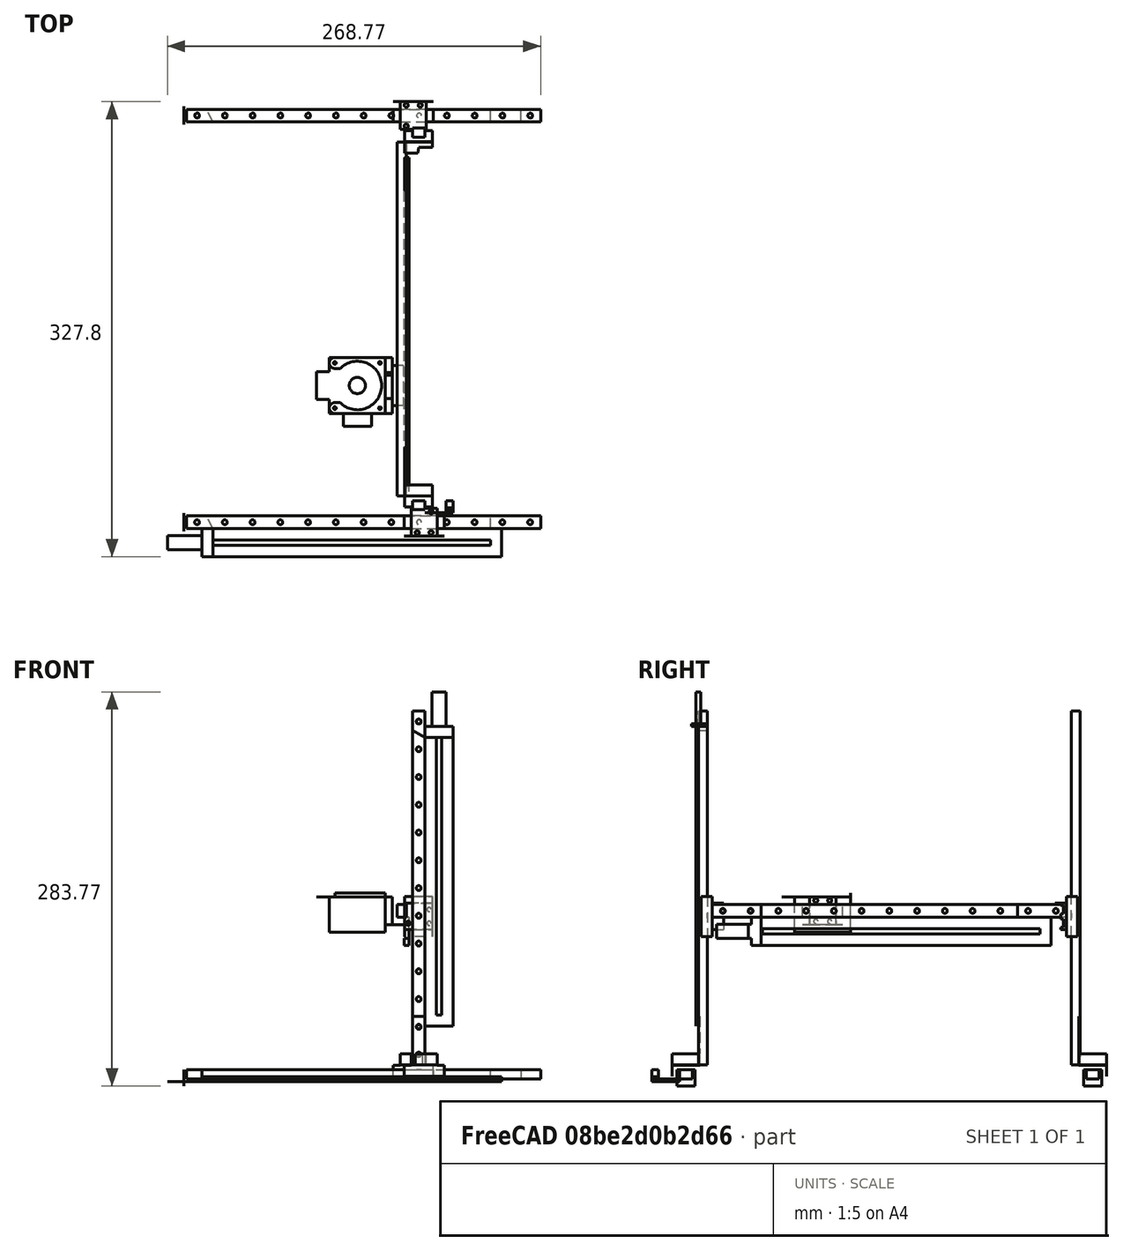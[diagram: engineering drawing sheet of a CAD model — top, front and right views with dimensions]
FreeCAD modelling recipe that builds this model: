
FCSTD DOCUMENT  (FreeCAD 0.21R33668 +26 (Git))
Label: v8
License: All rights reserved
LicenseURL: http://en.wikipedia.org/wiki/All_rights_reserved
objects: App::FeaturePython×217, Part::FeaturePython×128, App::Link×24
note: 127 computed .brp shape members not serialized (recipe doc carries the construction recipe); baked Part::Feature solids carry a one-line shape summary decoded from their .brp
EXTERNAL_REF file=parts/BaseMagnetoPot.FCStd obj=Body
EXTERNAL_REF file=parts/MG/mgn9c_13.FCStd obj=Body
EXTERNAL_REF file=parts/MG/mgn9c_slide.FCStd obj=Body001
EXTERNAL_REF file=parts/MagnetoPot/MagnetoPot.FCStd obj=Body
EXTERNAL_REF file=parts/NormalConnectorMagnet.FCStd obj=Body
EXTERNAL_REF file=parts/BaseMagnetoPot.FCStd obj=Body001
EXTERNAL_REF file=parts/NormalConnectorMagnet.FCStd obj=Body001
EXTERNAL_REF file=parts/Joystick_Holder.FCStd obj=Body
EXTERNAL_REF file=parts/R202.FCStd obj=Revolution

FEATURE [App::Link] Link  label="BaseMagentoPot"
  LinkedObject = -> <external parts/BaseMagnetoPot.FCStd>#Body
  _LinkOwner = 4
FEATURE [App::Link] Link001  label="Rail"
  LinkPlacement = pos=(-5.43338e-11,-6.2883e-12,2.71e-13) rot=(0,0,1;0rad)
  LinkedObject = -> <external parts/MG/mgn9c_13.FCStd>#Body
  Placement = pos=(-5.43338e-11,-6.2883e-12,2.71e-13) rot=(0,0,1;0rad)
  _LinkOwner = 4
FEATURE [App::Link] Link003  label="Slide"
  LinkPlacement = pos=(156.692,-5.5,2) rot=(0,0,1;0rad)
  LinkedObject = -> <external parts/MG/mgn9c_slide.FCStd>#Body001
  Placement = pos=(156.692,-5.5,2) rot=(0,0,1;0rad)
  _LinkOwner = 4
FEATURE [App::Link] Link004  label="MP1_L_0200_103_5_ST"
  LinkPlacement = pos=(11.12,-20.3,-2) rot=(0,0,1;0rad)
  LinkedObject = -> <external parts/MagnetoPot/MagnetoPot.FCStd>#Body
  Placement = pos=(11.12,-20.3,-2) rot=(0,0,1;0rad)
  _LinkOwner = 4
FEATURE [App::Link] Link005  label="NormalConnectorMagnet"
  LinkPlacement = pos=(156.692,-5.5,2) rot=(0,0,1;0rad)
  LinkedObject = -> <external parts/NormalConnectorMagnet.FCStd>#Body
  Placement = pos=(156.692,-5.5,2) rot=(0,0,1;0rad)
  _LinkOwner = 4
FEATURE [App::Link] Link006  label="Rail001"
  LinkPlacement = pos=(162.692,13.5,10) rot=(0.57735,0.57735,0.57735;4.18879rad)
  LinkedObject = -> <external parts/MG/mgn9c_13.FCStd>#Body
  Placement = pos=(162.692,13.5,10) rot=(0.57735,0.57735,0.57735;4.18879rad)
  _LinkOwner = 4
FEATURE [App::Link] Link007  label="BaseMagentoPot001"
  LinkPlacement = pos=(171.692,13.5,265) rot=(-0.57735,0.57735,0.57735;2.0944rad)
  LinkedObject = -> <external parts/BaseMagnetoPot.FCStd>#Body
  Placement = pos=(171.692,13.5,265) rot=(-0.57735,0.57735,0.57735;2.0944rad)
  _LinkOwner = 4
FEATURE [App::Link] Link008  label="MP1_L_0200_103_5_ST001"
  LinkPlacement = pos=(191.992,11.5,253.88) rot=(0.57735,-0.57735,-0.57735;4.18879rad)
  LinkedObject = -> <external parts/MagnetoPot/MagnetoPot.FCStd>#Body
  Placement = pos=(191.992,11.5,253.88) rot=(0.57735,-0.57735,-0.57735;4.18879rad)
  _LinkOwner = 4
FEATURE [App::Link] Link009  label="Slide001"
  LinkPlacement = pos=(157.192,15.5,102.634) rot=(0.57735,0.57735,0.57735;4.18879rad)
  LinkedObject = -> <external parts/MG/mgn9c_slide.FCStd>#Body001
  Placement = pos=(157.192,15.5,102.634) rot=(0.57735,0.57735,0.57735;4.18879rad)
  _LinkOwner = 4
FEATURE [App::Link] Link010  label="NormalConnectorMagnet001"
  LinkPlacement = pos=(177.192,15.5,131.534) rot=(0.57735,-0.57735,-0.57735;4.18879rad)
  LinkedObject = -> <external parts/NormalConnectorMagnet.FCStd>#Body
  Placement = pos=(177.192,15.5,131.534) rot=(0.57735,-0.57735,-0.57735;4.18879rad)
  _LinkOwner = 4
FEATURE [App::Link] Link011  label="MP1_L_0200_103_5_ST002"
  LinkPlacement = pos=(160.192,51.52,116.534) rot=(-0.57735,-0.57735,0.57735;2.0944rad)
  LinkedObject = -> <external parts/MagnetoPot/MagnetoPot.FCStd>#Body
  Placement = pos=(160.192,51.52,116.534) rot=(-0.57735,-0.57735,0.57735;2.0944rad)
  _LinkOwner = 4
FEATURE [App::Link] Link012  label="Rail002"
  LinkPlacement = pos=(158.192,23.5,125.534) rot=(0.57735,0.57735,-0.57735;4.18879rad)
  LinkedObject = -> <external parts/MG/mgn9c_13.FCStd>#Body
  Placement = pos=(158.192,23.5,125.534) rot=(0.57735,0.57735,-0.57735;4.18879rad)
  _LinkOwner = 4
FEATURE [App::Link] Link013  label="BaseMagnetoPot_Opposite"
  LinkPlacement = pos=(255,2.3947e-10,3.77443e-11) rot=(0,0,1;0rad)
  LinkedObject = -> <external parts/BaseMagnetoPot.FCStd>#Body001
  Placement = pos=(255,2.3947e-10,3.77443e-11) rot=(0,0,1;0rad)
  _LinkOwner = 4
FEATURE [App::Link] Link015  label="Slide002"
  LinkPlacement = pos=(177.192,286.5,102.634) rot=(-0.57735,0.57735,-0.57735;4.18879rad)
  LinkedObject = -> <external parts/MG/mgn9c_slide.FCStd>#Body001
  Placement = pos=(177.192,286.5,102.634) rot=(-0.57735,0.57735,-0.57735;4.18879rad)
  _LinkOwner = 4
FEATURE [App::Link] Link016  label="Rail003"
  LinkPlacement = pos=(171.692,288.5,10) rot=(0.57735,-0.57735,0.57735;2.0944rad)
  LinkedObject = -> <external parts/MG/mgn9c_13.FCStd>#Body
  Placement = pos=(171.692,288.5,10) rot=(0.57735,-0.57735,0.57735;2.0944rad)
  _LinkOwner = 4
FEATURE [App::Link] Link017  label="NormalConnectorMagnet002"
  LinkPlacement = pos=(177.692,307.5,2) rot=(0,0,1;3.14159rad)
  LinkedObject = -> <external parts/NormalConnectorMagnet.FCStd>#Body
  Placement = pos=(177.692,307.5,2) rot=(0,0,1;3.14159rad)
  _LinkOwner = 4
FEATURE [App::Link] Link018  label="Slide003"
  LinkPlacement = pos=(148.792,287.5,2) rot=(0,0,1;0rad)
  LinkedObject = -> <external parts/MG/mgn9c_slide.FCStd>#Body001
  Placement = pos=(148.792,287.5,2) rot=(0,0,1;0rad)
  _LinkOwner = 4
FEATURE [App::Link] Link019  label="Rail004"
  LinkPlacement = pos=(-5.5211e-10,293,-1.90036e-09) rot=(0,0,1;0rad)
  LinkedObject = -> <external parts/MG/mgn9c_13.FCStd>#Body
  Placement = pos=(-5.5211e-10,293,-1.90036e-09) rot=(0,0,1;0rad)
  _LinkOwner = 4
FEATURE [App::Link] Link020  label="BaseMagnetoPot_Opposite001"
  LinkPlacement = pos=(255,293,-2.0831e-09) rot=(0,0,1;0rad)
  LinkedObject = -> <external parts/BaseMagnetoPot.FCStd>#Body001
  Placement = pos=(255,293,-2.0831e-09) rot=(0,0,1;0rad)
  _LinkOwner = 4
FEATURE [App::Link] Link021  label="BaseMagentoPot002"
  LinkPlacement = pos=(-5.57052e-10,293,-1.68813e-09) rot=(0,0,1;0rad)
  LinkedObject = -> <external parts/BaseMagnetoPot.FCStd>#Body
  Placement = pos=(-5.57052e-10,293,-1.68813e-09) rot=(0,0,1;0rad)
  _LinkOwner = 4
FEATURE [App::Link] Link022  label="NormalConnector"
  LinkPlacement = pos=(177.192,270.5,131.534) rot=(-0.57735,0.57735,0.57735;2.0944rad)
  LinkedObject = -> <external parts/NormalConnectorMagnet.FCStd>#Body001
  Placement = pos=(177.192,270.5,131.534) rot=(-0.57735,0.57735,0.57735;2.0944rad)
  _LinkOwner = 4
FEATURE [App::Link] Link023  label="Slide004"
  LinkPlacement = pos=(156.192,117.438,111.034) rot=(-0.57735,0.57735,0.57735;4.18879rad)
  LinkedObject = -> <external parts/MG/mgn9c_slide.FCStd>#Body001
  Placement = pos=(156.192,117.438,111.034) rot=(-0.57735,0.57735,0.57735;4.18879rad)
  _LinkOwner = 4
FEATURE [App::Link] Link024  label="JoystickHolder"
  LinkPlacement = pos=(139.492,86.4879,131.034) rot=(0,0,1;0rad)
  LinkedObject = -> <external parts/Joystick_Holder.FCStd>#Body
  Placement = pos=(139.492,86.4879,131.034) rot=(0,0,1;0rad)
  _LinkOwner = 4
FEATURE [App::Link] Link025  label="Revolution"
  LinkPlacement = pos=(122.992,102.988,105.534) rot=(0,0,1;0rad)
  LinkedObject = -> <external parts/R202.FCStd>#Revolution
  Placement = pos=(122.992,102.988,105.534) rot=(0,0,1;0rad)
  _LinkOwner = 4
FEATURE [Part::FeaturePython] Parts  # WARN: FeaturePython — macro-defined, semantics opaque (R4)
  Group = -> [Link,Link001,Link003,Link004,Link005,Link006,Link007,Link008,Link009,Link010,Link011,Link012,Link013,Link015,Link016,Link017,Link018,Link019,Link020,Link021,Link022,Link023,Link024,Link025]
  GroupMode = 0
FEATURE [Part::FeaturePython] Assembly  # WARN: FeaturePython — macro-defined, semantics opaque (R4)
  AutoRelax = true
  BuildShape = 0
  Freeze = false
  Group = -> [Constraints,Elements,Parts]
  Verbose = false
  _SolverType = 1
  _Version = 1
FEATURE [App::FeaturePython] Constraints  # WARN: FeaturePython — macro-defined, semantics opaque (R4)
  Group = -> [Constraint,Constraint001,Constraint002,Constraint003,Constraint007,Constraint008,Constraint009,Constraint010,Constraint011,Constraint012,Constraint013,Constraint014,Constraint015,Constraint016,Constraint017,Constraint018,Constraint019,Constraint020,Constraint021,Constraint022,Constraint023,Constraint024,Constraint025,Constraint026,Constraint027,Constraint028,Constraint029,Constraint030,+44 more]
  _Version = 1
FEATURE [App::FeaturePython] Elements  # WARN: FeaturePython — macro-defined, semantics opaque (R4)
  Group = -> [_Element,_Element001,_Element002,_Element003,_Element004,_Element005,_Element008,_Element010,_Element011,_Element012,_Element013,_Element014,_Element015,_Element016,_Element017,_Element018,_Element019,_Element020,_Element021,_Element022,_Element023,_Element024,_Element025,_Element026,_Element027,_Element028,_Element029,_Element030,_Element031,_Element032,_Element033,_Element034,_Element035,+93 more]
FEATURE [App::FeaturePython] Constraint  label="Locked"  # WARN: FeaturePython — macro-defined, semantics opaque (R4)
  Disabled = false
  Group = -> [ElementLink]
  _ConstraintType = 0
  _Parent = -> Constraints
FEATURE [App::FeaturePython] ElementLink  label="_Element"  # link proxy (typed FeaturePython)
  LinkTransform = true
  LinkedObject = -> _Element
  _Parent = -> Constraint
FEATURE [Part::FeaturePython] _Element  # link proxy (typed FeaturePython)
  Detach = false
  LinkTransform = true
  LinkedObject = -> Link [Pad001.Face2]
  _Parent = -> Elements
FEATURE [App::FeaturePython] Constraint001  label="PlaneAlignment"  # WARN: FeaturePython — macro-defined, semantics opaque (R4)
  Angle = 0
  AnglePitch = 0
  AngleRoll = 0
  Cascade = false
  Disabled = false
  Group = -> [ElementLink001,ElementLink002]
  LockAngle = false
  _ConstraintType = 37
  _Parent = -> Constraints
FEATURE [App::FeaturePython] ElementLink001  label="_Element001"  # link proxy (typed FeaturePython)
  LinkTransform = true
  LinkedObject = -> _Element001
  _Parent = -> Constraint001
FEATURE [Part::FeaturePython] _Element001  # link proxy (typed FeaturePython)
  Detach = false
  LinkTransform = true
  LinkedObject = -> Link001 [LinearPattern.Face2]
  _Parent = -> Elements
FEATURE [App::FeaturePython] ElementLink002  label="_Element002"  # link proxy (typed FeaturePython)
  LinkTransform = true
  LinkedObject = -> _Element002
  _Parent = -> Constraint001
FEATURE [Part::FeaturePython] _Element002  # link proxy (typed FeaturePython)
  Detach = false
  LinkTransform = true
  LinkedObject = -> Link [Pad001.Face7]
  _Parent = -> Elements
FEATURE [App::FeaturePython] Constraint002  label="PlaneAlignment001"  # WARN: FeaturePython — macro-defined, semantics opaque (R4)
  Angle = 0
  AnglePitch = 0
  AngleRoll = 0
  Cascade = false
  Disabled = false
  Group = -> [ElementLink003,ElementLink004]
  LockAngle = false
  _ConstraintType = 37
  _Parent = -> Constraints
FEATURE [App::FeaturePython] ElementLink003  label="_Element"  # link proxy (typed FeaturePython)
  LinkTransform = true
  LinkedObject = -> _Element
  _Parent = -> Constraint002
FEATURE [App::FeaturePython] ElementLink004  label="_Element003"  # link proxy (typed FeaturePython)
  LinkTransform = true
  LinkedObject = -> _Element003
  _Parent = -> Constraint002
FEATURE [Part::FeaturePython] _Element003  # link proxy (typed FeaturePython)
  Detach = false
  LinkTransform = true
  LinkedObject = -> Link001 [LinearPattern.Face4]
  _Parent = -> Elements
FEATURE [App::FeaturePython] Constraint003  label="PlaneAlignment002"  # WARN: FeaturePython — macro-defined, semantics opaque (R4)
  Angle = 0
  AnglePitch = 0
  AngleRoll = 0
  Cascade = false
  Disabled = false
  Group = -> [ElementLink005,ElementLink006]
  LockAngle = false
  _ConstraintType = 37
  _Parent = -> Constraints
FEATURE [App::FeaturePython] ElementLink005  label="_Element004"  # link proxy (typed FeaturePython)
  LinkTransform = true
  LinkedObject = -> _Element004
  _Parent = -> Constraint003
FEATURE [Part::FeaturePython] _Element004  # link proxy (typed FeaturePython)
  Detach = false
  LinkTransform = true
  LinkedObject = -> Link001 [LinearPattern.Face1]
  _Parent = -> Elements
FEATURE [App::FeaturePython] ElementLink006  label="_Element005"  # link proxy (typed FeaturePython)
  LinkTransform = true
  LinkedObject = -> _Element005
  _Parent = -> Constraint003
FEATURE [Part::FeaturePython] _Element005  # link proxy (typed FeaturePython)
  Detach = false
  LinkTransform = true
  LinkedObject = -> Link [Pad001.Face8]
  _Parent = -> Elements
FEATURE [Part::FeaturePython] _Element008  # link proxy (typed FeaturePython)
  Detach = false
  LinkTransform = true
  LinkedObject = -> Link [Pad001.Face10]
  _Parent = -> Elements
FEATURE [App::FeaturePython] Constraint007  label="PlaneAlignment006"  # WARN: FeaturePython — macro-defined, semantics opaque (R4)
  Angle = 0
  AnglePitch = 0
  AngleRoll = 0
  Cascade = false
  Disabled = false
  Group = -> [ElementLink013,ElementLink014]
  LockAngle = false
  _ConstraintType = 37
  _Parent = -> Constraints
FEATURE [App::FeaturePython] ElementLink013  label="_Element010"  # link proxy (typed FeaturePython)
  LinkTransform = true
  LinkedObject = -> _Element010
  _Parent = -> Constraint007
FEATURE [Part::FeaturePython] _Element010  # link proxy (typed FeaturePython)
  Detach = false
  LinkTransform = true
  LinkedObject = -> Link003 [Pocket003.Face12]
  _Parent = -> Elements
FEATURE [App::FeaturePython] ElementLink014  label="_Element011"  # link proxy (typed FeaturePython)
  LinkTransform = true
  LinkedObject = -> _Element011
  _Parent = -> Constraint007
FEATURE [Part::FeaturePython] _Element011  # link proxy (typed FeaturePython)
  Detach = false
  LinkTransform = true
  LinkedObject = -> Link001 [LinearPattern.Face6]
  _Parent = -> Elements
FEATURE [App::FeaturePython] Constraint008  label="PlaneAlignment007"  # WARN: FeaturePython — macro-defined, semantics opaque (R4)
  Angle = 0
  AnglePitch = 0
  AngleRoll = 0
  Cascade = false
  Disabled = false
  Group = -> [ElementLink015,ElementLink016]
  LockAngle = false
  _ConstraintType = 37
  _Parent = -> Constraints
FEATURE [App::FeaturePython] ElementLink015  label="_Element012"  # link proxy (typed FeaturePython)
  LinkTransform = true
  LinkedObject = -> _Element012
  _Parent = -> Constraint008
FEATURE [Part::FeaturePython] _Element012  # link proxy (typed FeaturePython)
  Detach = false
  LinkTransform = true
  LinkedObject = -> Link003 [Pocket003.Face11]
  _Parent = -> Elements
FEATURE [App::FeaturePython] ElementLink016  label="_Element013"  # link proxy (typed FeaturePython)
  LinkTransform = true
  LinkedObject = -> _Element013
  _Parent = -> Constraint008
FEATURE [Part::FeaturePython] _Element013  # link proxy (typed FeaturePython)
  Detach = false
  LinkTransform = true
  LinkedObject = -> Link001 [LinearPattern.Face5]
  _Parent = -> Elements
FEATURE [App::FeaturePython] Constraint009  label="PlaneAlignment008"  # WARN: FeaturePython — macro-defined, semantics opaque (R4)
  Angle = 0
  AnglePitch = 0
  AngleRoll = 0
  Cascade = false
  Disabled = false
  Group = -> [ElementLink017,ElementLink018]
  LockAngle = false
  _ConstraintType = 37
  _Parent = -> Constraints
FEATURE [App::FeaturePython] ElementLink017  label="_Element014"  # link proxy (typed FeaturePython)
  LinkTransform = true
  LinkedObject = -> _Element014
  _Parent = -> Constraint009
FEATURE [Part::FeaturePython] _Element014  # link proxy (typed FeaturePython)
  Detach = false
  LinkTransform = true
  LinkedObject = -> Link004 [Pad.Face4]
  _Parent = -> Elements
FEATURE [App::FeaturePython] ElementLink018  label="_Element015"  # link proxy (typed FeaturePython)
  LinkTransform = true
  LinkedObject = -> _Element015
  _Parent = -> Constraint009
FEATURE [Part::FeaturePython] _Element015  # link proxy (typed FeaturePython)
  Detach = false
  LinkTransform = true
  LinkedObject = -> Link [Pocket.Face15]
  _Parent = -> Elements
FEATURE [App::FeaturePython] Constraint010  label="PlaneAlignment009"  # WARN: FeaturePython — macro-defined, semantics opaque (R4)
  Angle = 0
  AnglePitch = 0
  AngleRoll = 0
  Cascade = false
  Disabled = false
  Group = -> [ElementLink019,ElementLink020]
  LockAngle = false
  _ConstraintType = 37
  _Parent = -> Constraints
FEATURE [App::FeaturePython] ElementLink019  label="_Element016"  # link proxy (typed FeaturePython)
  LinkTransform = true
  LinkedObject = -> _Element016
  _Parent = -> Constraint010
FEATURE [Part::FeaturePython] _Element016  # link proxy (typed FeaturePython)
  Detach = false
  LinkTransform = true
  LinkedObject = -> Link004 [Pad.Face1]
  _Parent = -> Elements
FEATURE [App::FeaturePython] ElementLink020  label="_Element017"  # link proxy (typed FeaturePython)
  LinkTransform = true
  LinkedObject = -> _Element017
  _Parent = -> Constraint010
FEATURE [Part::FeaturePython] _Element017  # link proxy (typed FeaturePython)
  Detach = false
  LinkTransform = true
  LinkedObject = -> Link [Pocket.Face4]
  _Parent = -> Elements
FEATURE [App::FeaturePython] Constraint011  label="PlaneAlignment010"  # WARN: FeaturePython — macro-defined, semantics opaque (R4)
  Angle = 0
  AnglePitch = 0
  AngleRoll = 0
  Cascade = false
  Disabled = false
  Group = -> [ElementLink021,ElementLink022]
  LockAngle = false
  _ConstraintType = 37
  _Parent = -> Constraints
FEATURE [App::FeaturePython] ElementLink021  label="_Element018"  # link proxy (typed FeaturePython)
  LinkTransform = true
  LinkedObject = -> _Element018
  _Parent = -> Constraint011
FEATURE [Part::FeaturePython] _Element018  # link proxy (typed FeaturePython)
  Detach = false
  LinkTransform = true
  LinkedObject = -> Link [Pocket.Face8]
  _Parent = -> Elements
FEATURE [App::FeaturePython] ElementLink022  label="_Element019"  # link proxy (typed FeaturePython)
  LinkTransform = true
  LinkedObject = -> _Element019
  _Parent = -> Constraint011
FEATURE [Part::FeaturePython] _Element019  # link proxy (typed FeaturePython)
  Detach = false
  LinkTransform = true
  LinkedObject = -> Link004 [Pad.Face13]
  _Parent = -> Elements
FEATURE [App::FeaturePython] Constraint012  label="PlaneAlignment011"  # WARN: FeaturePython — macro-defined, semantics opaque (R4)
  Angle = 0
  AnglePitch = 0
  AngleRoll = 0
  Cascade = false
  Disabled = false
  Group = -> [ElementLink023,ElementLink024]
  LockAngle = false
  _ConstraintType = 37
  _Parent = -> Constraints
FEATURE [App::FeaturePython] ElementLink023  label="_Element020"  # link proxy (typed FeaturePython)
  LinkTransform = true
  LinkedObject = -> _Element020
  _Parent = -> Constraint012
FEATURE [Part::FeaturePython] _Element020  # link proxy (typed FeaturePython)
  Detach = false
  LinkTransform = true
  LinkedObject = -> Link005 [Pocket003.Face2]
  _Parent = -> Elements
FEATURE [App::FeaturePython] ElementLink024  label="_Element021"  # link proxy (typed FeaturePython)
  LinkTransform = true
  LinkedObject = -> _Element021
  _Parent = -> Constraint012
FEATURE [Part::FeaturePython] _Element021  # link proxy (typed FeaturePython)
  Detach = false
  LinkTransform = true
  LinkedObject = -> Link003 [Pocket003.Face6]
  _Parent = -> Elements
FEATURE [App::FeaturePython] Constraint013  label="PlaneAlignment012"  # WARN: FeaturePython — macro-defined, semantics opaque (R4)
  Angle = 0
  AnglePitch = 0
  AngleRoll = 0
  Cascade = false
  Disabled = false
  Group = -> [ElementLink025,ElementLink026]
  LockAngle = false
  _ConstraintType = 37
  _Parent = -> Constraints
FEATURE [App::FeaturePython] ElementLink025  label="_Element022"  # link proxy (typed FeaturePython)
  LinkTransform = true
  LinkedObject = -> _Element022
  _Parent = -> Constraint013
FEATURE [Part::FeaturePython] _Element022  # link proxy (typed FeaturePython)
  Detach = false
  LinkTransform = true
  LinkedObject = -> Link005 [Pocket003.Face10]
  _Parent = -> Elements
FEATURE [App::FeaturePython] ElementLink026  label="_Element023"  # link proxy (typed FeaturePython)
  LinkTransform = true
  LinkedObject = -> _Element023
  _Parent = -> Constraint013
FEATURE [Part::FeaturePython] _Element023  # link proxy (typed FeaturePython)
  Detach = false
  LinkTransform = true
  LinkedObject = -> Link003 [Pocket003.Face1]
  _Parent = -> Elements
FEATURE [App::FeaturePython] Constraint014  label="PlaneAlignment013"  # WARN: FeaturePython — macro-defined, semantics opaque (R4)
  Angle = 0
  AnglePitch = 0
  AngleRoll = 0
  Cascade = false
  Disabled = false
  Group = -> [ElementLink027,ElementLink028]
  LockAngle = false
  _ConstraintType = 37
  _Parent = -> Constraints
FEATURE [App::FeaturePython] ElementLink027  label="_Element024"  # link proxy (typed FeaturePython)
  LinkTransform = true
  LinkedObject = -> _Element024
  _Parent = -> Constraint014
FEATURE [Part::FeaturePython] _Element024  # link proxy (typed FeaturePython)
  Detach = false
  LinkTransform = true
  LinkedObject = -> Link005 [Pocket003.Face5]
  _Parent = -> Elements
FEATURE [App::FeaturePython] ElementLink028  label="_Element025"  # link proxy (typed FeaturePython)
  LinkTransform = true
  LinkedObject = -> _Element025
  _Parent = -> Constraint014
FEATURE [Part::FeaturePython] _Element025  # link proxy (typed FeaturePython)
  Detach = false
  LinkTransform = true
  LinkedObject = -> Link003 [Pocket003.Face7]
  _Parent = -> Elements
FEATURE [App::FeaturePython] Constraint015  label="PlaneAlignment014"  # WARN: FeaturePython — macro-defined, semantics opaque (R4)
  Angle = 0
  AnglePitch = 0
  AngleRoll = 0
  Cascade = false
  Disabled = false
  Group = -> [ElementLink029,ElementLink030]
  LockAngle = false
  _ConstraintType = 37
  _Parent = -> Constraints
FEATURE [App::FeaturePython] ElementLink029  label="_Element026"  # link proxy (typed FeaturePython)
  LinkTransform = true
  LinkedObject = -> _Element026
  _Parent = -> Constraint015
FEATURE [Part::FeaturePython] _Element026  # link proxy (typed FeaturePython)
  Detach = false
  LinkTransform = true
  LinkedObject = -> Link006 [LinearPattern.Face4]
  _Parent = -> Elements
FEATURE [App::FeaturePython] ElementLink030  label="_Element027"  # link proxy (typed FeaturePython)
  LinkTransform = true
  LinkedObject = -> _Element027
  _Parent = -> Constraint015
FEATURE [Part::FeaturePython] _Element027  # link proxy (typed FeaturePython)
  Detach = false
  LinkTransform = true
  LinkedObject = -> Link005 [Pocket003.Face6]
  _Parent = -> Elements
FEATURE [App::FeaturePython] Constraint016  label="PlaneAlignment015"  # WARN: FeaturePython — macro-defined, semantics opaque (R4)
  Angle = 0
  AnglePitch = 0
  AngleRoll = 0
  Cascade = false
  Disabled = false
  Group = -> [ElementLink031,ElementLink032]
  LockAngle = false
  _ConstraintType = 37
  _Parent = -> Constraints
FEATURE [App::FeaturePython] ElementLink031  label="_Element021"  # link proxy (typed FeaturePython)
  LinkTransform = true
  LinkedObject = -> _Element021
  _Parent = -> Constraint016
FEATURE [App::FeaturePython] ElementLink032  label="_Element028"  # link proxy (typed FeaturePython)
  LinkTransform = true
  LinkedObject = -> _Element028
  _Parent = -> Constraint016
FEATURE [Part::FeaturePython] _Element028  # link proxy (typed FeaturePython)
  Detach = false
  LinkTransform = true
  LinkedObject = -> Link006 [LinearPattern.Face2]
  _Parent = -> Elements
FEATURE [App::FeaturePython] Constraint017  label="PlaneAlignment016"  # WARN: FeaturePython — macro-defined, semantics opaque (R4)
  Angle = 0
  AnglePitch = 0
  AngleRoll = 0
  Cascade = false
  Disabled = false
  Group = -> [ElementLink033,ElementLink034]
  LockAngle = false
  _ConstraintType = 37
  _Parent = -> Constraints
FEATURE [App::FeaturePython] ElementLink033  label="_Element029"  # link proxy (typed FeaturePython)
  LinkTransform = true
  LinkedObject = -> _Element029
  _Parent = -> Constraint017
FEATURE [Part::FeaturePython] _Element029  # link proxy (typed FeaturePython)
  Detach = false
  LinkTransform = true
  LinkedObject = -> Link005 [Pocket003.Face3]
  _Parent = -> Elements
FEATURE [App::FeaturePython] ElementLink034  label="_Element030"  # link proxy (typed FeaturePython)
  LinkTransform = true
  LinkedObject = -> _Element030
  _Parent = -> Constraint017
FEATURE [Part::FeaturePython] _Element030  # link proxy (typed FeaturePython)
  Detach = false
  LinkTransform = true
  LinkedObject = -> Link006 [LinearPattern.Face1]
  _Parent = -> Elements
FEATURE [App::FeaturePython] Constraint018  label="PlaneAlignment017"  # WARN: FeaturePython — macro-defined, semantics opaque (R4)
  Angle = 0
  AnglePitch = 0
  AngleRoll = 0
  Cascade = false
  Disabled = false
  Group = -> [ElementLink035,ElementLink036]
  LockAngle = false
  _ConstraintType = 37
  _Parent = -> Constraints
FEATURE [App::FeaturePython] ElementLink035  label="_Element031"  # link proxy (typed FeaturePython)
  LinkTransform = true
  LinkedObject = -> _Element031
  _Parent = -> Constraint018
FEATURE [Part::FeaturePython] _Element031  # link proxy (typed FeaturePython)
  Detach = false
  LinkTransform = true
  LinkedObject = -> Link007 [Pocket.Face30]
  _Parent = -> Elements
FEATURE [App::FeaturePython] ElementLink036  label="_Element030"  # link proxy (typed FeaturePython)
  LinkTransform = true
  LinkedObject = -> _Element030
  _Parent = -> Constraint018
FEATURE [App::FeaturePython] Constraint019  label="PlaneAlignment018"  # WARN: FeaturePython — macro-defined, semantics opaque (R4)
  Angle = 0
  AnglePitch = 0
  AngleRoll = 0
  Cascade = false
  Disabled = false
  Group = -> [ElementLink037,ElementLink038]
  LockAngle = false
  _ConstraintType = 37
  _Parent = -> Constraints
FEATURE [App::FeaturePython] ElementLink037  label="_Element032"  # link proxy (typed FeaturePython)
  LinkTransform = true
  LinkedObject = -> _Element032
  _Parent = -> Constraint019
FEATURE [Part::FeaturePython] _Element032  # link proxy (typed FeaturePython)
  Detach = false
  LinkTransform = true
  LinkedObject = -> Link006 [LinearPattern.Face3]
  _Parent = -> Elements
FEATURE [App::FeaturePython] ElementLink038  label="_Element033"  # link proxy (typed FeaturePython)
  LinkTransform = true
  LinkedObject = -> _Element033
  _Parent = -> Constraint019
FEATURE [Part::FeaturePython] _Element033  # link proxy (typed FeaturePython)
  Detach = false
  LinkTransform = true
  LinkedObject = -> Link007 [Pocket.Face31]
  _Parent = -> Elements
FEATURE [App::FeaturePython] Constraint020  label="PlaneAlignment019"  # WARN: FeaturePython — macro-defined, semantics opaque (R4)
  Angle = 0
  AnglePitch = 0
  AngleRoll = 0
  Cascade = false
  Disabled = false
  Group = -> [ElementLink039,ElementLink040]
  LockAngle = false
  _ConstraintType = 37
  _Parent = -> Constraints
FEATURE [App::FeaturePython] ElementLink039  label="_Element034"  # link proxy (typed FeaturePython)
  LinkTransform = true
  LinkedObject = -> _Element034
  _Parent = -> Constraint020
FEATURE [Part::FeaturePython] _Element034  # link proxy (typed FeaturePython)
  Detach = false
  LinkTransform = true
  LinkedObject = -> Link007 [Pocket.Face24]
  _Parent = -> Elements
FEATURE [App::FeaturePython] ElementLink040  label="_Element026"  # link proxy (typed FeaturePython)
  LinkTransform = true
  LinkedObject = -> _Element026
  _Parent = -> Constraint020
FEATURE [App::FeaturePython] Constraint021  label="PlaneAlignment020"  # WARN: FeaturePython — macro-defined, semantics opaque (R4)
  Angle = 0
  AnglePitch = 0
  AngleRoll = 0
  Cascade = false
  Disabled = false
  Group = -> [ElementLink041,ElementLink042]
  LockAngle = false
  _ConstraintType = 37
  _Parent = -> Constraints
FEATURE [App::FeaturePython] ElementLink041  label="_Element035"  # link proxy (typed FeaturePython)
  LinkTransform = true
  LinkedObject = -> _Element035
  _Parent = -> Constraint021
FEATURE [Part::FeaturePython] _Element035  # link proxy (typed FeaturePython)
  Detach = false
  LinkTransform = true
  LinkedObject = -> Link008 [Pad.Face8]
  _Parent = -> Elements
FEATURE [App::FeaturePython] ElementLink042  label="_Element036"  # link proxy (typed FeaturePython)
  LinkTransform = true
  LinkedObject = -> _Element036
  _Parent = -> Constraint021
FEATURE [Part::FeaturePython] _Element036  # link proxy (typed FeaturePython)
  Detach = false
  LinkTransform = true
  LinkedObject = -> Link007 [Pocket.Face1]
  _Parent = -> Elements
FEATURE [App::FeaturePython] Constraint022  label="PlaneAlignment021"  # WARN: FeaturePython — macro-defined, semantics opaque (R4)
  Angle = 0
  AnglePitch = 0
  AngleRoll = 0
  Cascade = false
  Disabled = false
  Group = -> [ElementLink043,ElementLink044]
  LockAngle = false
  _ConstraintType = 37
  _Parent = -> Constraints
FEATURE [App::FeaturePython] ElementLink043  label="_Element037"  # link proxy (typed FeaturePython)
  LinkTransform = true
  LinkedObject = -> _Element037
  _Parent = -> Constraint022
FEATURE [Part::FeaturePython] _Element037  # link proxy (typed FeaturePython)
  Detach = false
  LinkTransform = true
  LinkedObject = -> Link008 [Pad.Face1]
  _Parent = -> Elements
FEATURE [App::FeaturePython] ElementLink044  label="_Element038"  # link proxy (typed FeaturePython)
  LinkTransform = true
  LinkedObject = -> _Element038
  _Parent = -> Constraint022
FEATURE [Part::FeaturePython] _Element038  # link proxy (typed FeaturePython)
  Detach = false
  LinkTransform = true
  LinkedObject = -> Link007 [Pocket.Face4]
  _Parent = -> Elements
FEATURE [App::FeaturePython] Constraint023  label="PlaneAlignment022"  # WARN: FeaturePython — macro-defined, semantics opaque (R4)
  Angle = 0
  AnglePitch = 0
  AngleRoll = 0
  Cascade = false
  Disabled = false
  Group = -> [ElementLink045,ElementLink046]
  LockAngle = false
  _ConstraintType = 37
  _Parent = -> Constraints
FEATURE [App::FeaturePython] ElementLink045  label="_Element039"  # link proxy (typed FeaturePython)
  LinkTransform = true
  LinkedObject = -> _Element039
  _Parent = -> Constraint023
FEATURE [Part::FeaturePython] _Element039  # link proxy (typed FeaturePython)
  Detach = false
  LinkTransform = true
  LinkedObject = -> Link008 [Pad.Face13]
  _Parent = -> Elements
FEATURE [App::FeaturePython] ElementLink046  label="_Element040"  # link proxy (typed FeaturePython)
  LinkTransform = true
  LinkedObject = -> _Element040
  _Parent = -> Constraint023
FEATURE [Part::FeaturePython] _Element040  # link proxy (typed FeaturePython)
  Detach = false
  LinkTransform = true
  LinkedObject = -> Link007 [Pocket.Face8]
  _Parent = -> Elements
FEATURE [App::FeaturePython] Constraint024  label="PlaneAlignment023"  # WARN: FeaturePython — macro-defined, semantics opaque (R4)
  Angle = 0
  AnglePitch = 0
  AngleRoll = 0
  Cascade = false
  Disabled = false
  Group = -> [ElementLink047,ElementLink048]
  LockAngle = false
  _ConstraintType = 37
  _Parent = -> Constraints
FEATURE [App::FeaturePython] ElementLink047  label="_Element041"  # link proxy (typed FeaturePython)
  LinkTransform = true
  LinkedObject = -> _Element041
  _Parent = -> Constraint024
FEATURE [Part::FeaturePython] _Element041  # link proxy (typed FeaturePython)
  Detach = false
  LinkTransform = true
  LinkedObject = -> Link009 [Pocket003.Face11]
  _Parent = -> Elements
FEATURE [App::FeaturePython] ElementLink048  label="_Element042"  # link proxy (typed FeaturePython)
  LinkTransform = true
  LinkedObject = -> _Element042
  _Parent = -> Constraint024
FEATURE [Part::FeaturePython] _Element042  # link proxy (typed FeaturePython)
  Detach = false
  LinkTransform = true
  LinkedObject = -> Link006 [LinearPattern.Face5]
  _Parent = -> Elements
FEATURE [App::FeaturePython] Constraint025  label="PlaneAlignment024"  # WARN: FeaturePython — macro-defined, semantics opaque (R4)
  Angle = 0
  AnglePitch = 0
  AngleRoll = 0
  Cascade = false
  Disabled = false
  Group = -> [ElementLink049,ElementLink050]
  LockAngle = false
  _ConstraintType = 37
  _Parent = -> Constraints
FEATURE [App::FeaturePython] ElementLink049  label="_Element043"  # link proxy (typed FeaturePython)
  LinkTransform = true
  LinkedObject = -> _Element043
  _Parent = -> Constraint025
FEATURE [Part::FeaturePython] _Element043  # link proxy (typed FeaturePython)
  Detach = false
  LinkTransform = true
  LinkedObject = -> Link009 [Pocket003.Face12]
  _Parent = -> Elements
FEATURE [App::FeaturePython] ElementLink050  label="_Element044"  # link proxy (typed FeaturePython)
  LinkTransform = true
  LinkedObject = -> _Element044
  _Parent = -> Constraint025
FEATURE [Part::FeaturePython] _Element044  # link proxy (typed FeaturePython)
  Detach = false
  LinkTransform = true
  LinkedObject = -> Link006 [LinearPattern.Face6]
  _Parent = -> Elements
FEATURE [App::FeaturePython] Constraint026  label="PlaneAlignment025"  # WARN: FeaturePython — macro-defined, semantics opaque (R4)
  Angle = 0
  AnglePitch = 0
  AngleRoll = 0
  Cascade = false
  Disabled = false
  Group = -> [ElementLink051,ElementLink052]
  LockAngle = false
  _ConstraintType = 37
  _Parent = -> Constraints
FEATURE [App::FeaturePython] ElementLink051  label="_Element045"  # link proxy (typed FeaturePython)
  LinkTransform = true
  LinkedObject = -> _Element045
  _Parent = -> Constraint026
FEATURE [Part::FeaturePython] _Element045  # link proxy (typed FeaturePython)
  Detach = false
  LinkTransform = true
  LinkedObject = -> Link010 [Pocket003.Face2]
  _Parent = -> Elements
FEATURE [App::FeaturePython] ElementLink052  label="_Element046"  # link proxy (typed FeaturePython)
  LinkTransform = true
  LinkedObject = -> _Element046
  _Parent = -> Constraint026
FEATURE [Part::FeaturePython] _Element046  # link proxy (typed FeaturePython)
  Detach = false
  LinkTransform = true
  LinkedObject = -> Link009 [Pocket003.Face6]
  _Parent = -> Elements
FEATURE [App::FeaturePython] Constraint027  label="PlaneAlignment026"  # WARN: FeaturePython — macro-defined, semantics opaque (R4)
  Angle = 0
  AnglePitch = 0
  AngleRoll = 0
  Cascade = false
  Disabled = false
  Group = -> [ElementLink053,ElementLink054]
  LockAngle = false
  _ConstraintType = 37
  _Parent = -> Constraints
FEATURE [App::FeaturePython] ElementLink053  label="_Element047"  # link proxy (typed FeaturePython)
  LinkTransform = true
  LinkedObject = -> _Element047
  _Parent = -> Constraint027
FEATURE [Part::FeaturePython] _Element047  # link proxy (typed FeaturePython)
  Detach = false
  LinkTransform = true
  LinkedObject = -> Link010 [Pocket003.Face5]
  _Parent = -> Elements
FEATURE [App::FeaturePython] ElementLink054  label="_Element048"  # link proxy (typed FeaturePython)
  LinkTransform = true
  LinkedObject = -> _Element048
  _Parent = -> Constraint027
FEATURE [Part::FeaturePython] _Element048  # link proxy (typed FeaturePython)
  Detach = false
  LinkTransform = true
  LinkedObject = -> Link009 [Pocket003.Face5]
  _Parent = -> Elements
FEATURE [App::FeaturePython] Constraint028  label="PlaneAlignment027"  # WARN: FeaturePython — macro-defined, semantics opaque (R4)
  Angle = 0
  AnglePitch = 0
  AngleRoll = 0
  Cascade = false
  Disabled = false
  Group = -> [ElementLink055,ElementLink056]
  LockAngle = false
  _ConstraintType = 37
  _Parent = -> Constraints
FEATURE [App::FeaturePython] ElementLink055  label="_Element049"  # link proxy (typed FeaturePython)
  LinkTransform = true
  LinkedObject = -> _Element049
  _Parent = -> Constraint028
FEATURE [Part::FeaturePython] _Element049  # link proxy (typed FeaturePython)
  Detach = false
  LinkTransform = true
  LinkedObject = -> Link010 [Pocket003.Face8]
  _Parent = -> Elements
FEATURE [App::FeaturePython] ElementLink056  label="_Element050"  # link proxy (typed FeaturePython)
  LinkTransform = true
  LinkedObject = -> _Element050
  _Parent = -> Constraint028
FEATURE [Part::FeaturePython] _Element050  # link proxy (typed FeaturePython)
  Detach = false
  LinkTransform = true
  LinkedObject = -> Link009 [Pocket003.Face1]
  _Parent = -> Elements
FEATURE [App::FeaturePython] Constraint029  label="PlaneAlignment028"  # WARN: FeaturePython — macro-defined, semantics opaque (R4)
  Angle = 0
  AnglePitch = 0
  AngleRoll = 0
  Cascade = false
  Disabled = false
  Group = -> [ElementLink057,ElementLink058]
  LockAngle = false
  _ConstraintType = 37
  _Parent = -> Constraints
FEATURE [App::FeaturePython] ElementLink057  label="_Element051"  # link proxy (typed FeaturePython)
  LinkTransform = true
  LinkedObject = -> _Element051
  _Parent = -> Constraint029
FEATURE [Part::FeaturePython] _Element051  # link proxy (typed FeaturePython)
  Detach = false
  LinkTransform = true
  LinkedObject = -> Link011 [Pad.Face2]
  _Parent = -> Elements
FEATURE [App::FeaturePython] ElementLink058  label="_Element052"  # link proxy (typed FeaturePython)
  LinkTransform = true
  LinkedObject = -> _Element052
  _Parent = -> Constraint029
FEATURE [Part::FeaturePython] _Element052  # link proxy (typed FeaturePython)
  Detach = false
  LinkTransform = true
  LinkedObject = -> Link010 [Pocket004.Face23]
  _Parent = -> Elements
FEATURE [App::FeaturePython] Constraint030  label="PlaneAlignment029"  # WARN: FeaturePython — macro-defined, semantics opaque (R4)
  Angle = 0
  AnglePitch = 0
  AngleRoll = 0
  Cascade = false
  Disabled = false
  Group = -> [ElementLink059,ElementLink060]
  LockAngle = false
  _ConstraintType = 37
  _Parent = -> Constraints
FEATURE [App::FeaturePython] ElementLink059  label="_Element053"  # link proxy (typed FeaturePython)
  LinkTransform = true
  LinkedObject = -> _Element053
  _Parent = -> Constraint030
FEATURE [Part::FeaturePython] _Element053  # link proxy (typed FeaturePython)
  Detach = false
  LinkTransform = true
  LinkedObject = -> Link011 [Pad.Face5]
  _Parent = -> Elements
FEATURE [App::FeaturePython] ElementLink060  label="_Element054"  # link proxy (typed FeaturePython)
  LinkTransform = true
  LinkedObject = -> _Element054
  _Parent = -> Constraint030
FEATURE [Part::FeaturePython] _Element054  # link proxy (typed FeaturePython)
  Detach = false
  LinkTransform = true
  LinkedObject = -> Link010 [Pocket004.Face27]
  _Parent = -> Elements
FEATURE [App::FeaturePython] Constraint031  label="PlaneAlignment030"  # WARN: FeaturePython — macro-defined, semantics opaque (R4)
  Angle = 0
  AnglePitch = 0
  AngleRoll = 0
  Cascade = false
  Disabled = false
  Group = -> [ElementLink061,ElementLink062]
  LockAngle = false
  _ConstraintType = 37
  _Parent = -> Constraints
FEATURE [App::FeaturePython] ElementLink061  label="_Element055"  # link proxy (typed FeaturePython)
  LinkTransform = true
  LinkedObject = -> _Element055
  _Parent = -> Constraint031
FEATURE [Part::FeaturePython] _Element055  # link proxy (typed FeaturePython)
  Detach = false
  LinkTransform = true
  LinkedObject = -> Link011 [Pad.Face13]
  _Parent = -> Elements
FEATURE [App::FeaturePython] ElementLink062  label="_Element056"  # link proxy (typed FeaturePython)
  LinkTransform = true
  LinkedObject = -> _Element056
  _Parent = -> Constraint031
FEATURE [Part::FeaturePython] _Element056  # link proxy (typed FeaturePython)
  Detach = false
  LinkTransform = true
  LinkedObject = -> Link010 [Pocket004.Face30]
  _Parent = -> Elements
FEATURE [App::FeaturePython] Constraint032  label="PlaneAlignment031"  # WARN: FeaturePython — macro-defined, semantics opaque (R4)
  Angle = 0
  AnglePitch = 0
  AngleRoll = 0
  Cascade = false
  Disabled = false
  Group = -> [ElementLink063,ElementLink064]
  LockAngle = false
  _ConstraintType = 37
  _Parent = -> Constraints
FEATURE [App::FeaturePython] ElementLink063  label="_Element057"  # link proxy (typed FeaturePython)
  LinkTransform = true
  LinkedObject = -> _Element057
  _Parent = -> Constraint032
FEATURE [Part::FeaturePython] _Element057  # link proxy (typed FeaturePython)
  Detach = false
  LinkTransform = true
  LinkedObject = -> Link010 [Pocket004.Face3]
  _Parent = -> Elements
FEATURE [App::FeaturePython] ElementLink064  label="_Element058"  # link proxy (typed FeaturePython)
  LinkTransform = true
  LinkedObject = -> _Element058
  _Parent = -> Constraint032
FEATURE [Part::FeaturePython] _Element058  # link proxy (typed FeaturePython)
  Detach = false
  LinkTransform = true
  LinkedObject = -> Link012 [LinearPattern.Face1]
  _Parent = -> Elements
FEATURE [App::FeaturePython] Constraint033  label="PlaneAlignment032"  # WARN: FeaturePython — macro-defined, semantics opaque (R4)
  Angle = 0
  AnglePitch = 0
  AngleRoll = 0
  Cascade = false
  Disabled = false
  Group = -> [ElementLink065,ElementLink066]
  LockAngle = false
  _ConstraintType = 37
  _Parent = -> Constraints
FEATURE [App::FeaturePython] ElementLink065  label="_Element059"  # link proxy (typed FeaturePython)
  LinkTransform = true
  LinkedObject = -> _Element059
  _Parent = -> Constraint033
FEATURE [Part::FeaturePython] _Element059  # link proxy (typed FeaturePython)
  Detach = false
  LinkTransform = true
  LinkedObject = -> Link012 [LinearPattern.Face2]
  _Parent = -> Elements
FEATURE [App::FeaturePython] ElementLink066  label="_Element046"  # link proxy (typed FeaturePython)
  LinkTransform = true
  LinkedObject = -> _Element046
  _Parent = -> Constraint033
FEATURE [App::FeaturePython] Constraint034  label="PlaneAlignment033"  # WARN: FeaturePython — macro-defined, semantics opaque (R4)
  Angle = 0
  AnglePitch = 0
  AngleRoll = 0
  Cascade = false
  Disabled = false
  Group = -> [ElementLink067,ElementLink068]
  LockAngle = false
  _ConstraintType = 37
  _Parent = -> Constraints
FEATURE [App::FeaturePython] ElementLink067  label="_Element060"  # link proxy (typed FeaturePython)
  LinkTransform = true
  LinkedObject = -> _Element060
  _Parent = -> Constraint034
FEATURE [Part::FeaturePython] _Element060  # link proxy (typed FeaturePython)
  Detach = false
  LinkTransform = true
  LinkedObject = -> Link010 [Pocket004.Face6]
  _Parent = -> Elements
FEATURE [App::FeaturePython] ElementLink068  label="_Element061"  # link proxy (typed FeaturePython)
  LinkTransform = true
  LinkedObject = -> _Element061
  _Parent = -> Constraint034
FEATURE [Part::FeaturePython] _Element061  # link proxy (typed FeaturePython)
  Detach = false
  LinkTransform = true
  LinkedObject = -> Link012 [LinearPattern.Face4]
  _Parent = -> Elements
FEATURE [App::FeaturePython] Constraint035  label="PlaneAlignment034"  # WARN: FeaturePython — macro-defined, semantics opaque (R4)
  Angle = 0
  AnglePitch = 0
  AngleRoll = 0
  Cascade = false
  Disabled = false
  Group = -> [ElementLink069,ElementLink070]
  LockAngle = false
  _ConstraintType = 37
  _Parent = -> Constraints
FEATURE [App::FeaturePython] ElementLink069  label="_Element062"  # link proxy (typed FeaturePython)
  LinkTransform = true
  LinkedObject = -> _Element062
  _Parent = -> Constraint035
FEATURE [Part::FeaturePython] _Element062  # link proxy (typed FeaturePython)
  Detach = false
  LinkTransform = true
  LinkedObject = -> Link013 [Pocket002.Face12]
  _Parent = -> Elements
FEATURE [App::FeaturePython] ElementLink070  label="_Element011"  # link proxy (typed FeaturePython)
  LinkTransform = true
  LinkedObject = -> _Element011
  _Parent = -> Constraint035
FEATURE [App::FeaturePython] Constraint036  label="PlaneAlignment035"  # WARN: FeaturePython — macro-defined, semantics opaque (R4)
  Angle = 0
  AnglePitch = 0
  AngleRoll = 0
  Cascade = false
  Disabled = false
  Group = -> [ElementLink071,ElementLink072]
  LockAngle = false
  _ConstraintType = 37
  _Parent = -> Constraints
FEATURE [App::FeaturePython] ElementLink071  label="_Element063"  # link proxy (typed FeaturePython)
  LinkTransform = true
  LinkedObject = -> _Element063
  _Parent = -> Constraint036
FEATURE [Part::FeaturePython] _Element063  # link proxy (typed FeaturePython)
  Detach = false
  LinkTransform = true
  LinkedObject = -> Link013 [Pocket002.Face4]
  _Parent = -> Elements
FEATURE [App::FeaturePython] ElementLink072  label="_Element003"  # link proxy (typed FeaturePython)
  LinkTransform = true
  LinkedObject = -> _Element003
  _Parent = -> Constraint036
FEATURE [App::FeaturePython] Constraint037  label="PlaneAlignment036"  # WARN: FeaturePython — macro-defined, semantics opaque (R4)
  Angle = 0
  AnglePitch = 0
  AngleRoll = 0
  Cascade = false
  Disabled = false
  Group = -> [ElementLink073,ElementLink074]
  LockAngle = false
  _ConstraintType = 37
  _Parent = -> Constraints
FEATURE [App::FeaturePython] ElementLink073  label="_Element064"  # link proxy (typed FeaturePython)
  LinkTransform = true
  LinkedObject = -> _Element064
  _Parent = -> Constraint037
FEATURE [Part::FeaturePython] _Element064  # link proxy (typed FeaturePython)
  Detach = false
  LinkTransform = true
  LinkedObject = -> Link013 [Pocket002.Face13]
  _Parent = -> Elements
FEATURE [App::FeaturePython] ElementLink074  label="_Element065"  # link proxy (typed FeaturePython)
  LinkTransform = true
  LinkedObject = -> _Element065
  _Parent = -> Constraint037
FEATURE [Part::FeaturePython] _Element065  # link proxy (typed FeaturePython)
  Detach = false
  LinkTransform = true
  LinkedObject = -> Link001 [LinearPattern.Face3]
  _Parent = -> Elements
FEATURE [Part::FeaturePython] _Element069  # link proxy (typed FeaturePython)
  Detach = false
  LinkTransform = true
  LinkedObject = -> Link012 [LinearPattern.Face3]
  _Parent = -> Elements
FEATURE [Part::FeaturePython] _Element074  # link proxy (typed FeaturePython)
  Detach = false
  LinkTransform = true
  LinkedObject = -> Link015 [Pocket003.Face5]
  _Parent = -> Elements
FEATURE [Part::FeaturePython] _Element075  # link proxy (typed FeaturePython)
  Detach = false
  LinkTransform = true
  LinkedObject = -> Link015 [Pocket003.Face14]
  _Parent = -> Elements
FEATURE [Part::FeaturePython] _Element077  # link proxy (typed FeaturePython)
  Detach = false
  LinkTransform = true
  LinkedObject = -> Link015 [Pocket003.Face6]
  _Parent = -> Elements
FEATURE [App::FeaturePython] Constraint044  label="PlaneAlignment043"  # WARN: FeaturePython — macro-defined, semantics opaque (R4)
  Angle = 0
  AnglePitch = 0
  AngleRoll = 0
  Cascade = false
  Disabled = false
  Group = -> [ElementLink087,ElementLink088]
  LockAngle = false
  _ConstraintType = 37
  _Parent = -> Constraints
FEATURE [App::FeaturePython] ElementLink087  label="_Element078"  # link proxy (typed FeaturePython)
  LinkTransform = true
  LinkedObject = -> _Element078
  _Parent = -> Constraint044
FEATURE [Part::FeaturePython] _Element078  # link proxy (typed FeaturePython)
  Detach = false
  LinkTransform = true
  LinkedObject = -> Link016 [LinearPattern.Face1]
  _Parent = -> Elements
FEATURE [App::FeaturePython] ElementLink088  label="_Element079"  # link proxy (typed FeaturePython)
  LinkTransform = true
  LinkedObject = -> _Element079
  _Parent = -> Constraint044
FEATURE [Part::FeaturePython] _Element079  # link proxy (typed FeaturePython)
  Detach = false
  LinkTransform = true
  LinkedObject = -> Link015 [Pocket003.Face10]
  _Parent = -> Elements
FEATURE [App::FeaturePython] Constraint045  label="PlaneAlignment044"  # WARN: FeaturePython — macro-defined, semantics opaque (R4)
  Angle = 0
  AnglePitch = 0
  AngleRoll = 0
  Cascade = false
  Disabled = false
  Group = -> [ElementLink089,ElementLink090]
  LockAngle = false
  _ConstraintType = 37
  _Parent = -> Constraints
FEATURE [App::FeaturePython] ElementLink089  label="_Element080"  # link proxy (typed FeaturePython)
  LinkTransform = true
  LinkedObject = -> _Element080
  _Parent = -> Constraint045
FEATURE [Part::FeaturePython] _Element080  # link proxy (typed FeaturePython)
  Detach = false
  LinkTransform = true
  LinkedObject = -> Link016 [LinearPattern.Face5]
  _Parent = -> Elements
FEATURE [App::FeaturePython] ElementLink090  label="_Element081"  # link proxy (typed FeaturePython)
  LinkTransform = true
  LinkedObject = -> _Element081
  _Parent = -> Constraint045
FEATURE [Part::FeaturePython] _Element081  # link proxy (typed FeaturePython)
  Detach = false
  LinkTransform = true
  LinkedObject = -> Link015 [Pocket003.Face11]
  _Parent = -> Elements
FEATURE [App::FeaturePython] Constraint046  label="PlaneAlignment045"  # WARN: FeaturePython — macro-defined, semantics opaque (R4)
  Angle = 0
  AnglePitch = 0
  AngleRoll = 0
  Cascade = false
  Disabled = false
  Group = -> [ElementLink091,ElementLink092]
  LockAngle = false
  _ConstraintType = 37
  _Parent = -> Constraints
FEATURE [App::FeaturePython] ElementLink091  label="_Element082"  # link proxy (typed FeaturePython)
  LinkTransform = true
  LinkedObject = -> _Element082
  _Parent = -> Constraint046
FEATURE [Part::FeaturePython] _Element082  # link proxy (typed FeaturePython)
  Detach = false
  LinkTransform = true
  LinkedObject = -> Link016 [LinearPattern.Face2]
  _Parent = -> Elements
FEATURE [App::FeaturePython] ElementLink092  label="_Element028"  # link proxy (typed FeaturePython)
  LinkTransform = true
  LinkedObject = -> _Element028
  _Parent = -> Constraint046
FEATURE [App::FeaturePython] Constraint047  label="PlaneAlignment046"  # WARN: FeaturePython — macro-defined, semantics opaque (R4)
  Angle = 0
  AnglePitch = 0
  AngleRoll = 0
  Cascade = false
  Disabled = false
  Group = -> [ElementLink093,ElementLink094]
  LockAngle = false
  _ConstraintType = 37
  _Parent = -> Constraints
FEATURE [App::FeaturePython] ElementLink093  label="_Element083"  # link proxy (typed FeaturePython)
  LinkTransform = true
  LinkedObject = -> _Element083
  _Parent = -> Constraint047
FEATURE [Part::FeaturePython] _Element083  # link proxy (typed FeaturePython)
  Detach = false
  LinkTransform = true
  LinkedObject = -> Link017 [Pocket005.Face3]
  _Parent = -> Elements
FEATURE [App::FeaturePython] ElementLink094  label="_Element078"  # link proxy (typed FeaturePython)
  LinkTransform = true
  LinkedObject = -> _Element078
  _Parent = -> Constraint047
FEATURE [App::FeaturePython] Constraint048  label="PlaneAlignment047"  # WARN: FeaturePython — macro-defined, semantics opaque (R4)
  Angle = 0
  AnglePitch = 0
  AngleRoll = 0
  Cascade = false
  Disabled = false
  Group = -> [ElementLink095,ElementLink096]
  LockAngle = false
  _ConstraintType = 37
  _Parent = -> Constraints
FEATURE [App::FeaturePython] ElementLink095  label="_Element084"  # link proxy (typed FeaturePython)
  LinkTransform = true
  LinkedObject = -> _Element084
  _Parent = -> Constraint048
FEATURE [Part::FeaturePython] _Element084  # link proxy (typed FeaturePython)
  Detach = false
  LinkTransform = true
  LinkedObject = -> Link017 [Pocket005.Face2]
  _Parent = -> Elements
FEATURE [App::FeaturePython] ElementLink096  label="_Element082"  # link proxy (typed FeaturePython)
  LinkTransform = true
  LinkedObject = -> _Element082
  _Parent = -> Constraint048
FEATURE [App::FeaturePython] Constraint049  label="PlaneAlignment048"  # WARN: FeaturePython — macro-defined, semantics opaque (R4)
  Angle = 0
  AnglePitch = 0
  AngleRoll = 0
  Cascade = false
  Disabled = false
  Group = -> [ElementLink097,ElementLink098]
  LockAngle = false
  _ConstraintType = 37
  _Parent = -> Constraints
FEATURE [App::FeaturePython] ElementLink097  label="_Element085"  # link proxy (typed FeaturePython)
  LinkTransform = true
  LinkedObject = -> _Element085
  _Parent = -> Constraint049
FEATURE [Part::FeaturePython] _Element085  # link proxy (typed FeaturePython)
  Detach = false
  LinkTransform = true
  LinkedObject = -> Link017 [Pocket005.Face6]
  _Parent = -> Elements
FEATURE [App::FeaturePython] ElementLink098  label="_Element086"  # link proxy (typed FeaturePython)
  LinkTransform = true
  LinkedObject = -> _Element086
  _Parent = -> Constraint049
FEATURE [Part::FeaturePython] _Element086  # link proxy (typed FeaturePython)
  Detach = false
  LinkTransform = true
  LinkedObject = -> Link016 [LinearPattern.Face4]
  _Parent = -> Elements
FEATURE [App::FeaturePython] Constraint050  label="PlaneAlignment049"  # WARN: FeaturePython — macro-defined, semantics opaque (R4)
  Angle = 0
  AnglePitch = 0
  AngleRoll = 0
  Cascade = false
  Disabled = false
  Group = -> [ElementLink099,ElementLink100]
  LockAngle = false
  _ConstraintType = 37
  _Parent = -> Constraints
FEATURE [App::FeaturePython] ElementLink099  label="_Element087"  # link proxy (typed FeaturePython)
  LinkTransform = true
  LinkedObject = -> _Element087
  _Parent = -> Constraint050
FEATURE [Part::FeaturePython] _Element087  # link proxy (typed FeaturePython)
  Detach = false
  LinkTransform = true
  LinkedObject = -> Link018 [Pocket003.Face6]
  _Parent = -> Elements
FEATURE [App::FeaturePython] ElementLink100  label="_Element084"  # link proxy (typed FeaturePython)
  LinkTransform = true
  LinkedObject = -> _Element084
  _Parent = -> Constraint050
FEATURE [App::FeaturePython] Constraint051  label="PlaneAlignment050"  # WARN: FeaturePython — macro-defined, semantics opaque (R4)
  Angle = 0
  AnglePitch = 0
  AngleRoll = 0
  Cascade = false
  Disabled = false
  Group = -> [ElementLink101,ElementLink102]
  LockAngle = false
  _ConstraintType = 37
  _Parent = -> Constraints
FEATURE [App::FeaturePython] ElementLink101  label="_Element088"  # link proxy (typed FeaturePython)
  LinkTransform = true
  LinkedObject = -> _Element088
  _Parent = -> Constraint051
FEATURE [Part::FeaturePython] _Element088  # link proxy (typed FeaturePython)
  Detach = false
  LinkTransform = true
  LinkedObject = -> Link017 [Pocket005.Face5]
  _Parent = -> Elements
FEATURE [App::FeaturePython] ElementLink102  label="_Element089"  # link proxy (typed FeaturePython)
  LinkTransform = true
  LinkedObject = -> _Element089
  _Parent = -> Constraint051
FEATURE [Part::FeaturePython] _Element089  # link proxy (typed FeaturePython)
  Detach = false
  LinkTransform = true
  LinkedObject = -> Link018 [Pocket003.Face5]
  _Parent = -> Elements
FEATURE [App::FeaturePython] Constraint052  label="PlaneAlignment051"  # WARN: FeaturePython — macro-defined, semantics opaque (R4)
  Angle = 0
  AnglePitch = 0
  AngleRoll = 0
  Cascade = false
  Disabled = false
  Group = -> [ElementLink103,ElementLink104]
  LockAngle = false
  _ConstraintType = 37
  _Parent = -> Constraints
FEATURE [App::FeaturePython] ElementLink103  label="_Element090"  # link proxy (typed FeaturePython)
  LinkTransform = true
  LinkedObject = -> _Element090
  _Parent = -> Constraint052
FEATURE [Part::FeaturePython] _Element090  # link proxy (typed FeaturePython)
  Detach = false
  LinkTransform = true
  LinkedObject = -> Link018 [Pocket003.Face14]
  _Parent = -> Elements
FEATURE [App::FeaturePython] ElementLink104  label="_Element091"  # link proxy (typed FeaturePython)
  LinkTransform = true
  LinkedObject = -> _Element091
  _Parent = -> Constraint052
FEATURE [Part::FeaturePython] _Element091  # link proxy (typed FeaturePython)
  Detach = false
  LinkTransform = true
  LinkedObject = -> Link017 [Pocket005.Face10]
  _Parent = -> Elements
FEATURE [App::FeaturePython] Constraint053  label="PlaneAlignment052"  # WARN: FeaturePython — macro-defined, semantics opaque (R4)
  Angle = 0
  AnglePitch = 0
  AngleRoll = 0
  Cascade = false
  Disabled = false
  Group = -> [ElementLink105,ElementLink106]
  LockAngle = false
  _ConstraintType = 37
  _Parent = -> Constraints
FEATURE [App::FeaturePython] ElementLink105  label="_Element092"  # link proxy (typed FeaturePython)
  LinkTransform = true
  LinkedObject = -> _Element092
  _Parent = -> Constraint053
FEATURE [Part::FeaturePython] _Element092  # link proxy (typed FeaturePython)
  Detach = false
  LinkTransform = true
  LinkedObject = -> Link019 [LinearPattern.Face5]
  _Parent = -> Elements
FEATURE [App::FeaturePython] ElementLink106  label="_Element093"  # link proxy (typed FeaturePython)
  LinkTransform = true
  LinkedObject = -> _Element093
  _Parent = -> Constraint053
FEATURE [Part::FeaturePython] _Element093  # link proxy (typed FeaturePython)
  Detach = false
  LinkTransform = true
  LinkedObject = -> Link018 [Pocket003.Face11]
  _Parent = -> Elements
FEATURE [App::FeaturePython] Constraint054  label="PlaneAlignment053"  # WARN: FeaturePython — macro-defined, semantics opaque (R4)
  Angle = 0
  AnglePitch = 0
  AngleRoll = 0
  Cascade = false
  Disabled = false
  Group = -> [ElementLink107,ElementLink108]
  LockAngle = false
  _ConstraintType = 37
  _Parent = -> Constraints
FEATURE [App::FeaturePython] ElementLink107  label="_Element094"  # link proxy (typed FeaturePython)
  LinkTransform = true
  LinkedObject = -> _Element094
  _Parent = -> Constraint054
FEATURE [Part::FeaturePython] _Element094  # link proxy (typed FeaturePython)
  Detach = false
  LinkTransform = true
  LinkedObject = -> Link019 [LinearPattern.Face6]
  _Parent = -> Elements
FEATURE [App::FeaturePython] ElementLink108  label="_Element095"  # link proxy (typed FeaturePython)
  LinkTransform = true
  LinkedObject = -> _Element095
  _Parent = -> Constraint054
FEATURE [Part::FeaturePython] _Element095  # link proxy (typed FeaturePython)
  Detach = false
  LinkTransform = true
  LinkedObject = -> Link018 [Pocket003.Face12]
  _Parent = -> Elements
FEATURE [App::FeaturePython] Constraint055  label="PlaneAlignment054"  # WARN: FeaturePython — macro-defined, semantics opaque (R4)
  Angle = 0
  AnglePitch = 0
  AngleRoll = 0
  Cascade = false
  Disabled = false
  Group = -> [ElementLink109,ElementLink110]
  LockAngle = false
  _ConstraintType = 37
  _Parent = -> Constraints
FEATURE [App::FeaturePython] ElementLink109  label="_Element096"  # link proxy (typed FeaturePython)
  LinkTransform = true
  LinkedObject = -> _Element096
  _Parent = -> Constraint055
FEATURE [Part::FeaturePython] _Element096  # link proxy (typed FeaturePython)
  Detach = false
  LinkTransform = true
  LinkedObject = -> Link021 [Pocket001.Face24]
  _Parent = -> Elements
FEATURE [App::FeaturePython] ElementLink110  label="_Element097"  # link proxy (typed FeaturePython)
  LinkTransform = true
  LinkedObject = -> _Element097
  _Parent = -> Constraint055
FEATURE [Part::FeaturePython] _Element097  # link proxy (typed FeaturePython)
  Detach = false
  LinkTransform = true
  LinkedObject = -> Link019 [LinearPattern.Face4]
  _Parent = -> Elements
FEATURE [App::FeaturePython] Constraint056  label="PlaneAlignment055"  # WARN: FeaturePython — macro-defined, semantics opaque (R4)
  Angle = 0
  AnglePitch = 0
  AngleRoll = 0
  Cascade = false
  Disabled = false
  Group = -> [ElementLink111,ElementLink112]
  LockAngle = false
  _ConstraintType = 37
  _Parent = -> Constraints
FEATURE [App::FeaturePython] ElementLink111  label="_Element098"  # link proxy (typed FeaturePython)
  LinkTransform = true
  LinkedObject = -> _Element098
  _Parent = -> Constraint056
FEATURE [Part::FeaturePython] _Element098  # link proxy (typed FeaturePython)
  Detach = false
  LinkTransform = true
  LinkedObject = -> Link021 [Pocket001.Face30]
  _Parent = -> Elements
FEATURE [App::FeaturePython] ElementLink112  label="_Element099"  # link proxy (typed FeaturePython)
  LinkTransform = true
  LinkedObject = -> _Element099
  _Parent = -> Constraint056
FEATURE [Part::FeaturePython] _Element099  # link proxy (typed FeaturePython)
  Detach = false
  LinkTransform = true
  LinkedObject = -> Link019 [LinearPattern.Face1]
  _Parent = -> Elements
FEATURE [App::FeaturePython] Constraint057  label="PlaneAlignment056"  # WARN: FeaturePython — macro-defined, semantics opaque (R4)
  Angle = 0
  AnglePitch = 0
  AngleRoll = 0
  Cascade = false
  Disabled = false
  Group = -> [ElementLink113,ElementLink114]
  LockAngle = false
  _ConstraintType = 37
  _Parent = -> Constraints
FEATURE [App::FeaturePython] ElementLink113  label="_Element100"  # link proxy (typed FeaturePython)
  LinkTransform = true
  LinkedObject = -> _Element100
  _Parent = -> Constraint057
FEATURE [Part::FeaturePython] _Element100  # link proxy (typed FeaturePython)
  Detach = false
  LinkTransform = true
  LinkedObject = -> Link021 [Pocket001.Face32]
  _Parent = -> Elements
FEATURE [App::FeaturePython] ElementLink114  label="_Element101"  # link proxy (typed FeaturePython)
  LinkTransform = true
  LinkedObject = -> _Element101
  _Parent = -> Constraint057
FEATURE [Part::FeaturePython] _Element101  # link proxy (typed FeaturePython)
  Detach = false
  LinkTransform = true
  LinkedObject = -> Link019 [LinearPattern.Face2]
  _Parent = -> Elements
FEATURE [App::FeaturePython] Constraint058  label="PlaneAlignment057"  # WARN: FeaturePython — macro-defined, semantics opaque (R4)
  Angle = 0
  AnglePitch = 0
  AngleRoll = 0
  Cascade = false
  Disabled = false
  Group = -> [ElementLink115,ElementLink116]
  LockAngle = false
  _ConstraintType = 37
  _Parent = -> Constraints
FEATURE [App::FeaturePython] ElementLink115  label="_Element102"  # link proxy (typed FeaturePython)
  LinkTransform = true
  LinkedObject = -> _Element102
  _Parent = -> Constraint058
FEATURE [Part::FeaturePython] _Element102  # link proxy (typed FeaturePython)
  Detach = false
  LinkTransform = true
  LinkedObject = -> Link020 [Pocket004.Face4]
  _Parent = -> Elements
FEATURE [App::FeaturePython] ElementLink116  label="_Element097"  # link proxy (typed FeaturePython)
  LinkTransform = true
  LinkedObject = -> _Element097
  _Parent = -> Constraint058
FEATURE [App::FeaturePython] Constraint059  label="PlaneAlignment058"  # WARN: FeaturePython — macro-defined, semantics opaque (R4)
  Angle = 0
  AnglePitch = 0
  AngleRoll = 0
  Cascade = false
  Disabled = false
  Group = -> [ElementLink117,ElementLink118]
  LockAngle = false
  _ConstraintType = 37
  _Parent = -> Constraints
FEATURE [App::FeaturePython] ElementLink117  label="_Element103"  # link proxy (typed FeaturePython)
  LinkTransform = true
  LinkedObject = -> _Element103
  _Parent = -> Constraint059
FEATURE [Part::FeaturePython] _Element103  # link proxy (typed FeaturePython)
  Detach = false
  LinkTransform = true
  LinkedObject = -> Link020 [Pocket004.Face26]
  _Parent = -> Elements
FEATURE [App::FeaturePython] ElementLink118  label="_Element094"  # link proxy (typed FeaturePython)
  LinkTransform = true
  LinkedObject = -> _Element094
  _Parent = -> Constraint059
FEATURE [App::FeaturePython] Constraint060  label="PlaneAlignment059"  # WARN: FeaturePython — macro-defined, semantics opaque (R4)
  Angle = 0
  AnglePitch = 0
  AngleRoll = 0
  Cascade = false
  Disabled = false
  Group = -> [ElementLink119,ElementLink120]
  LockAngle = false
  _ConstraintType = 37
  _Parent = -> Constraints
FEATURE [App::FeaturePython] ElementLink119  label="_Element104"  # link proxy (typed FeaturePython)
  LinkTransform = true
  LinkedObject = -> _Element104
  _Parent = -> Constraint060
FEATURE [Part::FeaturePython] _Element104  # link proxy (typed FeaturePython)
  Detach = false
  LinkTransform = true
  LinkedObject = -> Link020 [Pocket004.Face27]
  _Parent = -> Elements
FEATURE [App::FeaturePython] ElementLink120  label="_Element105"  # link proxy (typed FeaturePython)
  LinkTransform = true
  LinkedObject = -> _Element105
  _Parent = -> Constraint060
FEATURE [Part::FeaturePython] _Element105  # link proxy (typed FeaturePython)
  Detach = false
  LinkTransform = true
  LinkedObject = -> Link019 [LinearPattern.Face3]
  _Parent = -> Elements
FEATURE [App::FeaturePython] Constraint061  label="PlaneAlignment060"  # WARN: FeaturePython — macro-defined, semantics opaque (R4)
  Angle = 0
  AnglePitch = 0
  AngleRoll = 0
  Cascade = false
  Disabled = false
  Group = -> [ElementLink121,ElementLink122]
  LockAngle = false
  _ConstraintType = 37
  _Parent = -> Constraints
FEATURE [App::FeaturePython] ElementLink121  label="_Element106"  # link proxy (typed FeaturePython)
  LinkTransform = true
  LinkedObject = -> _Element106
  _Parent = -> Constraint061
FEATURE [Part::FeaturePython] _Element106  # link proxy (typed FeaturePython)
  Detach = false
  LinkTransform = true
  LinkedObject = -> Link021 [Pocket001.Face26]
  _Parent = -> Elements
FEATURE [App::FeaturePython] ElementLink122  label="_Element107"  # link proxy (typed FeaturePython)
  LinkTransform = true
  LinkedObject = -> _Element107
  _Parent = -> Constraint061
FEATURE [Part::FeaturePython] _Element107  # link proxy (typed FeaturePython)
  Detach = false
  LinkTransform = true
  LinkedObject = -> Link [Pocket001.Face26]
  _Parent = -> Elements
FEATURE [App::FeaturePython] Constraint062  label="PlaneAlignment061"  # WARN: FeaturePython — macro-defined, semantics opaque (R4)
  Angle = 0
  AnglePitch = 0
  AngleRoll = 0
  Cascade = false
  Disabled = false
  Group = -> [ElementLink123,ElementLink124]
  LockAngle = false
  _ConstraintType = 37
  _Parent = -> Constraints
FEATURE [App::FeaturePython] ElementLink123  label="_Element108"  # link proxy (typed FeaturePython)
  LinkTransform = true
  LinkedObject = -> _Element108
  _Parent = -> Constraint062
FEATURE [Part::FeaturePython] _Element108  # link proxy (typed FeaturePython)
  Detach = false
  LinkTransform = true
  LinkedObject = -> Link009 [Pocket003.Face3]
  _Parent = -> Elements
FEATURE [App::FeaturePython] ElementLink124  label="_Element109"  # link proxy (typed FeaturePython)
  LinkTransform = true
  LinkedObject = -> _Element109
  _Parent = -> Constraint062
FEATURE [Part::FeaturePython] _Element109  # link proxy (typed FeaturePython)
  Detach = false
  LinkTransform = true
  LinkedObject = -> Link015 [Pocket003.Face3]
  _Parent = -> Elements
FEATURE [App::FeaturePython] Constraint063  label="PlaneAlignment062"  # WARN: FeaturePython — macro-defined, semantics opaque (R4)
  Angle = 0
  AnglePitch = 0
  AngleRoll = 0
  Cascade = false
  Disabled = false
  Group = -> [ElementLink125,ElementLink126]
  LockAngle = false
  _ConstraintType = 37
  _Parent = -> Constraints
FEATURE [App::FeaturePython] ElementLink125  label="_Element110"  # link proxy (typed FeaturePython)
  LinkTransform = true
  LinkedObject = -> _Element110
  _Parent = -> Constraint063
FEATURE [Part::FeaturePython] _Element110  # link proxy (typed FeaturePython)
  Detach = false
  LinkTransform = true
  LinkedObject = -> Link015 [Pocket003.Face1]
  _Parent = -> Elements
FEATURE [App::FeaturePython] ElementLink126  label="_Element111"  # link proxy (typed FeaturePython)
  LinkTransform = true
  LinkedObject = -> _Element111
  _Parent = -> Constraint063
FEATURE [Part::FeaturePython] _Element111  # link proxy (typed FeaturePython)
  Detach = false
  LinkTransform = true
  LinkedObject = -> Link009 [Pocket003.Face14]
  _Parent = -> Elements
FEATURE [App::FeaturePython] Constraint064  label="PlaneAlignment063"  # WARN: FeaturePython — macro-defined, semantics opaque (R4)
  Angle = 0
  AnglePitch = 0
  AngleRoll = 0
  Cascade = false
  Disabled = false
  Group = -> [ElementLink127,ElementLink128]
  LockAngle = false
  _ConstraintType = 37
  _Parent = -> Constraints
FEATURE [App::FeaturePython] ElementLink127  label="_Element112"  # link proxy (typed FeaturePython)
  LinkTransform = true
  LinkedObject = -> _Element112
  _Parent = -> Constraint064
FEATURE [Part::FeaturePython] _Element112  # link proxy (typed FeaturePython)
  Detach = false
  LinkTransform = true
  LinkedObject = -> Link022 [Pocket019.Face14]
  _Parent = -> Elements
FEATURE [App::FeaturePython] ElementLink128  label="_Element061"  # link proxy (typed FeaturePython)
  LinkTransform = true
  LinkedObject = -> _Element061
  _Parent = -> Constraint064
FEATURE [App::FeaturePython] Constraint065  label="PlaneAlignment064"  # WARN: FeaturePython — macro-defined, semantics opaque (R4)
  Angle = 0
  AnglePitch = 0
  AngleRoll = 0
  Cascade = false
  Disabled = false
  Group = -> [ElementLink129,ElementLink130]
  LockAngle = false
  _ConstraintType = 37
  _Parent = -> Constraints
FEATURE [App::FeaturePython] ElementLink129  label="_Element113"  # link proxy (typed FeaturePython)
  LinkTransform = true
  LinkedObject = -> _Element113
  _Parent = -> Constraint065
FEATURE [Part::FeaturePython] _Element113  # link proxy (typed FeaturePython)
  Detach = false
  LinkTransform = true
  LinkedObject = -> Link022 [Pocket019.Face2]
  _Parent = -> Elements
FEATURE [App::FeaturePython] ElementLink130  label="_Element069"  # link proxy (typed FeaturePython)
  LinkTransform = true
  LinkedObject = -> _Element069
  _Parent = -> Constraint065
FEATURE [App::FeaturePython] Constraint066  label="PlaneAlignment065"  # WARN: FeaturePython — macro-defined, semantics opaque (R4)
  Angle = 0
  AnglePitch = 0
  AngleRoll = 0
  Cascade = false
  Disabled = false
  Group = -> [ElementLink131,ElementLink132]
  LockAngle = false
  _ConstraintType = 37
  _Parent = -> Constraints
FEATURE [App::FeaturePython] ElementLink131  label="_Element113"  # link proxy (typed FeaturePython)
  LinkTransform = true
  LinkedObject = -> _Element113
  _Parent = -> Constraint066
FEATURE [App::FeaturePython] ElementLink132  label="_Element077"  # link proxy (typed FeaturePython)
  LinkTransform = true
  LinkedObject = -> _Element077
  _Parent = -> Constraint066
FEATURE [App::FeaturePython] Constraint067  label="PlaneAlignment066"  # WARN: FeaturePython — macro-defined, semantics opaque (R4)
  Angle = 0
  AnglePitch = 0
  AngleRoll = 0
  Cascade = false
  Disabled = false
  Group = -> [ElementLink133,ElementLink134]
  LockAngle = false
  _ConstraintType = 37
  _Parent = -> Constraints
FEATURE [App::FeaturePython] ElementLink133  label="_Element114"  # link proxy (typed FeaturePython)
  LinkTransform = true
  LinkedObject = -> _Element114
  _Parent = -> Constraint067
FEATURE [Part::FeaturePython] _Element114  # link proxy (typed FeaturePython)
  Detach = false
  LinkTransform = true
  LinkedObject = -> Link022 [Pocket019.Face26]
  _Parent = -> Elements
FEATURE [App::FeaturePython] ElementLink134  label="_Element058"  # link proxy (typed FeaturePython)
  LinkTransform = true
  LinkedObject = -> _Element058
  _Parent = -> Constraint067
FEATURE [App::FeaturePython] Constraint068  label="PlaneAlignment067"  # WARN: FeaturePython — macro-defined, semantics opaque (R4)
  Angle = 0
  AnglePitch = 0
  AngleRoll = 0
  Cascade = false
  Disabled = false
  Group = -> [ElementLink135,ElementLink136]
  LockAngle = false
  _ConstraintType = 37
  _Parent = -> Constraints
FEATURE [App::FeaturePython] ElementLink135  label="_Element115"  # link proxy (typed FeaturePython)
  LinkTransform = true
  LinkedObject = -> _Element115
  _Parent = -> Constraint068
FEATURE [Part::FeaturePython] _Element115  # link proxy (typed FeaturePython)
  Detach = false
  LinkTransform = true
  LinkedObject = -> Link022 [Pocket019.Face11]
  _Parent = -> Elements
FEATURE [App::FeaturePython] ElementLink136  label="_Element074"  # link proxy (typed FeaturePython)
  LinkTransform = true
  LinkedObject = -> _Element074
  _Parent = -> Constraint068
FEATURE [App::FeaturePython] Constraint069  label="PlaneAlignment068"  # WARN: FeaturePython — macro-defined, semantics opaque (R4)
  Angle = 0
  AnglePitch = 0
  AngleRoll = 0
  Cascade = false
  Disabled = false
  Group = -> [ElementLink137,ElementLink138]
  LockAngle = false
  _ConstraintType = 37
  _Parent = -> Constraints
FEATURE [App::FeaturePython] ElementLink137  label="_Element116"  # link proxy (typed FeaturePython)
  LinkTransform = true
  LinkedObject = -> _Element116
  _Parent = -> Constraint069
FEATURE [Part::FeaturePython] _Element116  # link proxy (typed FeaturePython)
  Detach = false
  LinkTransform = true
  LinkedObject = -> Link022 [Pocket019.Face1]
  _Parent = -> Elements
FEATURE [App::FeaturePython] ElementLink138  label="_Element110"  # link proxy (typed FeaturePython)
  LinkTransform = true
  LinkedObject = -> _Element110
  _Parent = -> Constraint069
FEATURE [App::FeaturePython] Constraint070  label="PlaneAlignment069"  # WARN: FeaturePython — macro-defined, semantics opaque (R4)
  Angle = 0
  AnglePitch = 0
  AngleRoll = 0
  Cascade = false
  Disabled = false
  Group = -> [ElementLink139,ElementLink140]
  LockAngle = false
  _ConstraintType = 37
  _Parent = -> Constraints
FEATURE [App::FeaturePython] ElementLink139  label="_Element117"  # link proxy (typed FeaturePython)
  LinkTransform = true
  LinkedObject = -> _Element117
  _Parent = -> Constraint070
FEATURE [Part::FeaturePython] _Element117  # link proxy (typed FeaturePython)
  Detach = false
  LinkTransform = true
  LinkedObject = -> Link023 [Pocket003.Face10]
  _Parent = -> Elements
FEATURE [App::FeaturePython] ElementLink140  label="_Element118"  # link proxy (typed FeaturePython)
  LinkTransform = true
  LinkedObject = -> _Element118
  _Parent = -> Constraint070
FEATURE [Part::FeaturePython] _Element118  # link proxy (typed FeaturePython)
  Detach = false
  LinkTransform = true
  LinkedObject = -> Link012 [LinearPattern.Face6]
  _Parent = -> Elements
FEATURE [App::FeaturePython] Constraint071  label="PlaneAlignment070"  # WARN: FeaturePython — macro-defined, semantics opaque (R4)
  Angle = 0
  AnglePitch = 0
  AngleRoll = 0
  Cascade = false
  Disabled = false
  Group = -> [ElementLink141,ElementLink142]
  LockAngle = false
  _ConstraintType = 37
  _Parent = -> Constraints
FEATURE [App::FeaturePython] ElementLink141  label="_Element119"  # link proxy (typed FeaturePython)
  LinkTransform = true
  LinkedObject = -> _Element119
  _Parent = -> Constraint071
FEATURE [Part::FeaturePython] _Element119  # link proxy (typed FeaturePython)
  Detach = false
  LinkTransform = true
  LinkedObject = -> Link023 [Pocket003.Face11]
  _Parent = -> Elements
FEATURE [App::FeaturePython] ElementLink142  label="_Element120"  # link proxy (typed FeaturePython)
  LinkTransform = true
  LinkedObject = -> _Element120
  _Parent = -> Constraint071
FEATURE [Part::FeaturePython] _Element120  # link proxy (typed FeaturePython)
  Detach = false
  LinkTransform = true
  LinkedObject = -> Link012 [LinearPattern.Face5]
  _Parent = -> Elements
FEATURE [App::FeaturePython] Constraint072  label="PlaneAlignment071"  # WARN: FeaturePython — macro-defined, semantics opaque (R4)
  Angle = 0
  AnglePitch = 0
  AngleRoll = 0
  Cascade = false
  Disabled = false
  Group = -> [ElementLink143,ElementLink144]
  LockAngle = false
  _ConstraintType = 37
  _Parent = -> Constraints
FEATURE [App::FeaturePython] ElementLink143  label="_Element121"  # link proxy (typed FeaturePython)
  LinkTransform = true
  LinkedObject = -> _Element121
  _Parent = -> Constraint072
FEATURE [Part::FeaturePython] _Element121  # link proxy (typed FeaturePython)
  Detach = false
  LinkTransform = true
  LinkedObject = -> Link024 [Pocket.Face20]
  _Parent = -> Elements
FEATURE [App::FeaturePython] ElementLink144  label="_Element122"  # link proxy (typed FeaturePython)
  LinkTransform = true
  LinkedObject = -> _Element122
  _Parent = -> Constraint072
FEATURE [Part::FeaturePython] _Element122  # link proxy (typed FeaturePython)
  Detach = false
  LinkTransform = true
  LinkedObject = -> Link023 [Pocket003.Face6]
  _Parent = -> Elements
FEATURE [App::FeaturePython] Constraint073  label="PlaneAlignment072"  # WARN: FeaturePython — macro-defined, semantics opaque (R4)
  Angle = 0
  AnglePitch = 0
  AngleRoll = 0
  Cascade = false
  Disabled = false
  Group = -> [ElementLink145,ElementLink146]
  LockAngle = false
  _ConstraintType = 37
  _Parent = -> Constraints
FEATURE [App::FeaturePython] ElementLink145  label="_Element123"  # link proxy (typed FeaturePython)
  LinkTransform = true
  LinkedObject = -> _Element123
  _Parent = -> Constraint073
FEATURE [Part::FeaturePython] _Element123  # link proxy (typed FeaturePython)
  Detach = false
  LinkTransform = true
  LinkedObject = -> Link024 [Pocket.Face11]
  _Parent = -> Elements
FEATURE [App::FeaturePython] ElementLink146  label="_Element124"  # link proxy (typed FeaturePython)
  LinkTransform = true
  LinkedObject = -> _Element124
  _Parent = -> Constraint073
FEATURE [Part::FeaturePython] _Element124  # link proxy (typed FeaturePython)
  Detach = false
  LinkTransform = true
  LinkedObject = -> Link023 [Pocket003.Face5]
  _Parent = -> Elements
FEATURE [App::FeaturePython] Constraint074  label="PlaneAlignment073"  # WARN: FeaturePython — macro-defined, semantics opaque (R4)
  Angle = 0
  AnglePitch = 0
  AngleRoll = 0
  Cascade = false
  Disabled = false
  Group = -> [ElementLink147,ElementLink148]
  LockAngle = false
  _ConstraintType = 37
  _Parent = -> Constraints
FEATURE [App::FeaturePython] ElementLink147  label="_Element125"  # link proxy (typed FeaturePython)
  LinkTransform = true
  LinkedObject = -> _Element125
  _Parent = -> Constraint074
FEATURE [Part::FeaturePython] _Element125  # link proxy (typed FeaturePython)
  Detach = false
  LinkTransform = true
  LinkedObject = -> Link024 [Pocket.Face22]
  _Parent = -> Elements
FEATURE [App::FeaturePython] ElementLink148  label="_Element126"  # link proxy (typed FeaturePython)
  LinkTransform = true
  LinkedObject = -> _Element126
  _Parent = -> Constraint074
FEATURE [Part::FeaturePython] _Element126  # link proxy (typed FeaturePython)
  Detach = false
  LinkTransform = true
  LinkedObject = -> Link023 [Pocket003.Face1]
  _Parent = -> Elements
FEATURE [App::FeaturePython] Constraint075  label="PlaneAlignment074"  # WARN: FeaturePython — macro-defined, semantics opaque (R4)
  Angle = 0
  AnglePitch = 0
  AngleRoll = 0
  Cascade = false
  Disabled = false
  Group = -> [ElementLink149,ElementLink150]
  LockAngle = false
  _ConstraintType = 37
  _Parent = -> Constraints
FEATURE [App::FeaturePython] ElementLink149  label="_Element127"  # link proxy (typed FeaturePython)
  LinkTransform = true
  LinkedObject = -> _Element127
  _Parent = -> Constraint075
FEATURE [Part::FeaturePython] _Element127  # link proxy (typed FeaturePython)
  Detach = false
  LinkTransform = true
  LinkedObject = -> Link025 [Face5]
  _Parent = -> Elements
FEATURE [App::FeaturePython] ElementLink150  label="_Element128"  # link proxy (typed FeaturePython)
  LinkTransform = true
  LinkedObject = -> _Element128
  _Parent = -> Constraint075
FEATURE [Part::FeaturePython] _Element128  # link proxy (typed FeaturePython)
  Detach = false
  LinkTransform = true
  LinkedObject = -> Link024 [Pocket.Face4]
  _Parent = -> Elements
FEATURE [App::FeaturePython] Constraint076  label="PlaneAlignment075"  # WARN: FeaturePython — macro-defined, semantics opaque (R4)
  Angle = 0
  AnglePitch = 0
  AngleRoll = 0
  Cascade = false
  Disabled = false
  Group = -> [ElementLink151,ElementLink152]
  LockAngle = false
  _ConstraintType = 37
  _Parent = -> Constraints
FEATURE [App::FeaturePython] ElementLink151  label="_Element129"  # link proxy (typed FeaturePython)
  LinkTransform = true
  LinkedObject = -> _Element129
  _Parent = -> Constraint076
FEATURE [Part::FeaturePython] _Element129  # link proxy (typed FeaturePython)
  Detach = false
  LinkTransform = true
  LinkedObject = -> Link025 [Face11]
  _Parent = -> Elements
FEATURE [App::FeaturePython] ElementLink152  label="_Element130"  # link proxy (typed FeaturePython)
  LinkTransform = true
  LinkedObject = -> _Element130
  _Parent = -> Constraint076
FEATURE [Part::FeaturePython] _Element130  # link proxy (typed FeaturePython)
  Detach = false
  LinkTransform = true
  LinkedObject = -> Link024 [Pocket.Face10]
  _Parent = -> Elements
FEATURE [App::FeaturePython] Constraint077  label="PlaneAlignment076"  # WARN: FeaturePython — macro-defined, semantics opaque (R4)
  Angle = 0
  AnglePitch = 0
  AngleRoll = 0
  Cascade = false
  Disabled = false
  Group = -> [ElementLink153,ElementLink154]
  LockAngle = false
  _ConstraintType = 37
  _Parent = -> Constraints
FEATURE [App::FeaturePython] ElementLink153  label="_Element131"  # link proxy (typed FeaturePython)
  LinkTransform = true
  LinkedObject = -> _Element131
  _Parent = -> Constraint077
FEATURE [Part::FeaturePython] _Element131  # link proxy (typed FeaturePython)
  Detach = false
  LinkTransform = true
  LinkedObject = -> Link024 [Pad001.Face20]
  _Parent = -> Elements
FEATURE [App::FeaturePython] ElementLink154  label="_Element122"  # link proxy (typed FeaturePython)
  LinkTransform = true
  LinkedObject = -> _Element122
  _Parent = -> Constraint077
FEATURE [App::FeaturePython] Constraint078  label="PlaneAlignment077"  # WARN: FeaturePython — macro-defined, semantics opaque (R4)
  Angle = 0
  AnglePitch = 0
  AngleRoll = 0
  Cascade = false
  Disabled = false
  Group = -> [ElementLink155,ElementLink156]
  LockAngle = false
  _ConstraintType = 37
  _Parent = -> Constraints
FEATURE [App::FeaturePython] ElementLink155  label="_Element132"  # link proxy (typed FeaturePython)
  LinkTransform = true
  LinkedObject = -> _Element132
  _Parent = -> Constraint078
FEATURE [Part::FeaturePython] _Element132  # link proxy (typed FeaturePython)
  Detach = false
  LinkTransform = true
  LinkedObject = -> Link024 [Pad001.Face21]
  _Parent = -> Elements
FEATURE [App::FeaturePython] ElementLink156  label="_Element126"  # link proxy (typed FeaturePython)
  LinkTransform = true
  LinkedObject = -> _Element126
  _Parent = -> Constraint078
FEATURE [App::FeaturePython] Constraint079  label="PlaneAlignment078"  # WARN: FeaturePython — macro-defined, semantics opaque (R4)
  Angle = 0
  AnglePitch = 0
  AngleRoll = 0
  Cascade = false
  Disabled = false
  Group = -> [ElementLink157,ElementLink158]
  LockAngle = false
  _ConstraintType = 37
  _Parent = -> Constraints
FEATURE [App::FeaturePython] ElementLink157  label="_Element133"  # link proxy (typed FeaturePython)
  LinkTransform = true
  LinkedObject = -> _Element133
  _Parent = -> Constraint079
FEATURE [Part::FeaturePython] _Element133  # link proxy (typed FeaturePython)
  Detach = false
  LinkTransform = true
  LinkedObject = -> Link023 [Pocket003.Face7]
  _Parent = -> Elements
FEATURE [App::FeaturePython] ElementLink158  label="_Element134"  # link proxy (typed FeaturePython)
  LinkTransform = true
  LinkedObject = -> _Element134
  _Parent = -> Constraint079
FEATURE [Part::FeaturePython] _Element134  # link proxy (typed FeaturePython)
  Detach = false
  LinkTransform = true
  LinkedObject = -> Link024 [Pocket.Face9]
  _Parent = -> Elements
FEATURE [App::FeaturePython] Constraint080  label="PlaneAlignment079"  # WARN: FeaturePython — macro-defined, semantics opaque (R4)
  Angle = 0
  AnglePitch = 0
  AngleRoll = 0
  Cascade = false
  Disabled = false
  Group = -> [ElementLink159,ElementLink160]
  LockAngle = false
  _ConstraintType = 37
  _Parent = -> Constraints
FEATURE [App::FeaturePython] ElementLink159  label="_Element135"  # link proxy (typed FeaturePython)
  LinkTransform = true
  LinkedObject = -> _Element135
  _Parent = -> Constraint080
FEATURE [Part::FeaturePython] _Element135  # link proxy (typed FeaturePython)
  Detach = false
  LinkTransform = true
  LinkedObject = -> Link025 [Face10]
  _Parent = -> Elements
FEATURE [App::FeaturePython] ElementLink160  label="_Element136"  # link proxy (typed FeaturePython)
  LinkTransform = true
  LinkedObject = -> _Element136
  _Parent = -> Constraint080
FEATURE [Part::FeaturePython] _Element136  # link proxy (typed FeaturePython)
  Detach = false
  LinkTransform = true
  LinkedObject = -> Link024 [Pocket.Face2]
  _Parent = -> Elements

RESOLVED EXTERNAL PARTS (link-assembly join: the EXTERNAL_REF files above that resolve inside this repo's crawl, each included once):
---- part parts/BaseMagnetoPot.FCStd = doc fcstd_0771cd1a7cab ----
FCSTD DOCUMENT  (FreeCAD 0.21R33668 +26 (Git))
Label: BaseMagnetoPot
License: All rights reserved
LicenseURL: http://en.wikipedia.org/wiki/All_rights_reserved
objects: Sketcher::SketchObject×10, PartDesign::Pocket×5, PartDesign::Pad×4, PartDesign::SubShapeBinder×2, PartDesign::Body×2
note: 32 computed .brp shape members not serialized (recipe doc carries the construction recipe); baked Part::Feature solids carry a one-line shape summary decoded from their .brp
EXTERNAL_REF file=MG/Datasheet.FCStd obj=Spreadsheet
EXTERNAL_REF file=MG/mgn9c_13.FCStd obj=Body
EXTERNAL_REF file=MagnetoPot/MagnetoPot.FCStd obj=Body
EXTERNAL_REF file=MG/mgn9c_13.FCStd obj=Sketch

FEATURE [PartDesign::SubShapeBinder] Binder  label="Rail"
  BindCopyOnChange = 0
  BindMode = 0
  ClaimChildren = false
  Context = -> Body [Binder.]
  Fuse = false
  MakeFace = true
  OffsetFill = false
  OffsetIntersection = false
  OffsetJoinType = 0
  OffsetOpenResult = false
  PartialLoad = false
  Relative = true
  Support = -> [<external MG/mgn9c_13.FCStd>#Body]
  _Version = 2
FEATURE [Sketcher::SketchObject] Sketch
  ExternalGeometry = -> [Binder]
  FullyConstrained = true
  MapMode = 5
  Support = -> [XY_Plane]
  expr: .Constraints.EndStopToActiveDistance = (<<Datasheet>>#<<mgn9c>>.Dim_L - <<Datasheet>>#<<mgn9c>>.Dim_L1) / 2
  expr: .Constraints.PartWidth = 20.3
  expr: .Constraints.TravelDistance = 200 mm + <<Datasheet>>#<<mgn9c>>.Dim_L - 2 mm
  expr: Constraints[25] = <<Datasheet>>#<<mgn9c>>.Dim_L
  sketch-geometry (23):
    g0: Circle CenterX=7.5 CenterY=4.5 CenterZ=0 NormalX=0 NormalY=0 NormalZ=1 AngleXU=0 Radius=1.75
    g1: LineSegment StartX=0 StartY=0 StartZ=0 EndX=14.05 EndY=0 EndZ=0
    g2: LineSegment StartX=14.05 StartY=0 StartZ=0 EndX=14.05 EndY=9 EndZ=0
    g3: LineSegment StartX=14.05 StartY=9 StartZ=0 EndX=0 EndY=9 EndZ=0
    g4: LineSegment StartX=0 StartY=9 StartZ=0 EndX=0 EndY=0 EndZ=0
    g5: GeomPoint X=127.5 Y=9 Z=0
    g6: GeomPoint X=240.95 Y=9 Z=0
    g7: GeomPoint X=7.5 Y=6.25 Z=0
    g8: LineSegment StartX=14.05 StartY=9 StartZ=0 EndX=19.05 EndY=9 EndZ=0
    g9: LineSegment StartX=19.05 StartY=0 StartZ=0 EndX=14.05 EndY=9 EndZ=0
    g10: GeomPoint X=219.05 Y=0 Z=0
    g11: GeomPoint X=212.05 Y=9 Z=0
    g12: GeomPoint X=119.05 Y=0 Z=0
    g13: GeomPoint X=11.12 Y=0 Z=0
    g14: GeomPoint X=226.98 Y=0 Z=0
    g15: LineSegment StartX=19.05 StartY=0 StartZ=0 EndX=19.05 EndY=-20.3 EndZ=0
    g16: LineSegment StartX=11.12 StartY=-20.3 StartZ=0 EndX=19.05 EndY=-20.3 EndZ=0
    g17: LineSegment StartX=11.12 StartY=0 StartZ=0 EndX=11.12 EndY=-20.3 EndZ=0
    g18: GeomPoint X=0 Y=0 Z=0
    g19: GeomPoint X=11.12 Y=0 Z=0
    g20: GeomPoint X=0 Y=0 Z=0
    g21: GeomPoint X=11.12 Y=0 Z=0
    g22: LineSegment StartX=0 StartY=0 StartZ=0 EndX=11.12 EndY=0 EndZ=0
  constraints (49):
    c: Coincident(g0,g-5)
    c: Coincident(g1,g2)
    c: Coincident(g2,g3)
    c: Coincident(g3,g4)
    c: Coincident(g4,g1)
    c: Horizontal(g1)
    c: Horizontal(g3)
    c: Vertical(g2)
    c: Vertical(g4)
    c: Coincident(g1,g-4)
    c: PointOnObject(g2,g-3)
    c: Symmetric(g3,g-3,g5)
    c: Symmetric(g2,g6,g5)
    c: DistanceX(g2,g6) = 226.9  'TravelDistance'
    c: PointOnObject(g7,g0)
    c: PointOnObject(g7,g-5)
    c: Vertical(g7,g0)
    c: Coincident(g8,g3)
    c: PointOnObject(g8,g-3)
    c: DistanceX(g8,g8) = 5  'EndStopToActiveDistance'
    c: PointOnObject(g9,g-4)
    c: Coincident(g9,g3)
    c: PointOnObject(g10,g-4)
    c: DistanceX(g9,g10) = 200  'MagnetoPotActiveLength'
    c: PointOnObject(g11,g-3)
    c: DistanceX(g11,g6) = 28.9
    c: Symmetric(g10,g9,g12)
    c: Symmetric(g14,g13,g12)
    c: DistanceX(g13,g14) = 215.86  'MagnetoPotPartLength'
    c: Vertical(g9,g8)
    c: Coincident(g15,g9)
    c: Vertical(g15)
    c: Coincident(g16,g15)
    c: Horizontal(g16)
    c: Coincident(g17,g16)
    c: Coincident(g18,g4)
    c: Coincident(g19,g17)
    c: Vertical(g17)
    c: DistanceY(g17,g17) = 20.3  'PartWidth'
    c: Coincident(g20,g4)
    c: Coincident(g21,g17)
    c: Coincident(g22,g4)
    c: Coincident(g22,g17)
    c: PointOnObject(g17,g1)
    c: Coincident(g17,g13)
    c: DistanceX(g14,g-4) = 28.02  'Base_End'
    c: DistanceX(g3,g3) = 14.05  'EndStopDistance'
    c: DistanceX(g4,g17) = 11.12  'Rail_To_Part'
    c: DistanceX(g16,g15) = 7.93  'PartStartToActiveStart'
FEATURE [PartDesign::Pad] Pad
  Direction = (0,0,1)
  Length = 6
  Length2 = 10
  Profile = -> Sketch
  ReferenceAxis = -> Sketch [N_Axis]
  Reversed = true
  Type = 0
FEATURE [PartDesign::SubShapeBinder] Binder001  label="MagnetoPot_Binder"
  BindCopyOnChange = 0
  BindMode = 0
  ClaimChildren = false
  Context = -> Body [Binder001.]
  Fuse = false
  MakeFace = true
  OffsetFill = false
  OffsetIntersection = false
  OffsetJoinType = 0
  OffsetOpenResult = false
  PartialLoad = false
  Placement = pos=(5,-20.5,0) rot=(0,0,1;0rad)
  Relative = true
  Support = -> [<external MagnetoPot/MagnetoPot.FCStd>#Body]
  _Version = 2
FEATURE [Sketcher::SketchObject] Sketch001
  ExternalGeometry = -> [Pad]
  FullyConstrained = true
  MapMode = 5
  Placement = pos=(0,0,-6) rot=(1,0,0;3.14159rad)
  Support = -> [Pad]
  expr: .Constraints.MagnetoPotTailWidth = 10.16
  expr: Constraints[22] = .Constraints.Strength
  expr: Constraints[23] = .Constraints.Strength
  expr: Constraints[25] = .Constraints.Strength
  expr: Constraints[28] = .Constraints.Strength
  sketch-geometry (21):
    g0: LineSegment StartX=19.05 StartY=20.3 StartZ=0 EndX=19.05 EndY=22.3 EndZ=0
    g1: LineSegment StartX=19.05 StartY=22.3 StartZ=0 EndX=9.12 EndY=22.3 EndZ=0
    g2: LineSegment StartX=9.12 StartY=22.3 StartZ=0 EndX=9.12 EndY=2 EndZ=0
    g3: LineSegment StartX=9.12 StartY=2 StartZ=0 EndX=-2 EndY=2 EndZ=0
    g4: LineSegment StartX=-2 StartY=2 StartZ=0 EndX=-2 EndY=-11 EndZ=0
    g5: LineSegment StartX=-2 StartY=-11 StartZ=0 EndX=14.05 EndY=-11 EndZ=0
    g6: LineSegment StartX=14.05 StartY=-11 StartZ=0 EndX=14.05 EndY=-9 EndZ=0
    g7: LineSegment StartX=14.05 StartY=-9 StartZ=0 EndX=0 EndY=-9 EndZ=0
    g8: LineSegment StartX=0 StartY=0 StartZ=0 EndX=0 EndY=-9 EndZ=0
    g9: LineSegment StartX=0 StartY=0 StartZ=0 EndX=11.12 EndY=0 EndZ=0
    g10: LineSegment StartX=11.12 StartY=0 StartZ=0 EndX=11.12 EndY=20.3 EndZ=0
    g11: LineSegment StartX=11.12 StartY=20.3 StartZ=0 EndX=19.05 EndY=20.3 EndZ=0
    g12: GeomPoint X=11.12 Y=15.23 Z=0
    g13: GeomPoint X=11.12 Y=10.15 Z=0
    g14: GeomPoint X=11.12 Y=5.07 Z=0
    g15: LineSegment StartX=11.12 StartY=20.3 StartZ=0 EndX=11.12 EndY=15.23 EndZ=0
    g16: LineSegment StartX=11.12 StartY=15.23 StartZ=0 EndX=9.12 EndY=15.23 EndZ=0
    g17: LineSegment StartX=9.12 StartY=15.23 StartZ=0 EndX=9.12 EndY=22.3 EndZ=0
    g18: LineSegment StartX=11.12 StartY=5.07 StartZ=0 EndX=9.12 EndY=5.07 EndZ=0
    g19: LineSegment StartX=9.12 StartY=5.07 StartZ=0 EndX=9.12 EndY=2 EndZ=0
    g20: LineSegment StartX=11.12 StartY=0 StartZ=0 EndX=11.12 EndY=5.07 EndZ=0
  constraints (48):
    c: Coincident(g0,g-7)
    c: Vertical(g0)
    c: Horizontal(g1)
    c: Coincident(g2,g1)
    c: Coincident(g3,g2)
    c: Horizontal(g3)
    c: Coincident(g4,g3)
    c: Coincident(g5,g4)
    c: Coincident(g6,g5)
    c: Coincident(g6,g-5)
    c: Coincident(g7,g6)
    c: Coincident(g7,g-5)
    c: Coincident(g8,g-4)
    c: Coincident(g8,g7)
    c: Coincident(g9,g8)
    c: Coincident(g9,g-6)
    c: Coincident(g10,g9)
    c: Coincident(g10,g-7)
    c: Coincident(g11,g10)
    c: Coincident(g11,g0)
    c: Coincident(g0,g1)
    c: DistanceY(g0,g0) = 2  'Strength'
    c: DistanceX(g1,g10) = 2
    c: DistanceY(g9,g2) = 2
    c: Vertical(g2)
    c: DistanceX(g3,g8) = 2
    c: Vertical(g4)
    c: Horizontal(g5)
    c: DistanceY(g4,g7) = 2
    c: Vertical(g6)
    c: PointOnObject(g12,g10)
    c: Symmetric(g9,g11,g13)
    c: Symmetric(g12,g14,g13)
    c: DistanceY(g14,g12) = 10.16  'MagnetoPotTailWidth'
    c: Coincident(g15,g11)
    c: Coincident(g15,g12)
    c: Coincident(g16,g12)
    c: PointOnObject(g16,g2)
    c: Horizontal(g16)
    c: Coincident(g17,g16)
    c: Coincident(g17,g1)
    c: Coincident(g18,g14)
    c: PointOnObject(g18,g2)
    c: Coincident(g19,g18)
    c: Coincident(g19,g3)
    c: Coincident(g20,g9)
    c: Coincident(g20,g18)
    c: Horizontal(g18)
FEATURE [PartDesign::Pad] Pad001
  BaseFeature = -> Pad
  Direction = (0,0,-1)
  Length = 11.5
  Length2 = 10
  Profile = -> Sketch001
  ReferenceAxis = -> Sketch001 [N_Axis]
  Reversed = true
  Type = 0
FEATURE [Sketcher::SketchObject] Sketch002
  ExternalGeometry = -> [Pad001]
  FullyConstrained = true
  MapMode = 5
  Support = -> [Pad001]
  sketch-geometry (4):
    g0: LineSegment StartX=19.05 StartY=0 StartZ=0 EndX=11.12 EndY=0 EndZ=0
    g1: LineSegment StartX=11.12 StartY=0 StartZ=0 EndX=11.12 EndY=-20.3 EndZ=0
    g2: LineSegment StartX=11.12 StartY=-20.3 StartZ=0 EndX=19.05 EndY=-20.3 EndZ=0
    g3: LineSegment StartX=19.05 StartY=-20.3 StartZ=0 EndX=19.05 EndY=0 EndZ=0
  constraints (10):
    c: Coincident(g0,g1)
    c: Coincident(g1,g2)
    c: Coincident(g2,g3)
    c: Coincident(g3,g0)
    c: Horizontal(g0)
    c: Horizontal(g2)
    c: Vertical(g1)
    c: Coincident(g0,g-4)
    c: PointOnObject(g-3,g1)
    c: Coincident(g2,g-4)
FEATURE [PartDesign::Pocket] Pocket
  BaseFeature = -> Pad001
  Direction = (0,0,-1)
  Length = 2
  Length2 = 5
  Profile = -> Sketch002
  ReferenceAxis = -> Sketch002 [N_Axis]
  Type = 0
  expr: Length = 3.5 mm - <<Datasheet>>#<<mgn9c>>.Dim_H1 + 0.5 mm
FEATURE [Sketcher::SketchObject] Sketch003
  ExternalGeometry = -> [Pocket]
  FullyConstrained = true
  MapMode = 5
  Placement = pos=(0,0,-6) rot=(1,0,0;3.14159rad)
  Support = -> [Pocket]
  expr: Constraints[1] = <<Datasheet>>#<<mgn9c>>.Dim_D
  sketch-geometry (1):
    g0: Circle CenterX=7.5 CenterY=-4.5 CenterZ=0 NormalX=0 NormalY=0 NormalZ=1 AngleXU=0 Radius=3
  constraints (2):
    c: Coincident(g0,g-3)
    c: Diameter(g0) = 6
FEATURE [PartDesign::Pocket] Pocket001
  BaseFeature = -> Pocket
  Direction = (0,0,1)
  Length = 4
  Length2 = 5
  Profile = -> Sketch003
  ReferenceAxis = -> Sketch003 [N_Axis]
  Type = 0
  expr: Length = <<Pad>>.Length - (<<Datasheet>>#<<mgn9c>>.Dim_Hr - <<Datasheet>>#<<mgn9c>>.Dim_h - 1 mm)
FEATURE [Sketcher::SketchObject] Sketch004
  FullyConstrained = true
  MapMode = 5
  Support = -> [XY_Plane001]
  expr: Constraints[10] = <<mgn9c_13>>#<<Sketch>>.Constraints.Rail_Length
  expr: Constraints[28] = <<Sketch>>.Constraints.MagnetoPotActiveLength
  expr: Constraints[29] = <<Sketch>>.Constraints.MagnetoPotPartLength
  expr: Constraints[34] = <<Sketch>>.Constraints.TravelDistance
  expr: Constraints[35] = <<Sketch>>.Constraints.EndStopDistance
  expr: Constraints[37] = <<Sketch>>.Constraints.EndStopToActiveDistance
  expr: Constraints[38] = <<Sketch>>.Constraints.PartWidth
  expr: Constraints[44] = <<Datasheet>>#<<mgn9c>>.Dim_d
  expr: Constraints[45] = <<Datasheet>>#<<mgn9c>>.Dim_E
  expr: Constraints[9] = <<Datasheet>>#<<mgn9c>>.Dim_Wr
  sketch-geometry (21):
    g0: LineSegment StartX=-255 StartY=9 StartZ=0 EndX=0 EndY=9 EndZ=0
    g1: LineSegment StartX=0 StartY=9 StartZ=0 EndX=0 EndY=0 EndZ=0
    g2: LineSegment StartX=0 StartY=0 StartZ=0 EndX=-255 EndY=0 EndZ=0
    g3: LineSegment StartX=-255 StartY=0 StartZ=0 EndX=-255 EndY=9 EndZ=0
    g4: LineSegment StartX=-35.95 StartY=-20.3 StartZ=0 EndX=-35.95 EndY=9 EndZ=0
    g5: LineSegment StartX=-35.95 StartY=9 StartZ=0 EndX=0 EndY=9 EndZ=0
    g6: LineSegment StartX=0 StartY=9 StartZ=0 EndX=0 EndY=0 EndZ=0
    g7: LineSegment StartX=0 StartY=0 StartZ=0 EndX=-28.02 EndY=0 EndZ=0
    g8: LineSegment StartX=-28.02 StartY=0 StartZ=0 EndX=-28.02 EndY=-20.3 EndZ=0
    g9: LineSegment StartX=-35.95 StartY=-20.3 StartZ=0 EndX=-28.02 EndY=-20.3 EndZ=0
    g10: GeomPoint X=-135.95 Y=0 Z=0
    g11: GeomPoint X=-235.95 Y=0 Z=0
    g12: GeomPoint X=-35.95 Y=0 Z=0
    g13: GeomPoint X=-243.88 Y=0 Z=0
    g14: GeomPoint X=-28.02 Y=0 Z=0
    g15: GeomPoint X=-240.95 Y=9 Z=0
    g16: GeomPoint X=-14.05 Y=9 Z=0
    g17: GeomPoint X=-127.5 Y=9 Z=0
    g18: Circle CenterX=-7.5 CenterY=4.5 CenterZ=0 NormalX=0 NormalY=0 NormalZ=1 AngleXU=0 Radius=1.75
    g19: GeomPoint X=-7.5 Y=4.5 Z=0
    g20: LineSegment StartX=-7.5 StartY=4.5 StartZ=0 EndX=0 EndY=4.5 EndZ=0
  constraints (46):
    c: Coincident(g0,g1)
    c: Coincident(g1,g2)
    c: Coincident(g2,g3)
    c: Coincident(g3,g0)
    c: Horizontal(g0)
    c: Horizontal(g2)
    c: Vertical(g1)
    c: Vertical(g3)
    c: Coincident(g1,g-1)
    c: DistanceY(g1,g1) = 9
    c: DistanceX(g0,g0) = 255
    c: Coincident(g4,g5)
    c: Coincident(g5,g6)
    c: Horizontal(g5)
    c: Vertical(g4)
    c: Vertical(g6)
    c: PointOnObject(g4,g0)
    c: Coincident(g7,g6)
    c: PointOnObject(g7,g2)
    c: Coincident(g8,g7)
    c: Vertical(g8)
    c: Coincident(g9,g4)
    c: Coincident(g9,g8)
    c: Horizontal(g9)
    c: PointOnObject(g10,g2)
    c: PointOnObject(g11,g2)
    c: Symmetric(g14,g13,g10)
    c: Symmetric(g11,g12,g10)
    c: DistanceX(g11,g12) = 200
    c: DistanceX(g13,g14) = 215.86
    c: Coincident(g14,g7)
    c: PointOnObject(g15,g0)
    c: PointOnObject(g16,g0)
    c: Symmetric(g15,g16,g17)
    c: DistanceX(g15,g16) = 226.9
    c: DistanceX(g0,g15) = 14.05
    c: PointOnObject(g12,g4)
    c: DistanceX(g15,g11) = 5
    c: DistanceY(g8,g8) = 20.3
    c: Coincident(g6,g1)
    c: Coincident(g19,g18)
    c: Horizontal(g20)
    c: Coincident(g18,g20)
    c: Symmetric(g5,g6,g20)
    c: Diameter(g18) = 3.5
    c: DistanceX(g18,g20) = 7.5
FEATURE [PartDesign::Pad] Pad002
  Direction = (0,0,1)
  Length = 6
  Length2 = 10
  Profile = -> Sketch004
  ReferenceAxis = -> Sketch004 [N_Axis]
  Reversed = true
  Type = 0
  expr: Length = <<Pad>>.Length
FEATURE [Sketcher::SketchObject] Sketch006
  ExternalGeometry = -> [Pad002]
  FullyConstrained = true
  MapMode = 5
  Placement = pos=(0,0,-6) rot=(1,0,0;3.14159rad)
  Support = -> [Pad002]
  expr: Constraints[18] = <<Sketch001>>.Constraints.Strength
  expr: Constraints[19] = <<Sketch001>>.Constraints.Strength
  expr: Constraints[20] = <<Sketch001>>.Constraints.Strength
  expr: Constraints[21] = <<Sketch001>>.Constraints.Strength
  expr: Constraints[23] = <<Sketch001>>.Constraints.Strength
  expr: Constraints[27] = <<Sketch001>>.Constraints.MagnetoPotTailWidth
  sketch-geometry (17):
    g0: LineSegment StartX=2 StartY=2 StartZ=0 EndX=2 EndY=-11 EndZ=0
    g1: LineSegment StartX=2 StartY=-11 StartZ=0 EndX=-35.95 EndY=-11 EndZ=0
    g2: LineSegment StartX=-35.95 StartY=-11 StartZ=0 EndX=-35.95 EndY=-9 EndZ=0
    g3: LineSegment StartX=-35.95 StartY=22.3 StartZ=0 EndX=-26.02 EndY=22.3 EndZ=0
    g4: LineSegment StartX=-26.02 StartY=22.3 StartZ=0 EndX=-26.02 EndY=15.23 EndZ=0
    g5: LineSegment StartX=-26.02 StartY=15.23 StartZ=0 EndX=-28.02 EndY=15.23 EndZ=0
    g6: LineSegment StartX=-28.02 StartY=5.07 StartZ=0 EndX=-26.02 EndY=5.07 EndZ=0
    g7: LineSegment StartX=-26.02 StartY=5.07 StartZ=0 EndX=-26.02 EndY=2 EndZ=0
    g8: LineSegment StartX=-26.02 StartY=2 StartZ=0 EndX=2 EndY=2 EndZ=0
    g9: LineSegment StartX=-35.95 StartY=22.3 StartZ=0 EndX=-35.95 EndY=20.3 EndZ=0
    g10: GeomPoint X=-28.02 Y=10.15 Z=0
    g11: LineSegment StartX=-35.95 StartY=20.3 StartZ=0 EndX=-28.02 EndY=20.3 EndZ=0
    g12: LineSegment StartX=-28.02 StartY=20.3 StartZ=0 EndX=-28.02 EndY=15.23 EndZ=0
    g13: LineSegment StartX=-28.02 StartY=5.07 StartZ=0 EndX=-28.02 EndY=0 EndZ=0
    g14: LineSegment StartX=-28.02 StartY=0 StartZ=0 EndX=0 EndY=0 EndZ=0
    g15: LineSegment StartX=0 StartY=0 StartZ=0 EndX=0 EndY=-9 EndZ=0
    g16: LineSegment StartX=0 StartY=-9 StartZ=0 EndX=-35.95 EndY=-9 EndZ=0
  constraints (42):
    c: Vertical(g0)
    c: Coincident(g1,g0)
    c: Horizontal(g1)
    c: Coincident(g2,g1)
    c: Coincident(g2,g-6)
    c: Vertical(g2)
    c: Horizontal(g3)
    c: Coincident(g4,g3)
    c: Vertical(g4)
    c: PointOnObject(g5,g-3)
    c: Horizontal(g5)
    c: Coincident(g8,g7)
    c: Coincident(g8,g0)
    c: Horizontal(g8)
    c: Coincident(g4,g5)
    c: Coincident(g6,g7)
    c: Horizontal(g6)
    c: Vertical(g7)
    c: DistanceY(g2,g2) = 2
    c: DistanceX(g-6,g0) = 2
    c: DistanceY(g-1,g0) = 2
    c: DistanceX(g-3,g7) = 2
    c: Vertical(g4,g6)
    c: DistanceY(g-5,g3) = 2
    c: Coincident(g9,g3)
    c: Vertical(g9)
    c: Coincident(g9,g-5)
    c: DistanceY(g6,g4) = 10.16
    c: Symmetric(g-5,g-3,g10)
    c: Symmetric(g5,g6,g10)
    c: Coincident(g11,g9)
    c: Coincident(g11,g-5)
    c: Coincident(g12,g11)
    c: Coincident(g12,g5)
    c: Coincident(g6,g13)
    c: Coincident(g13,g-3)
    c: Coincident(g13,g14)
    c: Coincident(g14,g-1)
    c: Coincident(g14,g15)
    c: Coincident(g15,g-6)
    c: Coincident(g15,g16)
    c: Coincident(g16,g2)
FEATURE [Sketcher::SketchObject] Sketch007  label="Measurements"
  ExternalGeometry = -> [Pocket001]
  FullyConstrained = true
  MapMode = 5
  Placement = pos=(0,0,0) rot=(1,0,0;1.5708rad)
  Support = -> [XZ_Plane]
  constraints (3):
    c: DistanceY(g-4,g-5) = 6  'BaseHeight'
    c: DistanceY(g-4,g-6) = 4  'MagnetoPotHeight'
    c: DistanceY(g-4,g-3) = 11.5  'TotalHeight'
FEATURE [PartDesign::Body] Body  label="BaseMagentoPot"
  Group = -> [Sketch,Binder,Pad,Binder001,Sketch001,Pad001,Sketch002,Pocket,Sketch003,Pocket001,Sketch007]
  Origin = -> Origin
  Tip = -> Pocket001
FEATURE [PartDesign::Pad] Pad003
  BaseFeature = -> Pad002
  Direction = (0,0,-1)
  Length = 11.5
  Length2 = 10
  Profile = -> Sketch006
  ReferenceAxis = -> Sketch006 [N_Axis]
  Reversed = true
  Type = 0
  expr: Length = Sketch007.Constraints.TotalHeight
FEATURE [Sketcher::SketchObject] Sketch008
  ExternalGeometry = -> [Pad003]
  FullyConstrained = true
  MapMode = 5
  Support = -> [Pad003]
  sketch-geometry (4):
    g0: LineSegment StartX=-35.95 StartY=-20.3 StartZ=0 EndX=-28.02 EndY=-20.3 EndZ=0
    g1: LineSegment StartX=-28.02 StartY=-20.3 StartZ=0 EndX=-28.02 EndY=0 EndZ=0
    g2: LineSegment StartX=-28.02 StartY=0 StartZ=0 EndX=-35.95 EndY=0 EndZ=0
    g3: LineSegment StartX=-35.95 StartY=0 StartZ=0 EndX=-35.95 EndY=-20.3 EndZ=0
  constraints (10):
    c: Coincident(g0,g1)
    c: Coincident(g1,g2)
    c: Coincident(g2,g3)
    c: Coincident(g3,g0)
    c: Horizontal(g0)
    c: Horizontal(g2)
    c: Vertical(g1)
    c: Vertical(g3)
    c: Coincident(g0,g-4)
    c: Coincident(g1,g-3)
FEATURE [PartDesign::Pocket] Pocket002
  BaseFeature = -> Pad003
  Direction = (0,0,-1)
  Length = 2
  Length2 = 5
  Profile = -> Sketch008
  ReferenceAxis = -> Sketch008 [N_Axis]
  Type = 0
  expr: Length = <<Measurements>>.Constraints.BaseHeight - <<Measurements>>.Constraints.MagnetoPotHeight
FEATURE [Sketcher::SketchObject] Sketch009
  ExternalGeometry = -> [Pocket002]
  FullyConstrained = true
  MapMode = 5
  Placement = pos=(0,0,5.5) rot=(0,0,1;0rad)
  Support = -> [Pocket002]
  expr: Constraints[10] = <<Sketch>>.Constraints.EndStopDistance
  expr: Constraints[11] = <<Datasheet>>#<<mgn9c>>.Dim_W
  sketch-geometry (5):
    g0: LineSegment StartX=-35.95 StartY=14.5 StartZ=0 EndX=-14.05 EndY=14.5 EndZ=0
    g1: LineSegment StartX=-14.05 StartY=14.5 StartZ=0 EndX=-14.05 EndY=-5.5 EndZ=0
    g2: LineSegment StartX=-14.05 StartY=-5.5 StartZ=0 EndX=-35.95 EndY=-5.5 EndZ=0
    g3: LineSegment StartX=-35.95 StartY=-5.5 StartZ=0 EndX=-35.95 EndY=14.5 EndZ=0
    g4: LineSegment StartX=-7.5 StartY=4.5 StartZ=0 EndX=-35.95 EndY=4.5 EndZ=0
  constraints (14):
    c: Coincident(g0,g1)
    c: Coincident(g1,g2)
    c: Coincident(g2,g3)
    c: Coincident(g3,g0)
    c: Horizontal(g0)
    c: Horizontal(g2)
    c: Vertical(g1)
    c: Vertical(g3)
    c: Coincident(g4,g-5)
    c: PointOnObject(g4,g3)
    c: DistanceX(g0,g-6) = 14.05
    c: DistanceY(g3,g3) = 20
    c: Symmetric(g0,g2,g4)
    c: PointOnObject(g-6,g3)
FEATURE [PartDesign::Pocket] Pocket003
  BaseFeature = -> Pocket002
  Direction = (0,0,-1)
  Length = 5
  Length2 = 5
  Profile = -> Sketch009
  ReferenceAxis = -> Sketch009 [N_Axis]
  Type = 2
FEATURE [Sketcher::SketchObject] Sketch010
  ExternalGeometry = -> [Pocket003]
  FullyConstrained = true
  MapMode = 5
  Placement = pos=(0,0,-6) rot=(1,0,0;3.14159rad)
  Support = -> [Pocket003]
  expr: Constraints[1] = <<Datasheet>>#<<mgn9c>>.Dim_D
  sketch-geometry (1):
    g0: Circle CenterX=-7.5 CenterY=-4.5 CenterZ=0 NormalX=0 NormalY=0 NormalZ=1 AngleXU=0 Radius=3
  constraints (2):
    c: Coincident(g0,g-3)
    c: Diameter(g0) = 6
FEATURE [PartDesign::Pocket] Pocket004
  BaseFeature = -> Pocket003
  Direction = (0,0,1)
  Length = 4
  Length2 = 5
  Profile = -> Sketch010
  ReferenceAxis = -> Sketch010 [N_Axis]
  Type = 0
  expr: Length = <<Pad002>>.Length - (<<Datasheet>>#<<mgn9c>>.Dim_Hr - <<Datasheet>>#<<mgn9c>>.Dim_h - 1 mm)
FEATURE [PartDesign::Body] Body001  label="BaseMagnetoPot_Opposite"
  Group = -> [Sketch004,Pad002,Sketch006,Pad003,Sketch008,Pocket002,Sketch009,Pocket003,Sketch010,Pocket004]
  Origin = -> Origin001
  Placement = pos=(-11,0,0) rot=(0,0,1;0rad)
  Tip = -> Pocket004
---- part parts/Joystick_Holder.FCStd = doc fcstd_c2c9535a4b80 ----
FCSTD DOCUMENT  (FreeCAD 0.21R33668 +26 (Git))
Label: Joystick_Holder
License: All rights reserved
LicenseURL: http://en.wikipedia.org/wiki/All_rights_reserved
objects: Sketcher::SketchObject×6, PartDesign::Pad×4, PartDesign::SubShapeBinder×2, PartDesign::Pocket×2, PartDesign::Body×1
note: 21 computed .brp shape members not serialized (recipe doc carries the construction recipe); baked Part::Feature solids carry a one-line shape summary decoded from their .brp
EXTERNAL_REF file=MG/mgn9c_slide.FCStd obj=Body001
EXTERNAL_REF file=R202.FCStd obj=Revolution
EXTERNAL_REF file=MG/Datasheet.FCStd obj=Spreadsheet
EXTERNAL_REF file=NormalConnectorMagnet.FCStd obj=Sketch002
EXTERNAL_REF file=NormalConnectorMagnet.FCStd obj=Pad002
EXTERNAL_REF file=NormalConnectorMagnet.FCStd obj=Sketch003

FEATURE [PartDesign::SubShapeBinder] Binder  label="Slide"
  BindCopyOnChange = 0
  BindMode = 0
  ClaimChildren = false
  Context = -> Body [Binder.]
  Fuse = false
  MakeFace = true
  OffsetFill = false
  OffsetIntersection = false
  OffsetJoinType = 0
  OffsetOpenResult = false
  PartialLoad = false
  Placement = pos=(0,0,0) rot=(0,0,1;1.5708rad)
  Relative = true
  Support = -> [<external MG/mgn9c_slide.FCStd>#Body001]
  _Version = 2
FEATURE [PartDesign::SubShapeBinder] Binder001  label="Joystick"
  BindCopyOnChange = 0
  BindMode = 0
  ClaimChildren = false
  Context = -> Body [Binder001.]
  Fuse = false
  MakeFace = true
  OffsetFill = false
  OffsetIntersection = false
  OffsetJoinType = 0
  OffsetOpenResult = false
  PartialLoad = false
  Placement = pos=(-16.5,16.5,-29.5) rot=(0,0,-1;1.5708rad)
  Relative = true
  Support = -> [<external R202.FCStd>#Revolution]
  _Version = 2
FEATURE [Sketcher::SketchObject] Sketch
  ExternalGeometry = -> [Binder001]
  FullyConstrained = true
  MapMode = 5
  Placement = pos=(-16.5,16.5,0) rot=(0,0,-1;1.5708rad)
  Support = -> [Binder001]
  sketch-geometry (17):
    g0: LineSegment StartX=-20.2 StartY=25.2 StartZ=0 EndX=20.2 EndY=25.2 EndZ=0
    g1: LineSegment StartX=20.2 StartY=25.2 StartZ=0 EndX=20.2 EndY=20.2 EndZ=0
    g2: LineSegment StartX=20.2 StartY=20.2 StartZ=0 EndX=-20.2 EndY=20.2 EndZ=0
    g3: LineSegment StartX=-20.2 StartY=20.2 StartZ=0 EndX=-20.2 EndY=25.2 EndZ=0
    g4: LineSegment StartX=-20.2 StartY=20.2 StartZ=0 EndX=-20.2 EndY=-16.25 EndZ=0
    g5: LineSegment StartX=-12.3 StartY=-16.25 StartZ=0 EndX=-12.3 EndY=-12.4483 EndZ=0
    g6: ArcOfCircle CenterX=-16.25 CenterY=-16.25 CenterZ=0 NormalX=0 NormalY=0 NormalZ=1 AngleXU=0 Radius=3.95 StartAngle=3.14159 EndAngle=6.28319
    g7: ArcOfCircle CenterX=0 CenterY=-1.78e-14 CenterZ=0 NormalX=0 NormalY=0 NormalZ=1 AngleXU=0 Radius=17.5 StartAngle=5.4918 EndAngle=10.2162
    g8: LineSegment StartX=12.3 StartY=-12.4483 StartZ=0 EndX=12.3 EndY=-16.25 EndZ=0
    g9: ArcOfCircle CenterX=16.25 CenterY=-16.25 CenterZ=0 NormalX=0 NormalY=0 NormalZ=1 AngleXU=0 Radius=3.95 StartAngle=3.14159 EndAngle=6.28319
    g10: LineSegment StartX=20.2 StartY=20.2 StartZ=0 EndX=20.2 EndY=-16.25 EndZ=0
    g11: Circle CenterX=-16.25 CenterY=16.25 CenterZ=0 NormalX=0 NormalY=0 NormalZ=1 AngleXU=0 Radius=1
    g12: Circle CenterX=16.25 CenterY=16.25 CenterZ=0 NormalX=0 NormalY=0 NormalZ=1 AngleXU=0 Radius=1
    g13: Circle CenterX=16.25 CenterY=-16.25 CenterZ=0 NormalX=0 NormalY=0 NormalZ=1 AngleXU=0 Radius=1
    g14: Circle CenterX=-16.25 CenterY=-16.25 CenterZ=0 NormalX=0 NormalY=0 NormalZ=1 AngleXU=0 Radius=1
    g15: GeomPoint X=-16.25 Y=-17.25 Z=0
    g16: GeomPoint X=16.25 Y=-15.25 Z=0
  constraints (39):
    c: Coincident(g0,g1)
    c: Coincident(g1,g2)
    c: Coincident(g2,g3)
    c: Coincident(g3,g0)
    c: Horizontal(g0)
    c: Vertical(g1)
    c: Vertical(g3)
    c: Coincident(g1,g-8)
    c: Coincident(g2,g-8)
    c: DistanceY(g3,g3) = 5  'Strength'
    c: Coincident(g4,g3)
    c: Vertical(g4)
    c: PointOnObject(g5,g-9)
    c: Vertical(g5)
    c: Coincident(g6,g-5)
    c: Coincident(g6,g4)
    c: Horizontal(g4,g6)
    c: Tangent(g6,g5) = -1.5708
    c: Coincident(g7,g-9)
    c: Coincident(g7,g5)
    c: Coincident(g8,g7)
    c: Coincident(g9,g-6)
    c: Tangent(g9,g-7) = 1.5708
    c: Tangent(g9,g8) = -1.5708
    c: Horizontal(g8,g9)
    c: Coincident(g10,g1)
    c: Coincident(g10,g9)
    c: Coincident(g11,g-4)
    c: Tangent(g11,g-4)
    c: Coincident(g12,g-3)
    c: Tangent(g12,g-3)
    c: Coincident(g13,g9)
    c: Coincident(g14,g6)
    c: PointOnObject(g15,g-5)
    c: PointOnObject(g15,g14)
    c: PointOnObject(g16,g-6)
    c: PointOnObject(g16,g13)
    c: Vertical(g15,g6)
    c: Vertical(g16,g9)
FEATURE [PartDesign::Pad] Pad
  Direction = (0,0,1)
  Length = 3
  Length2 = 10
  Placement = pos=(-16.5,16.5,-29.5) rot=(0,0,-1;1.5708rad)
  Profile = -> Sketch
  ReferenceAxis = -> Sketch [N_Axis]
  Type = 0
FEATURE [Sketcher::SketchObject] Sketch001
  ExternalGeometry = -> [Pad]
  FullyConstrained = true
  MapMode = 5
  Placement = pos=(8.7,16.5,-29.5) rot=(0.57735,0.57735,0.57735;2.0944rad)
  Support = -> [Pad]
  expr: .Constraints.Rad = 3
  expr: Constraints[25] = .Constraints.Rad
  expr: Constraints[26] = .Constraints.Rad
  expr: Constraints[27] = .Constraints.Rad
  expr: Constraints[30] = <<Datasheet>>#<<mgn9c>>.Dim_C
  expr: Constraints[31] = <<Datasheet>>#<<mgn9c>>.Dim_B
  expr: Constraints[8] = <<Datasheet>>#<<mgn9c>>.Dim_L1
  expr: Constraints[9] = <<Datasheet>>#<<mgn9c>>.Dim_W
  sketch-geometry (14):
    g0: LineSegment StartX=-9.45 StartY=9.5 StartZ=0 EndX=9.45 EndY=9.5 EndZ=0
    g1: LineSegment StartX=9.45 StartY=9.5 StartZ=0 EndX=9.45 EndY=29.5 EndZ=0
    g2: LineSegment StartX=9.45 StartY=29.5 StartZ=0 EndX=-9.45 EndY=29.5 EndZ=0
    g3: LineSegment StartX=-9.45 StartY=29.5 StartZ=0 EndX=-9.45 EndY=9.5 EndZ=0
    g4: GeomPoint X=1.9e-15 Y=29.5 Z=0
    g5: Circle CenterX=-5 CenterY=27 CenterZ=0 NormalX=0 NormalY=0 NormalZ=1 AngleXU=0 Radius=1.5
    g6: Circle CenterX=5 CenterY=27 CenterZ=0 NormalX=0 NormalY=0 NormalZ=1 AngleXU=0 Radius=1.5
    g7: Circle CenterX=-5 CenterY=12 CenterZ=0 NormalX=0 NormalY=0 NormalZ=1 AngleXU=0 Radius=1.5
    g8: Circle CenterX=5 CenterY=12 CenterZ=0 NormalX=0 NormalY=0 NormalZ=1 AngleXU=0 Radius=1.5
    g9: LineSegment StartX=-5 StartY=12 StartZ=0 EndX=5 EndY=12 EndZ=0
    g10: LineSegment StartX=5 StartY=12 StartZ=0 EndX=5 EndY=27 EndZ=0
    g11: LineSegment StartX=5 StartY=27 StartZ=0 EndX=-5 EndY=27 EndZ=0
    g12: LineSegment StartX=-5 StartY=27 StartZ=0 EndX=-5 EndY=12 EndZ=0
    g13: GeomPoint X=1.8e-15 Y=19.5 Z=0
  constraints (32):
    c: Coincident(g0,g1)
    c: Coincident(g1,g2)
    c: Coincident(g2,g3)
    c: Coincident(g3,g0)
    c: Horizontal(g0)
    c: Horizontal(g2)
    c: Vertical(g1)
    c: Vertical(g3)
    c: DistanceX(g2,g2) = 18.9
    c: DistanceY(g1,g1) = 20
    c: Symmetric(g-3,g-4,g4)
    c: Symmetric(g2,g1,g4)
    c: Coincident(g9,g10)
    c: Coincident(g10,g11)
    c: Coincident(g11,g12)
    c: Coincident(g12,g9)
    c: Horizontal(g9)
    c: Horizontal(g11)
    c: Vertical(g10)
    c: Vertical(g12)
    c: Coincident(g9,g7)
    c: Coincident(g10,g6)
    c: Coincident(g5,g11)
    c: Coincident(g8,g9)
    c: Diameter(g7) = 3  'Rad'
    c: Diameter(g8) = 3
    c: Diameter(g6) = 3
    c: Diameter(g5) = 3
    c: Symmetric(g1,g0,g13)
    c: Symmetric(g7,g6,g13)
    c: DistanceX(g11,g11) = 10
    c: DistanceY(g10,g10) = 15
FEATURE [PartDesign::Pad] Pad001
  BaseFeature = -> Pad
  Direction = (1,4e-16,0)
  Length = 5
  Length2 = 10
  Placement = pos=(-16.5,16.5,-29.5) rot=(0,0,-1;1.5708rad)
  Profile = -> Sketch001
  ReferenceAxis = -> Sketch001 [N_Axis]
  Reversed = true
  Type = 0
  expr: Length = <<Sketch>>.Constraints.Strength
FEATURE [Sketcher::SketchObject] Sketch002
  ExternalGeometry = -> [Pad001]
  FullyConstrained = true
  MapMode = 5
  Placement = pos=(3.7,16.5,-29.5) rot=(0.57735,-0.57735,-0.57735;2.0944rad)
  Support = -> [Pad001]
  sketch-geometry (4):
    g0: LineSegment StartX=-9.45 StartY=9.5 StartZ=0 EndX=-7.45 EndY=9.5 EndZ=0
    g1: LineSegment StartX=-7.45 StartY=9.5 StartZ=0 EndX=-7.45 EndY=7.5 EndZ=0
    g2: LineSegment StartX=-7.45 StartY=7.5 StartZ=0 EndX=-9.45 EndY=7.5 EndZ=0
    g3: LineSegment StartX=-9.45 StartY=7.5 StartZ=0 EndX=-9.45 EndY=9.5 EndZ=0
  constraints (11):
    c: Coincident(g0,g1)
    c: Coincident(g1,g2)
    c: Coincident(g2,g3)
    c: Coincident(g3,g0)
    c: Horizontal(g0)
    c: Horizontal(g2)
    c: Vertical(g1)
    c: Vertical(g3)
    c: DistanceX(g2,g2) = 2
    c: Coincident(g0,g-3)
    c: DistanceY(g1,g1) = 2
FEATURE [PartDesign::Pad] Pad002
  BaseFeature = -> Pad001
  Direction = (-1,-4e-16,0)
  Length = 13
  Length2 = 10
  Placement = pos=(-16.5,16.5,-29.5) rot=(0,0,-1;1.5708rad)
  Profile = -> Sketch002
  ReferenceAxis = -> Sketch002 [N_Axis]
  Reversed = true
  Type = 0
  expr: Length = <<Pad001>>.Length + <<Datasheet>>#<<mgn9c>>.Dim_H - <<Datasheet>>#<<mgn9c>>.Dim_H1
FEATURE [Sketcher::SketchObject] Sketch003
  ExternalGeometry = -> [Pad002]
  FullyConstrained = true
  MapMode = 5
  Placement = pos=(16.7,16.5,-29.5) rot=(0.57735,0.57735,0.57735;2.0944rad)
  Support = -> [Pad002]
  expr: Constraints[17] = <<NormalConnectorMagnet>>#<<Sketch002>>.Constraints.SlideToMagnetCenter
  sketch-geometry (13):
    g0: LineSegment StartX=9.45 StartY=9.5 StartZ=0 EndX=4.45 EndY=9.5 EndZ=0
    g1: LineSegment StartX=4.45 StartY=9.5 StartZ=0 EndX=4.45 EndY=2.35 EndZ=0
    g2: LineSegment StartX=4.45 StartY=2.35 StartZ=0 EndX=9.45 EndY=2.35 EndZ=0
    g3: LineSegment StartX=9.45 StartY=2.35 StartZ=0 EndX=9.45 EndY=9.5 EndZ=0
    g4: Circle CenterX=6.95 CenterY=4.85 CenterZ=0 NormalX=0 NormalY=0 NormalZ=1 AngleXU=0 Radius=1.5
    g5: GeomPoint X=8.45 Y=4.85 Z=0
    g6: GeomPoint X=6.95 Y=3.35 Z=0
    g7: LineSegment StartX=6.95 StartY=3.35 StartZ=0 EndX=6.95 EndY=2.35 EndZ=0
    g8: LineSegment StartX=7.45 StartY=7.5 StartZ=0 EndX=4.45 EndY=6.35 EndZ=0
    g9: LineSegment StartX=4.45 StartY=6.35 StartZ=0 EndX=4.45 EndY=2.35 EndZ=0
    g10: GeomPoint X=6.95 Y=6.35 Z=0
    g11: LineSegment StartX=7.45 StartY=9.5 StartZ=0 EndX=9.45 EndY=9.5 EndZ=0
    g12: LineSegment StartX=7.45 StartY=7.5 StartZ=0 EndX=7.45 EndY=9.5 EndZ=0
  constraints (32):
    c: Coincident(g0,g1)
    c: Coincident(g1,g2)
    c: Coincident(g2,g3)
    c: Coincident(g3,g0)
    c: Horizontal(g0)
    c: Horizontal(g2)
    c: Vertical(g1)
    c: Vertical(g3)
    c: PointOnObject(g-3,g3)
    c: PointOnObject(g-4,g0)
    c: Diameter(g4) = 3
    c: PointOnObject(g5,g4)
    c: DistanceX(g5,g0) = 1
    c: PointOnObject(g6,g4)
    c: DistanceY(g2,g6) = 1
    c: Horizontal(g5,g4)
    c: Vertical(g4,g6)
    c: DistanceY(g4,g0) = 4.65
    c: Coincident(g7,g6)
    c: Vertical(g7)
    c: Symmetric(g1,g2,g7)
    c: Coincident(g8,g-4)
    c: PointOnObject(g8,g1)
    c: Coincident(g9,g8)
    c: Coincident(g9,g2)
    c: PointOnObject(g10,g4)
    c: Vertical(g10,g4)
    c: Horizontal(g8,g10)
    c: Coincident(g12,g11)
    c: Coincident(g11,g-4)
    c: Coincident(g0,g11)
    c: Coincident(g8,g12)
FEATURE [PartDesign::Pad] Pad003
  BaseFeature = -> Pad002
  Direction = (1,4e-16,0)
  Length = 2
  Length2 = 10
  Placement = pos=(-16.5,16.5,-29.5) rot=(0,0,-1;1.5708rad)
  Profile = -> Sketch003
  ReferenceAxis = -> Sketch003 [N_Axis]
  Reversed = true
  Type = 0
  expr: Length = <<NormalConnectorMagnet>>#<<Pad002>>.Length
FEATURE [Sketcher::SketchObject] Sketch004
  ExternalGeometry = -> [Pad003]
  FullyConstrained = true
  MapMode = 5
  Placement = pos=(14.7,16.5,-29.5) rot=(0.57735,-0.57735,-0.57735;2.0944rad)
  Support = -> [Pad003]
  expr: Constraints[1] = <<NormalConnectorMagnet>>#<<Sketch003>>.Constraints.MagnetDiameter
  sketch-geometry (1):
    g0: Circle CenterX=-6.95 CenterY=4.85 CenterZ=0 NormalX=0 NormalY=0 NormalZ=1 AngleXU=0 Radius=2
  constraints (2):
    c: Coincident(g0,g-3)
    c: Diameter(g0) = 4
FEATURE [PartDesign::Pocket] Pocket
  BaseFeature = -> Pad003
  Direction = (1,0,0)
  Length = 1
  Length2 = 5
  Placement = pos=(-16.5,16.5,-29.5) rot=(0,0,-1;1.5708rad)
  Profile = -> Sketch004
  ReferenceAxis = -> Sketch004 [N_Axis]
  Type = 0
FEATURE [Sketcher::SketchObject] Sketch005
  ExternalGeometry = -> [Pocket]
  FullyConstrained = true
  MapMode = 5
  Placement = pos=(3.7,16.5,-29.5) rot=(0.57735,-0.57735,-0.57735;2.0944rad)
  Support = -> [Pocket]
  expr: Constraints[1] = <<Datasheet>>#<<mgn9c>>.Dim_D
  expr: Constraints[5] = <<Datasheet>>#<<mgn9c>>.Dim_D
  expr: Constraints[6] = <<Datasheet>>#<<mgn9c>>.Dim_D
  expr: Constraints[7] = <<Datasheet>>#<<mgn9c>>.Dim_D
  sketch-geometry (14):
    g0: Circle CenterX=-5 CenterY=27 CenterZ=0 NormalX=0 NormalY=0 NormalZ=1 AngleXU=0 Radius=3
    g1: Circle CenterX=5 CenterY=27 CenterZ=0 NormalX=0 NormalY=0 NormalZ=1 AngleXU=0 Radius=3
    g2: Circle CenterX=5 CenterY=12 CenterZ=0 NormalX=0 NormalY=0 NormalZ=1 AngleXU=0 Radius=3
    g3: Circle CenterX=-5 CenterY=12 CenterZ=0 NormalX=0 NormalY=0 NormalZ=1 AngleXU=0 Radius=3
    g4: ArcOfCircle CenterX=-5 CenterY=12 CenterZ=0 NormalX=0 NormalY=0 NormalZ=1 AngleXU=0 Radius=3 StartAngle=2.26252e-07 EndAngle=3.14159
    g5: ArcOfCircle CenterX=5 CenterY=12 CenterZ=0 NormalX=0 NormalY=0 NormalZ=1 AngleXU=0 Radius=3 StartAngle=6.28318 EndAngle=9.42479
    g6: LineSegment StartX=2 StartY=9.5 StartZ=0 EndX=8 EndY=9.5 EndZ=0
    g7: LineSegment StartX=8 StartY=9.5 StartZ=0 EndX=8 EndY=12 EndZ=0
    g8: LineSegment StartX=8 StartY=12 StartZ=0 EndX=2 EndY=12 EndZ=0
    g9: LineSegment StartX=2 StartY=12 StartZ=0 EndX=2 EndY=9.5 EndZ=0
    g10: LineSegment StartX=-2 StartY=7.5 StartZ=0 EndX=-8 EndY=7.5 EndZ=0
    g11: LineSegment StartX=-8 StartY=7.5 StartZ=0 EndX=-8 EndY=12 EndZ=0
    g12: LineSegment StartX=-8 StartY=12 StartZ=0 EndX=-2 EndY=12 EndZ=0
    g13: LineSegment StartX=-2 StartY=12 StartZ=0 EndX=-2 EndY=7.5 EndZ=0
  constraints (36):
    c: Coincident(g0,g-3)
    c: Diameter(g0) = 6
    c: Coincident(g1,g-4)
    c: Coincident(g2,g-5)
    c: Coincident(g3,g-6)
    c: Diameter(g1) = 6
    c: Diameter(g2) = 6
    c: Diameter(g3) = 6
    c: Coincident(g4,g3)
    c: PointOnObject(g4,g3)
    c: Coincident(g5,g2)
    c: PointOnObject(g5,g2)
    c: Coincident(g6,g7)
    c: Coincident(g7,g8)
    c: Coincident(g8,g9)
    c: Coincident(g9,g6)
    c: Horizontal(g6)
    c: Horizontal(g8)
    c: Vertical(g7)
    c: Vertical(g9)
    c: Coincident(g7,g5)
    c: PointOnObject(g6,g-7)
    c: Coincident(g5,g8)
    c: Coincident(g10,g11)
    c: Coincident(g11,g12)
    c: Coincident(g12,g13)
    c: Coincident(g13,g10)
    c: Horizontal(g10)
    c: Horizontal(g12)
    c: Vertical(g11)
    c: Vertical(g13)
    c: Coincident(g11,g4)
    c: Coincident(g4,g12)
    c: Tangent(g13,g4)
    c: Tangent(g9,g5)
    c: PointOnObject(g-8,g10)
FEATURE [PartDesign::Pocket] Pocket001
  BaseFeature = -> Pocket
  Direction = (1,9e-16,0)
  Length = 3
  Length2 = 5
  Placement = pos=(-16.5,16.5,-29.5) rot=(0,0,-1;1.5708rad)
  Profile = -> Sketch005
  ReferenceAxis = -> Sketch005 [N_Axis]
  Type = 4
  expr: Length = <<Pad001>>.Length - 2 mm
FEATURE [PartDesign::Body] Body  label="JoystickHolder"
  Group = -> [Binder,Binder001,Sketch,Pad,Sketch001,Pad001,Sketch002,Pad002,Sketch003,Pad003,Sketch004,Pocket,Sketch005,Pocket001]
  Origin = -> Origin
  Placement = pos=(0,0,-4) rot=(0,0,1;0rad)
  Tip = -> Pocket001
---- part parts/MG/mgn9c_13.FCStd = doc fcstd_af4c73f2d28f ----
FCSTD DOCUMENT  (FreeCAD 0.21R33668 +26 (Git))
Label: mgn9c_13
License: All rights reserved
LicenseURL: http://en.wikipedia.org/wiki/All_rights_reserved
objects: Sketcher::SketchObject×2, App::Link×1, PartDesign::Pad×1, PartDesign::Pocket×1, PartDesign::LinearPattern×1, PartDesign::Body×1
note: 8 computed .brp shape members not serialized (recipe doc carries the construction recipe); baked Part::Feature solids carry a one-line shape summary decoded from their .brp
EXTERNAL_REF file=Datasheet.FCStd obj=Spreadsheet

FEATURE [App::Link] Link  label="mgn9c"
  LinkedObject = -> <external Datasheet.FCStd>#Spreadsheet
FEATURE [Sketcher::SketchObject] Sketch
  Base_Number_Holes = 13
  FullyConstrained = true
  MapMode = 5
  Support = -> [XY_Plane]
  expr: Constraints[10] = <<mgn9c>>.Dim_Wr
  sketch-geometry (4):
    g0: LineSegment StartX=0 StartY=0 StartZ=0 EndX=255 EndY=0 EndZ=0
    g1: LineSegment StartX=255 StartY=0 StartZ=0 EndX=255 EndY=9 EndZ=0
    g2: LineSegment StartX=255 StartY=9 StartZ=0 EndX=0 EndY=9 EndZ=0
    g3: LineSegment StartX=0 StartY=9 StartZ=0 EndX=0 EndY=0 EndZ=0
  constraints (11):
    c: Coincident(g0,g1)
    c: Coincident(g1,g2)
    c: Coincident(g2,g3)
    c: Coincident(g3,g0)
    c: Horizontal(g0)
    c: Horizontal(g2)
    c: Vertical(g1)
    c: Vertical(g3)
    c: Coincident(g0,g-1)
    c: DistanceX(g2,g2) = 255  'Rail_Length'
    c: DistanceY(g3,g3) = 9
FEATURE [PartDesign::Pad] Pad
  Direction = (0,0,1)
  Length = 6.5
  Length2 = 10
  Profile = -> Sketch
  ReferenceAxis = -> Sketch [N_Axis]
  Type = 0
  expr: Length = <<mgn9c>>.Dim_Hr
FEATURE [Sketcher::SketchObject] Sketch001
  FullyConstrained = true
  MapMode = 5
  Placement = pos=(0,0,6.5) rot=(0,0,1;0rad)
  Support = -> [Pad]
  expr: Constraints[0] = <<mgn9c>>.Dim_E
  expr: Constraints[1] = <<mgn9c>>.Dim_Wr / 2
  expr: Constraints[2] = <<mgn9c>>.Dim_d
  sketch-geometry (1):
    g0: Circle CenterX=7.5 CenterY=4.5 CenterZ=0 NormalX=0 NormalY=0 NormalZ=1 AngleXU=0 Radius=1.75
  constraints (3):
    c: DistanceX(g-1,g0) = 7.5
    c: DistanceY(g-1,g0) = 4.5
    c: Diameter(g0) = 3.5
FEATURE [PartDesign::Pocket] Pocket
  BaseFeature = -> Pad
  Direction = (0,0,-1)
  Length = 6.5
  Length2 = 5
  Profile = -> Sketch001
  ReferenceAxis = -> Sketch001 [N_Axis]
  Type = 0
  expr: Length = <<mgn9c>>.Dim_Hr
FEATURE [PartDesign::LinearPattern] LinearPattern
  BaseFeature = -> Pocket
  Direction = -> Sketch001 [H_Axis]
  Length = 240
  Occurrences = 13
  Originals = -> [Pocket]
  expr: Length = <<Sketch>>.Constraints.Rail_Length - <<mgn9c>>.Dim_E * 2
  expr: Occurrences = <<Sketch>>.Base_Number_Holes
FEATURE [PartDesign::Body] Body  label="Rail"
  Group = -> [Sketch,Pad,Sketch001,Pocket,LinearPattern]
  Origin = -> Origin
  Tip = -> LinearPattern
---- part parts/MG/mgn9c_slide.FCStd = doc fcstd_17b450fab925 ----
FCSTD DOCUMENT  (FreeCAD 0.21R33668 +26 (Git))
Label: mgn9c_slide
License: All rights reserved
LicenseURL: http://en.wikipedia.org/wiki/All_rights_reserved
objects: Sketcher::SketchObject×4, PartDesign::Pocket×3, App::Link×1, PartDesign::Pad×1, PartDesign::Body×1
note: 13 computed .brp shape members not serialized (recipe doc carries the construction recipe); baked Part::Feature solids carry a one-line shape summary decoded from their .brp
EXTERNAL_REF file=Datasheet.FCStd obj=Spreadsheet

FEATURE [App::Link] Link  label="mgn9c"
  LinkedObject = -> <external Datasheet.FCStd>#Spreadsheet
FEATURE [Sketcher::SketchObject] Sketch002
  FullyConstrained = true
  MapMode = 5
  Support = -> [XY_Plane001]
  expr: Constraints[10] = <<mgn9c>>.Dim_W
  expr: Constraints[9] = <<mgn9c>>.Dim_L
  sketch-geometry (4):
    g0: LineSegment StartX=0 StartY=0 StartZ=0 EndX=28.9 EndY=0 EndZ=0
    g1: LineSegment StartX=28.9 StartY=0 StartZ=0 EndX=28.9 EndY=20 EndZ=0
    g2: LineSegment StartX=28.9 StartY=20 StartZ=0 EndX=0 EndY=20 EndZ=0
    g3: LineSegment StartX=0 StartY=20 StartZ=0 EndX=0 EndY=0 EndZ=0
  constraints (11):
    c: Coincident(g0,g1)
    c: Coincident(g1,g2)
    c: Coincident(g2,g3)
    c: Coincident(g3,g0)
    c: Horizontal(g0)
    c: Horizontal(g2)
    c: Vertical(g1)
    c: Vertical(g3)
    c: Coincident(g0,g-1)
    c: DistanceX(g2,g2) = 28.9
    c: DistanceY(g1,g1) = 20
FEATURE [PartDesign::Pad] Pad001
  Direction = (0,0,1)
  Length = 8
  Length2 = 10
  Profile = -> Sketch002
  ReferenceAxis = -> Sketch002 [N_Axis]
  Type = 0
  expr: Length = <<mgn9c>>.Dim_H - <<mgn9c>>.Dim_H1
FEATURE [Sketcher::SketchObject] Sketch003
  ExternalGeometry = -> [Pad001]
  FullyConstrained = true
  MapMode = 5
  Placement = pos=(0,0,0) rot=(0.57735,-0.57735,-0.57735;2.0944rad)
  Support = -> [Pad001]
  expr: Constraints[10] = <<mgn9c>>.Dim_Hr - <<mgn9c>>.Dim_H1
  expr: Constraints[8] = <<mgn9c>>.Dim_N
  expr: Constraints[9] = <<mgn9c>>.Dim_N
  sketch-geometry (4):
    g0: LineSegment StartX=-14.5 StartY=0 StartZ=0 EndX=-5.5 EndY=0 EndZ=0
    g1: LineSegment StartX=-5.5 StartY=0 StartZ=0 EndX=-5.5 EndY=4.5 EndZ=0
    g2: LineSegment StartX=-5.5 StartY=4.5 StartZ=0 EndX=-14.5 EndY=4.5 EndZ=0
    g3: LineSegment StartX=-14.5 StartY=4.5 StartZ=0 EndX=-14.5 EndY=0 EndZ=0
  constraints (12):
    c: Coincident(g0,g1)
    c: Coincident(g1,g2)
    c: Coincident(g2,g3)
    c: Coincident(g3,g0)
    c: Horizontal(g0)
    c: Horizontal(g2)
    c: Vertical(g1)
    c: Vertical(g3)
    c: DistanceX(g-5,g0) = 5.5
    c: DistanceX(g0,g-6) = 5.5
    c: DistanceY(g1,g1) = 4.5
    c: PointOnObject(g0,g-5)
FEATURE [PartDesign::Pocket] Pocket001
  BaseFeature = -> Pad001
  Direction = (1,0,0)
  Length = 28.9
  Length2 = 5
  Profile = -> Sketch003
  ReferenceAxis = -> Sketch003 [N_Axis]
  Type = 0
  expr: Length = <<mgn9c>>.Dim_L
FEATURE [Sketcher::SketchObject] Sketch004
  ExternalGeometry = -> [Pocket001]
  FullyConstrained = true
  MapMode = 5
  Placement = pos=(0,0,8) rot=(0,0,1;0rad)
  Support = -> [Pocket001]
  expr: Constraints[17] = 3
  expr: Constraints[18] = 3
  expr: Constraints[19] = 3
  expr: Constraints[20] = 3
  expr: Constraints[8] = <<mgn9c>>.Dim_C
  expr: Constraints[9] = <<mgn9c>>.Dim_B
  sketch-geometry (9):
    g0: LineSegment StartX=9.45 StartY=17.5 StartZ=0 EndX=19.45 EndY=17.5 EndZ=0
    g1: LineSegment StartX=19.45 StartY=17.5 StartZ=0 EndX=19.45 EndY=2.5 EndZ=0
    g2: LineSegment StartX=19.45 StartY=2.5 StartZ=0 EndX=9.45 EndY=2.5 EndZ=0
    g3: LineSegment StartX=9.45 StartY=2.5 StartZ=0 EndX=9.45 EndY=17.5 EndZ=0
    g4: GeomPoint X=14.45 Y=10 Z=0
    g5: Circle CenterX=9.45 CenterY=17.5 CenterZ=0 NormalX=0 NormalY=0 NormalZ=1 AngleXU=0 Radius=1.5
    g6: Circle CenterX=19.45 CenterY=17.5 CenterZ=0 NormalX=0 NormalY=0 NormalZ=1 AngleXU=0 Radius=1.5
    g7: Circle CenterX=19.45 CenterY=2.5 CenterZ=0 NormalX=0 NormalY=0 NormalZ=1 AngleXU=0 Radius=1.5
    g8: Circle CenterX=9.45 CenterY=2.5 CenterZ=0 NormalX=0 NormalY=0 NormalZ=1 AngleXU=0 Radius=1.5
  constraints (21):
    c: Coincident(g0,g1)
    c: Coincident(g1,g2)
    c: Coincident(g2,g3)
    c: Coincident(g3,g0)
    c: Horizontal(g0)
    c: Horizontal(g2)
    c: Vertical(g1)
    c: Vertical(g3)
    c: DistanceX(g0,g0) = 10
    c: DistanceY(g1,g1) = 15
    c: DistanceY(g-4,g2) = 2.5
    c: Symmetric(g-3,g-4,g4)
    c: Symmetric(g1,g0,g4)
    c: Coincident(g5,g0)
    c: Coincident(g6,g0)
    c: Coincident(g7,g1)
    c: Coincident(g8,g2)
    c: Diameter(g8) = 3
    c: Diameter(g7) = 3
    c: Diameter(g6) = 3
    c: Diameter(g5) = 3
FEATURE [PartDesign::Pocket] Pocket002
  BaseFeature = -> Pocket001
  Direction = (0,0,-1)
  Length = 3
  Length2 = 5
  Profile = -> Sketch004
  ReferenceAxis = -> Sketch004 [N_Axis]
  Type = 0
FEATURE [Sketcher::SketchObject] Sketch005
  ExternalGeometry = -> [Pocket002]
  FullyConstrained = true
  MapMode = 5
  Placement = pos=(0,0,8) rot=(0,0,1;0rad)
  Support = -> [Pocket002]
  expr: Constraints[19] = <<mgn9c>>.Dim_L1
  sketch-geometry (9):
    g0: LineSegment StartX=0 StartY=20 StartZ=0 EndX=5 EndY=20 EndZ=0
    g1: LineSegment StartX=5 StartY=20 StartZ=0 EndX=5 EndY=0 EndZ=0
    g2: LineSegment StartX=5 StartY=0 StartZ=0 EndX=0 EndY=0 EndZ=0
    g3: LineSegment StartX=0 StartY=0 StartZ=0 EndX=0 EndY=20 EndZ=0
    g4: LineSegment StartX=28.9 StartY=0 StartZ=0 EndX=23.9 EndY=0 EndZ=0
    g5: LineSegment StartX=23.9 StartY=0 StartZ=0 EndX=23.9 EndY=20 EndZ=0
    g6: LineSegment StartX=23.9 StartY=20 StartZ=0 EndX=28.9 EndY=20 EndZ=0
    g7: LineSegment StartX=28.9 StartY=20 StartZ=0 EndX=28.9 EndY=0 EndZ=0
    g8: GeomPoint X=14.45 Y=0 Z=0
  constraints (22):
    c: Coincident(g0,g1)
    c: Coincident(g1,g2)
    c: Coincident(g2,g3)
    c: Coincident(g3,g0)
    c: Horizontal(g0)
    c: Horizontal(g2)
    c: Vertical(g1)
    c: Vertical(g3)
    c: Coincident(g0,g-3)
    c: PointOnObject(g1,g-1)
    c: Coincident(g4,g5)
    c: Coincident(g5,g6)
    c: Coincident(g6,g7)
    c: Coincident(g7,g4)
    c: Horizontal(g6)
    c: Vertical(g5)
    c: Vertical(g7)
    c: Symmetric(g2,g-4,g8)
    c: Symmetric(g4,g1,g8)
    c: DistanceX(g1,g4) = 18.9
    c: PointOnObject(g5,g-5)
    c: Coincident(g4,g-4)
FEATURE [PartDesign::Pocket] Pocket003
  BaseFeature = -> Pocket002
  Direction = (0,0,-1)
  Length = 0.1
  Length2 = 5
  Profile = -> Sketch005
  ReferenceAxis = -> Sketch005 [N_Axis]
  Type = 0
FEATURE [PartDesign::Body] Body001  label="Slide"
  Group = -> [Sketch002,Pad001,Sketch003,Pocket001,Sketch004,Pocket002,Sketch005,Pocket003]
  Origin = -> Origin001
  Tip = -> Pocket003
---- part parts/MagnetoPot/MagnetoPot.FCStd = doc fcstd_ba503c3fc88b ----
FCSTD DOCUMENT  (FreeCAD 0.21R33668 +26 (Git))
Label: MagnetoPot
License: All rights reserved
LicenseURL: http://en.wikipedia.org/wiki/All_rights_reserved
objects: Sketcher::SketchObject×2, PartDesign::Pad×1, PartDesign::Body×1
note: 5 computed .brp shape members not serialized (recipe doc carries the construction recipe); baked Part::Feature solids carry a one-line shape summary decoded from their .brp

FEATURE [Sketcher::SketchObject] Sketch
  FullyConstrained = true
  MapMode = 5
  Support = -> [XY_Plane]
  sketch-geometry (17):
    g0: LineSegment StartX=0 StartY=0 StartZ=0 EndX=215.86 EndY=0 EndZ=0
    g1: LineSegment StartX=215.86 StartY=0 StartZ=0 EndX=215.86 EndY=20.3 EndZ=0
    g2: LineSegment StartX=215.86 StartY=20.3 StartZ=0 EndX=0 EndY=20.3 EndZ=0
    g3: LineSegment StartX=0 StartY=20.3 StartZ=0 EndX=0 EndY=0 EndZ=0
    g4: LineSegment StartX=7.93 StartY=8.245 StartZ=0 EndX=207.93 EndY=8.245 EndZ=0
    g5: LineSegment StartX=207.93 StartY=8.245 StartZ=0 EndX=207.93 EndY=12.055 EndZ=0
    g6: LineSegment StartX=207.93 StartY=12.055 StartZ=0 EndX=7.93 EndY=12.055 EndZ=0
    g7: LineSegment StartX=7.93 StartY=12.055 StartZ=0 EndX=7.93 EndY=8.245 EndZ=0
    g8: GeomPoint X=107.93 Y=10.15 Z=0
    g9: LineSegment StartX=-24.89 StartY=15.23 StartZ=0 EndX=0 EndY=15.23 EndZ=0
    g10: LineSegment StartX=0 StartY=15.23 StartZ=0 EndX=0 EndY=5.07 EndZ=0
    g11: LineSegment StartX=0 StartY=5.07 StartZ=0 EndX=-24.89 EndY=5.07 EndZ=0
    g12: LineSegment StartX=-24.89 StartY=5.07 StartZ=0 EndX=-24.89 EndY=15.23 EndZ=0
    g13: LineSegment StartX=0 StartY=20.3 StartZ=0 EndX=0 EndY=15.23 EndZ=0
    g14: LineSegment StartX=0 StartY=5.07 StartZ=0 EndX=0 EndY=0 EndZ=0
    g15: GeomPoint X=0 Y=10.15 Z=0
    g16: LineSegment StartX=215.86 StartY=20.3 StartZ=0 EndX=215.86 EndY=0 EndZ=0
  constraints (42):
    c: Coincident(g0,g1)
    c: Coincident(g1,g2)
    c: Coincident(g2,g3)
    c: Coincident(g3,g0)
    c: Horizontal(g0)
    c: Horizontal(g2)
    c: Vertical(g1)
    c: Vertical(g3)
    c: Coincident(g0,g-1)
    c: DistanceX(g2,g2) = 215.86  'PartLength'
    c: DistanceY(g3,g3) = 20.3  'PartWidth'
    c: Coincident(g4,g5)
    c: Coincident(g5,g6)
    c: Coincident(g6,g7)
    c: Coincident(g7,g4)
    c: Horizontal(g4)
    c: Horizontal(g6)
    c: Vertical(g5)
    c: Vertical(g7)
    c: Symmetric(g2,g0,g8)
    c: Symmetric(g4,g5,g8)
    c: DistanceY(g5,g5) = 3.81  'ActiveWidth'
    c: DistanceX(g6,g6) = 200  'ActiveLength'
    c: Coincident(g9,g10)
    c: Coincident(g10,g11)
    c: Coincident(g11,g12)
    c: Coincident(g12,g9)
    c: Horizontal(g9)
    c: Horizontal(g11)
    c: Vertical(g10)
    c: Vertical(g12)
    c: Coincident(g13,g2)
    c: Coincident(g13,g9)
    c: Coincident(g14,g11)
    c: Coincident(g14,g0)
    c: Symmetric(g2,g0,g15)
    c: Symmetric(g9,g11,g15)
    c: DistanceX(g9,g9) = 24.89  'TailLength'
    c: DistanceY(g12,g12) = 10.16  'TailWidth'
    c: Coincident(g16,g2)
    c: Coincident(g16,g0)
    c: DistanceY(g0,g4) = 8.245  'EdgeToActiveWidth'
FEATURE [PartDesign::Pad] Pad
  Direction = (0,0,1)
  Length = 3.5
  Length2 = 10
  Profile = -> Sketch
  ReferenceAxis = -> Sketch [N_Axis]
  Type = 0
FEATURE [Sketcher::SketchObject] Sketch001
  ExternalGeometry = -> [Pad]
  FullyConstrained = true
  MapMode = 5
  Placement = pos=(0,0,0) rot=(1,0,0;1.5708rad)
  Support = -> [Pad]
  constraints (1):
    c: DistanceY(g-1,g-3) = 3.5  'Height'
FEATURE [PartDesign::Body] Body  label="MP1_L_0200_103_5_ST"
  Group = -> [Sketch,Pad,Sketch001]
  Origin = -> Origin
  Tip = -> Pad
---- part parts/NormalConnectorMagnet.FCStd = doc fcstd_d9057e67e4f8 ----
FCSTD DOCUMENT  (FreeCAD 0.21R33668 +26 (Git))
Label: NormalConnectorMagnet
License: All rights reserved
LicenseURL: http://en.wikipedia.org/wiki/All_rights_reserved
objects: Sketcher::SketchObject×26, PartDesign::Pocket×17, PartDesign::Pad×8, PartDesign::SubShapeBinder×2, PartDesign::Body×2
note: 80 computed .brp shape members not serialized (recipe doc carries the construction recipe); baked Part::Feature solids carry a one-line shape summary decoded from their .brp
EXTERNAL_REF file=MG/mgn9c_slide.FCStd obj=Body001
EXTERNAL_REF file=BaseMagnetoPot.FCStd obj=Sketch
EXTERNAL_REF file=MG/Datasheet.FCStd obj=Spreadsheet
EXTERNAL_REF file=BaseMagnetoPot.FCStd obj=Sketch001
EXTERNAL_REF file=MG/mgn9c_13.FCStd obj=Sketch

FEATURE [PartDesign::SubShapeBinder] Binder  label="Slide"
  BindCopyOnChange = 0
  BindMode = 0
  ClaimChildren = false
  Context = -> Body [Binder.]
  Fuse = false
  MakeFace = true
  OffsetFill = false
  OffsetIntersection = false
  OffsetJoinType = 0
  OffsetOpenResult = false
  PartialLoad = false
  Relative = true
  Support = -> [<external MG/mgn9c_slide.FCStd>#Body001]
  _Version = 2
FEATURE [Sketcher::SketchObject] Sketch
  ExternalGeometry = -> [Binder]
  FullyConstrained = true
  MapMode = 5
  Placement = pos=(0,0,8) rot=(0,0,1;0rad)
  Support = -> [Binder]
  expr: Constraints[5] = .Constraints.Rad
  expr: Constraints[6] = .Constraints.Rad
  sketch-geometry (7):
    g0: Circle CenterX=19.45 CenterY=17.5 CenterZ=0 NormalX=0 NormalY=0 NormalZ=1 AngleXU=0 Radius=1.5
    g1: Circle CenterX=9.45 CenterY=2.5 CenterZ=0 NormalX=0 NormalY=0 NormalZ=1 AngleXU=0 Radius=1.5
    g2: Circle CenterX=19.45 CenterY=2.5 CenterZ=0 NormalX=0 NormalY=0 NormalZ=1 AngleXU=0 Radius=1.5
    g3: LineSegment StartX=5 StartY=20 StartZ=0 EndX=23.9 EndY=20 EndZ=0
    g4: LineSegment StartX=23.9 StartY=20 StartZ=0 EndX=23.9 EndY=0 EndZ=0
    g5: LineSegment StartX=23.9 StartY=0 StartZ=0 EndX=5 EndY=0 EndZ=0
    g6: LineSegment StartX=5 StartY=0 StartZ=0 EndX=5 EndY=20 EndZ=0
  constraints (17):
    c: Coincident(g0,g-5)
    c: PointOnObject(g-4,g0)
    c: Coincident(g1,g-6)
    c: Coincident(g2,g-7)
    c: Diameter(g0) = 3  'Rad'
    c: Diameter(g1) = 3
    c: Diameter(g2) = 3
    c: Coincident(g3,g4)
    c: Coincident(g4,g5)
    c: Coincident(g5,g6)
    c: Coincident(g6,g3)
    c: Horizontal(g5)
    c: Vertical(g4)
    c: Vertical(g6)
    c: Coincident(g3,g-8)
    c: PointOnObject(g4,g-1)
    c: Coincident(g3,g-9)
FEATURE [PartDesign::Pad] Pad
  Direction = (0,0,1)
  Length = 8
  Length2 = 10
  Profile = -> Sketch
  ReferenceAxis = -> Sketch [N_Axis]
  Type = 0
FEATURE [Sketcher::SketchObject] Sketch001
  ExternalGeometry = -> [Pad,Binder]
  FullyConstrained = true
  MapMode = 5
  Placement = pos=(0,0,0) rot=(1,0,0;1.5708rad)
  Support = -> [Pad]
  sketch-geometry (4):
    g0: LineSegment StartX=5 StartY=16 StartZ=0 EndX=8 EndY=16 EndZ=0
    g1: LineSegment StartX=8 StartY=16 StartZ=0 EndX=8 EndY=0 EndZ=0
    g2: LineSegment StartX=8 StartY=0 StartZ=0 EndX=5 EndY=0 EndZ=0
    g3: LineSegment StartX=5 StartY=0 StartZ=0 EndX=5 EndY=16 EndZ=0
  constraints (11):
    c: Coincident(g0,g1)
    c: Coincident(g1,g2)
    c: Coincident(g2,g3)
    c: Coincident(g3,g0)
    c: Horizontal(g0)
    c: Horizontal(g2)
    c: Vertical(g1)
    c: Vertical(g3)
    c: Coincident(g0,g-4)
    c: PointOnObject(g2,g-5)
    c: DistanceX(g2,g1) = 3
FEATURE [PartDesign::Pad] Pad001
  BaseFeature = -> Pad
  Direction = (0,-1,2e-16)
  Length = 3
  Length2 = 10
  Profile = -> Sketch001
  ReferenceAxis = -> Sketch001 [N_Axis]
  Type = 0
FEATURE [Sketcher::SketchObject] Sketch002
  ExternalGeometry = -> [Binder,Pad001]
  FullyConstrained = true
  MapMode = 5
  Placement = pos=(0,0,0) rot=(1,0,0;3.14159rad)
  Support = -> [Pad001]
  sketch-geometry (12):
    g0: LineSegment StartX=5 StartY=0 StartZ=0 EndX=11 EndY=0 EndZ=0
    g1: LineSegment StartX=11 StartY=0 StartZ=0 EndX=11 EndY=7.65 EndZ=0
    g2: LineSegment StartX=11 StartY=7.65 StartZ=0 EndX=5 EndY=7.65 EndZ=0
    g3: LineSegment StartX=5 StartY=7.65 StartZ=0 EndX=5 EndY=0 EndZ=0
    g4: GeomPoint X=5 Y=14.8 Z=0
    g5: GeomPoint X=5 Y=-5.5 Z=0
    g6: GeomPoint X=5 Y=4.65 Z=0
    g7: Circle CenterX=8 CenterY=4.65 CenterZ=0 NormalX=0 NormalY=0 NormalZ=1 AngleXU=0 Radius=2
    g8: GeomPoint X=10 Y=4.65 Z=0
    g9: GeomPoint X=6 Y=4.65 Z=0
    g10: GeomPoint X=8 Y=6.65 Z=0
    g11: Circle CenterX=8 CenterY=4.65 CenterZ=0 NormalX=0 NormalY=0 NormalZ=1 AngleXU=0 Radius=1.5
  constraints (28):
    c: Coincident(g0,g1)
    c: Coincident(g1,g2)
    c: Coincident(g2,g3)
    c: Coincident(g3,g0)
    c: Horizontal(g0)
    c: Horizontal(g2)
    c: Vertical(g1)
    c: Vertical(g3)
    c: Coincident(g0,g-4)
    c: PointOnObject(g5,g-3)
    c: Vertical(g5,g4)
    c: Vertical(g4,g2)
    c: Symmetric(g4,g5,g6)
    c: DistanceY(g5,g4) = 20.3
    c: Horizontal(g7,g6)
    c: PointOnObject(g8,g7)
    c: PointOnObject(g9,g7)
    c: PointOnObject(g10,g7)
    c: Vertical(g10,g7)
    c: Horizontal(g9,g8)
    c: Horizontal(g7,g9)
    c: DistanceX(g8,g1) = 1
    c: DistanceY(g10,g1) = 1
    c: DistanceX(g6,g9) = 1
    c: Diameter(g7) = 4
    c: Coincident(g11,g7)
    c: Diameter(g11) = 3
    c: DistanceY(g0,g6) = 4.65  'SlideToMagnetCenter'
FEATURE [PartDesign::Pad] Pad002
  BaseFeature = -> Pad001
  Direction = (0,-2e-16,-1)
  Length = 2
  Length2 = 10
  Profile = -> Sketch002
  ReferenceAxis = -> Sketch002 [N_Axis]
  Reversed = true
  Type = 0
FEATURE [Sketcher::SketchObject] Sketch003
  ExternalGeometry = -> [Pad002]
  FullyConstrained = true
  MapMode = 5
  Placement = pos=(0,3.6e-15,16) rot=(0,0,1;0rad)
  Support = -> [Pad002]
  sketch-geometry (1):
    g0: Circle CenterX=8 CenterY=-4.65 CenterZ=0 NormalX=0 NormalY=0 NormalZ=1 AngleXU=0 Radius=2
  constraints (2):
    c: Coincident(g0,g-3)
    c: Diameter(g0) = 4  'MagnetDiameter'
FEATURE [PartDesign::Pocket] Pocket
  BaseFeature = -> Pad002
  Direction = (0,-2e-16,-1)
  Length = 15
  Length2 = 5
  Profile = -> Sketch003
  ReferenceAxis = -> Sketch003 [N_Axis]
  Type = 0
FEATURE [Sketcher::SketchObject] Sketch004
  ExternalGeometry = -> [Pocket]
  FullyConstrained = true
  MapMode = 5
  Placement = pos=(0,20,0) rot=(0,0.707107,0.707107;3.14159rad)
  Support = -> [Pocket]
  expr: Constraints[10] = <<Datasheet>>#<<mgn9c>>.Dim_P + 2 * <<Datasheet>>#<<mgn9c>>.Dim_E
  expr: Constraints[11] = <<BaseMagnetoPot>>#<<Sketch>>.Constraints.Base_End
  expr: Constraints[23] = <<Datasheet>>#<<mgn9c>>.Dim_Wr
  sketch-geometry (15):
    g0: LineSegment StartX=-5 StartY=16 StartZ=0 EndX=-16 EndY=16 EndZ=0
    g1: LineSegment StartX=-16 StartY=16 StartZ=0 EndX=-16 EndY=43 EndZ=0
    g2: LineSegment StartX=-16 StartY=43 StartZ=0 EndX=-5 EndY=43 EndZ=0
    g3: LineSegment StartX=-5 StartY=43 StartZ=0 EndX=-5 EndY=16 EndZ=0
    g4: LineSegment StartX=-35.3 StartY=36.02 StartZ=0 EndX=-16 EndY=36.02 EndZ=0
    g5: LineSegment StartX=-35.3 StartY=36.02 StartZ=0 EndX=-16 EndY=36.02 EndZ=0
    g6: LineSegment StartX=-16 StartY=36.02 StartZ=0 EndX=-16 EndY=43 EndZ=0
    g7: LineSegment StartX=-16 StartY=43 StartZ=0 EndX=-37.3 EndY=43 EndZ=0
    g8: GeomPoint X=-15 Y=16 Z=0
    g9: GeomPoint X=-6 Y=16 Z=0
    g10: GeomPoint X=-10.5 Y=16 Z=0
    g11: LineSegment StartX=-37.3 StartY=34.02 StartZ=0 EndX=-16 EndY=34.02 EndZ=0
    g12: LineSegment StartX=-16 StartY=34.02 StartZ=0 EndX=-16 EndY=16 EndZ=0
    g13: LineSegment StartX=-16 StartY=34.02 StartZ=0 EndX=-16 EndY=16 EndZ=0
    g14: LineSegment StartX=-37.3 StartY=43 StartZ=0 EndX=-37.3 EndY=34.02 EndZ=0
  constraints (37):
    c: Coincident(g0,g1)
    c: Coincident(g1,g2)
    c: Coincident(g2,g3)
    c: Coincident(g3,g0)
    c: Horizontal(g0)
    c: Horizontal(g2)
    c: Vertical(g1)
    c: Vertical(g3)
    c: Coincident(g0,g-4)
    c: Horizontal(g4)
    c: DistanceY(g-3,g2) = 35
    c: DistanceY(g-3,g4) = 28.02
    c: PointOnObject(g4,g1)
    c: Coincident(g5,g6)
    c: Coincident(g6,g7)
    c: Horizontal(g5)
    c: Horizontal(g7)
    c: Vertical(g6)
    c: Coincident(g5,g4)
    c: Coincident(g6,g2)
    c: PointOnObject(g8,g0)
    c: Symmetric(g0,g0,g10)
    c: Symmetric(g8,g9,g10)
    c: DistanceX(g8,g9) = 9
    c: DistanceX(g0,g8) = 1  'Strength'
    c: DistanceX(g5,g8) = 20.3
    c: Horizontal(g11)
    c: Coincident(g12,g11)
    c: Coincident(g12,g0)
    c: Coincident(g13,g11)
    c: PointOnObject(g11,g1)
    c: DistanceY(g11,g4) = 2
    c: Coincident(g14,g11)
    c: Vertical(g14)
    c: DistanceX(g11,g5) = 2
    c: Coincident(g7,g14)
    c: Coincident(g0,g13)
FEATURE [PartDesign::Pad] Pad003
  BaseFeature = -> Pocket
  Direction = (0,1,-2e-16)
  Length = 10
  Length2 = 10
  Profile = -> Sketch004
  ReferenceAxis = -> Sketch004 [N_Axis]
  Reversed = true
  Type = 0
  expr: Length = <<Datasheet>>#<<mgn9c>>.Dim_W / 2
FEATURE [Sketcher::SketchObject] Sketch005
  ExternalGeometry = -> [Pad003]
  FullyConstrained = true
  MapMode = 5
  Placement = pos=(4e-16,20,-5.3e-15) rot=(0,0.707107,0.707107;3.14159rad)
  Support = -> [Pad003]
  expr: Constraints[1] = <<Datasheet>>#<<mgn9c>>.Dim_P
  expr: Constraints[2] = <<Datasheet>>#<<mgn9c>>.Dim_E
  expr: Constraints[5] = 3
  sketch-geometry (3):
    g0: Circle CenterX=-10.5 CenterY=15.5 CenterZ=0 NormalX=0 NormalY=0 NormalZ=1 AngleXU=0 Radius=1.5
    g1: Circle CenterX=-10.5 CenterY=35.5 CenterZ=0 NormalX=0 NormalY=0 NormalZ=1 AngleXU=0 Radius=1.5
    g2: GeomPoint X=-10.5 Y=16 Z=0
  constraints (7):
    c: Vertical(g1,g0)
    c: DistanceY(g0,g1) = 20
    c: DistanceY(g-7,g0) = 7.5
    c: Symmetric(g-7,g-6,g2)
    c: Vertical(g2,g0)
    c: Diameter(g1) = 3
    c: Diameter(g0) = 3
FEATURE [PartDesign::Pocket] Pocket001
  BaseFeature = -> Pad003
  Direction = (0,-1,2e-16)
  Length = 10
  Length2 = 5
  Profile = -> Sketch005
  ReferenceAxis = -> Sketch005 [N_Axis]
  Type = 0
FEATURE [Sketcher::SketchObject] Sketch006
  ExternalGeometry = -> [Pocket001,Binder]
  FullyConstrained = true
  MapMode = 5
  Placement = pos=(4e-16,20,-5.3e-15) rot=(0,0.707107,0.707107;3.14159rad)
  Support = -> [Pocket001]
  expr: Constraints[11] = <<Datasheet>>#<<mgn9c>>.Dim_Wr
  sketch-geometry (5):
    g0: LineSegment StartX=-15 StartY=43 StartZ=0 EndX=-6 EndY=43 EndZ=0
    g1: LineSegment StartX=-6 StartY=43 StartZ=0 EndX=-6 EndY=8 EndZ=0
    g2: LineSegment StartX=-6 StartY=8 StartZ=0 EndX=-15 EndY=8 EndZ=0
    g3: LineSegment StartX=-15 StartY=8 StartZ=0 EndX=-15 EndY=43 EndZ=0
    g4: GeomPoint X=-10.5 Y=43 Z=0
  constraints (12):
    c: Coincident(g0,g1)
    c: Coincident(g1,g2)
    c: Coincident(g2,g3)
    c: Coincident(g3,g0)
    c: Horizontal(g0)
    c: Horizontal(g2)
    c: Vertical(g1)
    c: Vertical(g3)
    c: PointOnObject(g1,g-8)
    c: Symmetric(g-7,g-7,g4)
    c: Symmetric(g0,g0,g4)
    c: DistanceX(g0,g0) = 9
FEATURE [PartDesign::Pocket] Pocket002
  BaseFeature = -> Pocket001
  Direction = (0,-1,2e-16)
  Length = 1
  Length2 = 5
  Profile = -> Sketch006
  ReferenceAxis = -> Sketch006 [N_Axis]
  Type = 0
  expr: Length = <<Datasheet>>#<<mgn9c>>.Dim_H1 / 2
FEATURE [Sketcher::SketchObject] Sketch007
  ExternalGeometry = -> [Pocket002]
  FullyConstrained = true
  MapMode = 5
  Placement = pos=(4e-16,20,-5.3e-15) rot=(0,0.707107,0.707107;3.14159rad)
  Support = -> [Pocket002]
  sketch-geometry (10):
    g0: LineSegment StartX=-15 StartY=43 StartZ=0 EndX=-35.3 EndY=43 EndZ=0
    g1: LineSegment StartX=-35.3 StartY=43 StartZ=0 EndX=-35.3 EndY=36.02 EndZ=0
    g2: LineSegment StartX=-35.3 StartY=36.02 StartZ=0 EndX=-15 EndY=36.02 EndZ=0
    g3: LineSegment StartX=-15 StartY=36.02 StartZ=0 EndX=-15 EndY=43 EndZ=0
    g4: LineSegment StartX=-20.07 StartY=36.02 StartZ=0 EndX=-20.07 EndY=34.02 EndZ=0
    g5: LineSegment StartX=-20.07 StartY=34.02 StartZ=0 EndX=-30.23 EndY=34.02 EndZ=0
    g6: LineSegment StartX=-30.23 StartY=34.02 StartZ=0 EndX=-30.23 EndY=36.02 EndZ=0
    g7: GeomPoint X=-25.15 Y=36.02 Z=0
    g8: LineSegment StartX=-35.3 StartY=36.02 StartZ=0 EndX=-30.23 EndY=36.02 EndZ=0
    g9: LineSegment StartX=-20.07 StartY=36.02 StartZ=0 EndX=-15 EndY=36.02 EndZ=0
  constraints (25):
    c: Coincident(g0,g1)
    c: Coincident(g1,g2)
    c: Coincident(g2,g3)
    c: Coincident(g3,g0)
    c: Horizontal(g0)
    c: Horizontal(g2)
    c: Vertical(g1)
    c: Vertical(g3)
    c: Coincident(g0,g-4)
    c: DistanceY(g-6,g1) = 2
    c: DistanceX(g-6,g1) = 2
    c: Coincident(g4,g5)
    c: Coincident(g5,g6)
    c: Horizontal(g5)
    c: Vertical(g4)
    c: Vertical(g6)
    c: PointOnObject(g6,g2)
    c: PointOnObject(g4,g-5)
    c: Symmetric(g1,g3,g7)
    c: Symmetric(g6,g4,g7)
    c: DistanceX(g6,g4) = 10.16
    c: Coincident(g8,g1)
    c: Coincident(g8,g6)
    c: Coincident(g9,g4)
    c: Coincident(g9,g3)
FEATURE [PartDesign::Pocket] Pocket003
  BaseFeature = -> Pocket002
  Direction = (0,-1,2e-16)
  Length = 3
  Length2 = 5
  Profile = -> Sketch007
  ReferenceAxis = -> Sketch007 [N_Axis]
  Type = 0
FEATURE [Sketcher::SketchObject] Sketch008
  ExternalGeometry = -> [Pocket003]
  FullyConstrained = true
  MapMode = 5
  Placement = pos=(4e-16,20,-5.3e-15) rot=(0,0.707107,0.707107;3.14159rad)
  Support = -> [Pocket003]
  expr: Constraints[10] = <<BaseMagnetoPot>>#<<Sketch>>.Constraints.EndStopDistance
  sketch-geometry (4):
    g0: LineSegment StartX=-5 StartY=16 StartZ=0 EndX=-6 EndY=16 EndZ=0
    g1: LineSegment StartX=-6 StartY=16 StartZ=0 EndX=-6 EndY=22.05 EndZ=0
    g2: LineSegment StartX=-6 StartY=22.05 StartZ=0 EndX=-5 EndY=22.05 EndZ=0
    g3: LineSegment StartX=-5 StartY=22.05 StartZ=0 EndX=-5 EndY=16 EndZ=0
  constraints (12):
    c: Coincident(g0,g1)
    c: Coincident(g1,g2)
    c: Coincident(g2,g3)
    c: Coincident(g3,g0)
    c: Horizontal(g0)
    c: Horizontal(g2)
    c: Vertical(g1)
    c: Vertical(g3)
    c: Coincident(g0,g-5)
    c: PointOnObject(g1,g-4)
    c: DistanceY(g-3,g2) = 14.05
    c: DistanceY(g3,g3) = 6.05  'StopperLength'
FEATURE [PartDesign::Pad] Pad004
  BaseFeature = -> Pocket003
  Direction = (0,1,-2e-16)
  Length = 2.5
  Length2 = 10
  Profile = -> Sketch008
  ReferenceAxis = -> Sketch008 [N_Axis]
  Type = 0
FEATURE [Sketcher::SketchObject] Sketch009
  ExternalGeometry = -> [Pad004]
  FullyConstrained = true
  MapMode = 5
  Placement = pos=(5,-1e-16,0) rot=(-0.57735,0.57735,0.57735;4.18879rad)
  Support = -> [Pad004]
  sketch-geometry (3):
    g0: LineSegment StartX=-22.5 StartY=20.05 StartZ=0 EndX=-20 EndY=16 EndZ=0
    g1: LineSegment StartX=-20 StartY=16 StartZ=0 EndX=-22.5 EndY=16 EndZ=0
    g2: LineSegment StartX=-22.5 StartY=16 StartZ=0 EndX=-22.5 EndY=20.05 EndZ=0
  constraints (7):
    c: PointOnObject(g0,g-5)
    c: Coincident(g0,g-4)
    c: Coincident(g1,g0)
    c: Coincident(g1,g-5)
    c: Coincident(g2,g1)
    c: Coincident(g2,g0)
    c: DistanceY(g0,g-5) = 2  'StopperTopLength'
FEATURE [PartDesign::Pocket] Pocket004
  BaseFeature = -> Pad004
  Direction = (1,0,0)
  Length = 5
  Length2 = 5
  Profile = -> Sketch009
  ReferenceAxis = -> Sketch009 [N_Axis]
  Type = 1
FEATURE [Sketcher::SketchObject] Sketch010
  ExternalGeometry = -> [Pocket004]
  FullyConstrained = true
  MapMode = 5
  Placement = pos=(5,0,0) rot=(0.57735,-0.57735,-0.57735;2.0944rad)
  Support = -> [Pocket004]
  sketch-geometry (3):
    g0: LineSegment StartX=-10 StartY=16 StartZ=0 EndX=-16 EndY=43 EndZ=0
    g1: LineSegment StartX=-16 StartY=43 StartZ=0 EndX=-10 EndY=43 EndZ=0
    g2: LineSegment StartX=-10 StartY=43 StartZ=0 EndX=-10 EndY=16 EndZ=0
  constraints (7):
    c: Coincident(g0,g-3)
    c: PointOnObject(g0,g-4)
    c: Coincident(g1,g-4)
    c: Coincident(g2,g0)
    c: Coincident(g0,g1)
    c: DistanceX(g-4,g0) = 4
    c: Coincident(g1,g2)
FEATURE [PartDesign::Pocket] Pocket005
  BaseFeature = -> Pocket004
  Direction = (1,0,0)
  Length = 5
  Length2 = 5
  Profile = -> Sketch010
  ReferenceAxis = -> Sketch010 [N_Axis]
  Type = 1
FEATURE [PartDesign::SubShapeBinder] Binder001  label="Slide001"
  BindCopyOnChange = 0
  BindMode = 0
  ClaimChildren = false
  Context = -> Body001 [Binder001.]
  Fuse = false
  MakeFace = true
  OffsetFill = false
  OffsetIntersection = false
  OffsetJoinType = 0
  OffsetOpenResult = false
  PartialLoad = false
  Relative = true
  Support = -> [<external MG/mgn9c_slide.FCStd>#Body001]
  _Version = 2
FEATURE [Sketcher::SketchObject] Sketch011
  ExternalGeometry = -> [Binder001]
  FullyConstrained = true
  MapMode = 5
  Placement = pos=(0,0,8) rot=(0,0,1;0rad)
  Support = -> [Binder001]
  expr: Constraints[13] = .Constraints.Rad
  expr: Constraints[14] = .Constraints.Rad
  expr: Constraints[15] = .Constraints.Rad
  sketch-geometry (7):
    g0: LineSegment StartX=5 StartY=0 StartZ=0 EndX=23.9 EndY=0 EndZ=0
    g1: LineSegment StartX=23.9 StartY=0 StartZ=0 EndX=23.9 EndY=20 EndZ=0
    g2: LineSegment StartX=23.9 StartY=20 StartZ=0 EndX=5 EndY=20 EndZ=0
    g3: LineSegment StartX=5 StartY=20 StartZ=0 EndX=5 EndY=0 EndZ=0
    g4: Circle CenterX=19.45 CenterY=17.5 CenterZ=0 NormalX=0 NormalY=0 NormalZ=1 AngleXU=0 Radius=1.5
    g5: Circle CenterX=19.45 CenterY=2.5 CenterZ=0 NormalX=0 NormalY=0 NormalZ=1 AngleXU=0 Radius=1.5
    g6: Circle CenterX=9.45 CenterY=2.5 CenterZ=0 NormalX=0 NormalY=0 NormalZ=1 AngleXU=0 Radius=1.5
  constraints (17):
    c: Coincident(g0,g1)
    c: Coincident(g1,g2)
    c: Coincident(g2,g3)
    c: Coincident(g3,g0)
    c: Horizontal(g0)
    c: Horizontal(g2)
    c: Vertical(g1)
    c: Vertical(g3)
    c: Coincident(g0,g-7)
    c: Coincident(g1,g-6)
    c: Coincident(g4,g-3)
    c: Coincident(g5,g-4)
    c: Diameter(g-5) = 3  'Rad'
    c: Diameter(g6) = 3
    c: Diameter(g5) = 3
    c: Diameter(g4) = 3
    c: Coincident(g6,g-5)
FEATURE [PartDesign::Pad] Pad005
  Direction = (0,0,1)
  Length = 8
  Length2 = 10
  Profile = -> Sketch011
  ReferenceAxis = -> Sketch011 [N_Axis]
  Reversed = true
  Type = 0
FEATURE [Sketcher::SketchObject] Sketch012
  ExternalGeometry = -> [Pad005]
  FullyConstrained = true
  MapMode = 5
  Placement = pos=(0,20,0) rot=(0,0.707107,0.707107;3.14159rad)
  Support = -> [Pad005]
  expr: Constraints[10] = <<Datasheet>>#<<mgn9c>>.Dim_Wr
  expr: Constraints[11] = <<Sketch004>>.Constraints.Strength
  expr: Constraints[21] = <<BaseMagnetoPot>>#<<Sketch>>.Constraints.PartWidth
  expr: Constraints[22] = <<BaseMagnetoPot>>#<<Sketch>>.Constraints.Rail_To_Part
  expr: Constraints[23] = <<BaseMagnetoPot>>#<<Sketch>>.Constraints.PartStartToActiveStart
  expr: Constraints[30] = <<Datasheet>>#<<mgn9c>>.Dim_P
  expr: Constraints[31] = <<Datasheet>>#<<mgn9c>>.Dim_E
  expr: Constraints[32] = <<Datasheet>>#<<mgn9c>>.Dim_d
  expr: Constraints[33] = <<Datasheet>>#<<mgn9c>>.Dim_E
  expr: Constraints[39] = <<Sketch004>>.Constraints.Strength
  expr: Constraints[44] = <<BaseMagnetoPot>>#<<Sketch001>>.Constraints.Strength
  expr: Constraints[45] = <<BaseMagnetoPot>>#<<Sketch001>>.Constraints.Strength
  expr: Constraints[54] = <<BaseMagnetoPot>>#<<Sketch>>.Constraints.Base_End
  expr: Constraints[9] = <<mgn9c_13>>#<<Sketch>>.Constraints.Rail_Length
  sketch-geometry (21):
    g0: LineSegment StartX=-15 StartY=8 StartZ=0 EndX=-6 EndY=8 EndZ=0
    g1: LineSegment StartX=-6 StartY=8 StartZ=0 EndX=-6 EndY=-247 EndZ=0
    g2: LineSegment StartX=-6 StartY=-247 StartZ=0 EndX=-15 EndY=-247 EndZ=0
    g3: LineSegment StartX=-15 StartY=-247 StartZ=0 EndX=-15 EndY=8 EndZ=0
    g4: LineSegment StartX=-35.3 StartY=-3.12 StartZ=0 EndX=-15 EndY=-3.12 EndZ=0
    g5: LineSegment StartX=-15 StartY=-3.12 StartZ=0 EndX=-15 EndY=-11.05 EndZ=0
    g6: LineSegment StartX=-15 StartY=-11.05 StartZ=0 EndX=-35.3 EndY=-11.05 EndZ=0
    g7: LineSegment StartX=-35.3 StartY=-11.05 StartZ=0 EndX=-35.3 EndY=-3.12 EndZ=0
    g8: LineSegment StartX=-23.9 StartY=0 StartZ=0 EndX=-5 EndY=0 EndZ=0
    g9: LineSegment StartX=-5 StartY=0 StartZ=0 EndX=-5 EndY=-27 EndZ=0
    g10: LineSegment StartX=-5 StartY=-27 StartZ=0 EndX=-16 EndY=-27 EndZ=0
    g11: Circle CenterX=-10.5 CenterY=-19.5 CenterZ=0 NormalX=0 NormalY=0 NormalZ=1 AngleXU=0 Radius=1.75
    g12: LineSegment StartX=-10.5 StartY=-19.5 StartZ=0 EndX=-10.5 EndY=0.5 EndZ=0
    g13: LineSegment StartX=-35.3 StartY=-11.05 StartZ=0 EndX=-16 EndY=-11.05 EndZ=0
    g14: LineSegment StartX=-16 StartY=-11.05 StartZ=0 EndX=-16 EndY=-27 EndZ=0
    g15: LineSegment StartX=-23.9 StartY=0 StartZ=0 EndX=-37.3 EndY=-1.12 EndZ=0
    g16: LineSegment StartX=-37.3 StartY=-1.12 StartZ=0 EndX=-37.3 EndY=-11.05 EndZ=0
    g17: GeomPoint X=-25.15 Y=-11.05 Z=0
    g18: LineSegment StartX=-37.3 StartY=-11.05 StartZ=0 EndX=-35.3 EndY=-11.05 EndZ=0
    g19: LineSegment StartX=-35.3 StartY=-11.05 StartZ=0 EndX=-16 EndY=-11.05 EndZ=0
    g20: GeomPoint X=-15 Y=-218.98 Z=0
  constraints (56):
    c: Coincident(g0,g1)
    c: Coincident(g1,g2)
    c: Coincident(g2,g3)
    c: Coincident(g3,g0)
    c: Horizontal(g0)
    c: Horizontal(g2)
    c: Vertical(g1)
    c: Vertical(g3)
    c: Horizontal(g0,g-3)
    c: DistanceY(g1,g1) = 255
    c: DistanceX(g0,g0) = 9
    c: DistanceX(g0,g-3) = 1
    c: Coincident(g4,g5)
    c: Coincident(g5,g6)
    c: Coincident(g6,g7)
    c: Coincident(g7,g4)
    c: Horizontal(g4)
    c: Horizontal(g6)
    c: Vertical(g5)
    c: Vertical(g7)
    c: PointOnObject(g5,g3)
    c: DistanceX(g4,g4) = 20.3
    c: DistanceY(g4,g0) = 11.12
    c: DistanceY(g7,g7) = 7.93
    c: Coincident(g8,g-4)
    c: Coincident(g9,g8)
    c: Vertical(g9)
    c: Coincident(g10,g9)
    c: Horizontal(g10)
    c: Coincident(g11,g12)
    c: DistanceY(g12,g12) = 20
    c: DistanceY(g9,g11) = 7.5
    c: Diameter(g11) = 3.5
    c: DistanceY(g12,g-3) = 7.5
    c: Coincident(g13,g7)
    c: PointOnObject(g13,g6)
    c: Coincident(g14,g13)
    c: Vertical(g14)
    c: Coincident(g10,g14)
    c: DistanceX(g13,g5) = 1
    c: Symmetric(g0,g0,g12)
    c: Coincident(g8,g15)
    c: Coincident(g15,g16)
    c: Vertical(g16)
    c: DistanceX(g16,g7) = 2
    c: DistanceY(g7,g15) = 2
    c: Coincident(g8,g-4)
    c: Symmetric(g7,g5,g17)
    c: Horizontal(g16,g6)
    c: Coincident(g18,g16)
    c: Coincident(g18,g6)
    c: Coincident(g19,g18)
    c: Coincident(g19,g14)
    c: PointOnObject(g20,g3)
    c: DistanceY(g2,g20) = 28.02
    c: DistanceY(g20,g4) = 215.86
FEATURE [PartDesign::Pad] Pad006
  BaseFeature = -> Pad005
  Direction = (0,1,-2e-16)
  Length = 10
  Length2 = 10
  Profile = -> Sketch012
  ReferenceAxis = -> Sketch012 [N_Axis]
  Reversed = true
  Type = 0
  expr: Length = <<Datasheet>>#<<mgn9c>>.Dim_W / 2
FEATURE [Sketcher::SketchObject] Sketch015  label="Measurements"
  ExternalGeometry = -> [Pocket005]
  FullyConstrained = true
  MapMode = 5
  Support = -> [XY_Plane]
  constraints (3):
    c: DistanceY(g-6,g-4) = 2.5  'SlideStopHeight'
    c: DistanceY(g-3,g-6) = 1  'RailGuideHeight'
    c: DistanceY(g-5,g-3) = 2  'MagnetoPotHeightIndent'
FEATURE [Sketcher::SketchObject] Sketch017
  ExternalGeometry = -> [Pad006]
  FullyConstrained = true
  MapMode = 5
  Placement = pos=(2e-16,20,-5.2e-15) rot=(0,0.707107,0.707107;3.14159rad)
  Support = -> [Pad006]
  expr: Constraints[1] = <<Datasheet>>#<<mgn9c>>.Dim_d
  expr: Constraints[2] = <<Datasheet>>#<<mgn9c>>.Dim_P
  sketch-geometry (1):
    g0: Circle CenterX=-10.5 CenterY=0.5 CenterZ=0 NormalX=0 NormalY=0 NormalZ=1 AngleXU=0 Radius=1.75
  constraints (3):
    c: Vertical(g-3,g0)
    c: Diameter(g0) = 3.5
    c: DistanceY(g-3,g0) = 20
FEATURE [PartDesign::Pocket] Pocket009
  BaseFeature = -> Pad006
  Direction = (0,-1,2e-16)
  Length = 10
  Length2 = 5
  Profile = -> Sketch017
  ReferenceAxis = -> Sketch017 [N_Axis]
  Type = 0
  expr: Length = <<Datasheet>>#<<mgn9c>>.Dim_W / 2
FEATURE [Sketcher::SketchObject] Sketch014
  ExternalGeometry = -> [Pocket009]
  FullyConstrained = true
  MapMode = 5
  Placement = pos=(2e-16,20,-5.2e-15) rot=(0,0.707107,0.707107;3.14159rad)
  Support = -> [Pocket009]
  expr: Constraints[28] = <<Datasheet>>#<<mgn9c>>.Dim_Wr
  expr: Constraints[8] = <<BaseMagnetoPot>>#<<Sketch>>.Constraints.PartWidth
  expr: Constraints[9] = <<BaseMagnetoPot>>#<<Sketch>>.Constraints.PartStartToActiveStart
  sketch-geometry (13):
    g0: LineSegment StartX=-35.3 StartY=-11.05 StartZ=0 EndX=-15 EndY=-11.05 EndZ=0
    g1: LineSegment StartX=-15 StartY=-11.05 StartZ=0 EndX=-15 EndY=-3.12 EndZ=0
    g2: LineSegment StartX=-15 StartY=-3.12 StartZ=0 EndX=-35.3 EndY=-3.12 EndZ=0
    g3: LineSegment StartX=-35.3 StartY=-3.12 StartZ=0 EndX=-35.3 EndY=-11.05 EndZ=0
    g4: LineSegment StartX=-15 StartY=-3.12 StartZ=0 EndX=-6 EndY=-3.12 EndZ=0
    g5: LineSegment StartX=-6 StartY=-3.12 StartZ=0 EndX=-6 EndY=-27 EndZ=0
    g6: LineSegment StartX=-6 StartY=-27 StartZ=0 EndX=-16 EndY=-27 EndZ=0
    g7: LineSegment StartX=-16 StartY=-11.05 StartZ=0 EndX=-16 EndY=-27 EndZ=0
    g8: LineSegment StartX=-35.3 StartY=-11.05 StartZ=0 EndX=-16 EndY=-11.05 EndZ=0
    g9: LineSegment StartX=-6 StartY=-3.12 StartZ=0 EndX=-6 EndY=8 EndZ=0
    g10: LineSegment StartX=-6 StartY=8 StartZ=0 EndX=-15 EndY=8 EndZ=0
    g11: LineSegment StartX=-15 StartY=8 StartZ=0 EndX=-15 EndY=-3.12 EndZ=0
    g12: LineSegment StartX=-10.5 StartY=0.5 StartZ=0 EndX=-10.5 EndY=-3.12 EndZ=0
  constraints (35):
    c: Coincident(g0,g1)
    c: Coincident(g1,g2)
    c: Coincident(g2,g3)
    c: Coincident(g3,g0)
    c: Horizontal(g0)
    c: Horizontal(g2)
    c: Vertical(g1)
    c: Vertical(g3)
    c: DistanceX(g2,g2) = 20.3
    c: DistanceY(g1,g1) = 7.93
    c: Coincident(g4,g2)
    c: Horizontal(g4)
    c: Coincident(g5,g4)
    c: Vertical(g5)
    c: Coincident(g6,g5)
    c: Horizontal(g6)
    c: Coincident(g7,g6)
    c: Coincident(g8,g3)
    c: Coincident(g8,g7)
    c: Coincident(g9,g10)
    c: Coincident(g10,g11)
    c: Horizontal(g10)
    c: Vertical(g9)
    c: Vertical(g11)
    c: Coincident(g4,g9)
    c: Coincident(g1,g11)
    c: PointOnObject(g10,g-4)
    c: PointOnObject(g7,g0)
    c: DistanceX(g10,g10) = 9
    c: Coincident(g12,g-6)
    c: PointOnObject(g12,g4)
    c: Symmetric(g10,g9,g12)
    c: Coincident(g6,g-7)
    c: Coincident(g-5,g7)
    c: DistanceX(g9,g-4) = 1  'SlideGuideWidth'
FEATURE [PartDesign::Pocket] Pocket010
  BaseFeature = -> Pocket009
  Direction = (0,-1,2e-16)
  Length = 1
  Length2 = 5
  Profile = -> Sketch014
  ReferenceAxis = -> Sketch014 [N_Axis]
  Type = 0
  expr: Length = <<Measurements>>.Constraints.RailGuideHeight
FEATURE [Sketcher::SketchObject] Sketch016
  ExternalGeometry = -> [Pocket010]
  FullyConstrained = true
  MapMode = 5
  Placement = pos=(-2e-16,19,-4.5e-15) rot=(0,0.707107,0.707107;3.14159rad)
  Support = -> [Pocket010]
  sketch-geometry (4):
    g0: LineSegment StartX=-35.3 StartY=-27 StartZ=0 EndX=-15 EndY=-27 EndZ=0
    g1: LineSegment StartX=-15 StartY=-27 StartZ=0 EndX=-15 EndY=-3.12 EndZ=0
    g2: LineSegment StartX=-15 StartY=-3.12 StartZ=0 EndX=-35.3 EndY=-3.12 EndZ=0
    g3: LineSegment StartX=-35.3 StartY=-3.12 StartZ=0 EndX=-35.3 EndY=-27 EndZ=0
  constraints (11):
    c: Coincident(g0,g1)
    c: Coincident(g1,g2)
    c: Coincident(g2,g3)
    c: Coincident(g3,g0)
    c: Horizontal(g0)
    c: Horizontal(g2)
    c: Vertical(g1)
    c: Vertical(g3)
    c: Coincident(g1,g-5)
    c: PointOnObject(g0,g-3)
    c: PointOnObject(g-4,g3)
FEATURE [PartDesign::Pocket] Pocket011
  BaseFeature = -> Pocket010
  Direction = (0,-1,2e-16)
  Length = 2
  Length2 = 5
  Profile = -> Sketch016
  ReferenceAxis = -> Sketch016 [N_Axis]
  Type = 0
  expr: Length = <<Measurements>>.Constraints.MagnetoPotHeightIndent
FEATURE [PartDesign::Pocket] Pocket012
  BaseFeature = -> Pocket011
  Direction = (0,0,-1)
  Length = 5
  Length2 = 5
  Profile = -> Pocket011 [Edge20]
  Type = 1
FEATURE [Sketcher::SketchObject] Sketch018
  ExternalGeometry = -> [Pocket012]
  FullyConstrained = true
  MapMode = 5
  Placement = pos=(-1e-15,-2.5e-15,-11.05) rot=(1,0,0;3.14159rad)
  Support = -> [Pocket012]
  expr: Constraints[1] = <<Datasheet>>#<<mgn9c>>.Dim_D
  expr: Constraints[3] = <<Datasheet>>#<<mgn9c>>.Dim_D
  expr: Constraints[5] = <<Datasheet>>#<<mgn9c>>.Dim_D
  sketch-geometry (18):
    g0: Circle CenterX=19.45 CenterY=-17.5 CenterZ=0 NormalX=0 NormalY=0 NormalZ=1 AngleXU=0 Radius=3
    g1: Circle CenterX=9.45 CenterY=-2.5 CenterZ=0 NormalX=0 NormalY=0 NormalZ=1 AngleXU=0 Radius=3
    g2: Circle CenterX=19.45 CenterY=-2.5 CenterZ=0 NormalX=0 NormalY=0 NormalZ=1 AngleXU=0 Radius=3
    g3: ArcOfCircle CenterX=19.45 CenterY=-17.5 CenterZ=0 NormalX=0 NormalY=0 NormalZ=1 AngleXU=0 Radius=3 StartAngle=5.24197e-06 EndAngle=3.14159
    g4: LineSegment StartX=16.45 StartY=-17.5 StartZ=0 EndX=22.45 EndY=-17.5 EndZ=0
    g5: LineSegment StartX=22.45 StartY=-17.5 StartZ=0 EndX=22.45 EndY=-20 EndZ=0
    g6: LineSegment StartX=22.45 StartY=-20 StartZ=0 EndX=16.45 EndY=-20 EndZ=0
    g7: LineSegment StartX=16.45 StartY=-20 StartZ=0 EndX=16.45 EndY=-17.5 EndZ=0
    g8: ArcOfCircle CenterX=19.45 CenterY=-2.5 CenterZ=0 NormalX=0 NormalY=0 NormalZ=1 AngleXU=0 Radius=3 StartAngle=3.1416 EndAngle=6.28318
    g9: ArcOfCircle CenterX=9.45 CenterY=-2.5 CenterZ=0 NormalX=0 NormalY=0 NormalZ=1 AngleXU=0 Radius=3 StartAngle=3.14159 EndAngle=6.28319
    g10: LineSegment StartX=6.45 StartY=-2.5 StartZ=0 EndX=12.45 EndY=-2.5 EndZ=0
    g11: LineSegment StartX=12.45 StartY=-2.5 StartZ=0 EndX=12.45 EndY=0 EndZ=0
    g12: LineSegment StartX=12.45 StartY=0 StartZ=0 EndX=6.45 EndY=0 EndZ=0
    g13: LineSegment StartX=6.45 StartY=0 StartZ=0 EndX=6.45 EndY=-2.5 EndZ=0
    g14: LineSegment StartX=16.45 StartY=-2.50002 StartZ=0 EndX=22.45 EndY=-2.50002 EndZ=0
    g15: LineSegment StartX=22.45 StartY=-2.50002 StartZ=0 EndX=22.45 EndY=0 EndZ=0
    g16: LineSegment StartX=22.45 StartY=0 StartZ=0 EndX=16.45 EndY=0 EndZ=0
    g17: LineSegment StartX=16.45 StartY=0 StartZ=0 EndX=16.45 EndY=-2.50002 EndZ=0
  constraints (48):
    c: Coincident(g0,g-3)
    c: Diameter(g0) = 6
    c: Coincident(g1,g-6)
    c: Diameter(g1) = 6
    c: Coincident(g2,g-5)
    c: Diameter(g2) = 6
    c: PointOnObject(g3,g0)
    c: Coincident(g0,g3)
    c: Coincident(g4,g5)
    c: Coincident(g5,g6)
    c: Coincident(g6,g7)
    c: Coincident(g7,g4)
    c: Horizontal(g4)
    c: Horizontal(g6)
    c: Vertical(g5)
    c: Vertical(g7)
    c: Coincident(g4,g3)
    c: Coincident(g3,g4)
    c: Tangent(g3,g5)
    c: PointOnObject(g5,g-7)
    c: Coincident(g8,g2)
    c: PointOnObject(g8,g2)
    c: Coincident(g9,g1)
    c: Coincident(g10,g11)
    c: Coincident(g11,g12)
    c: Coincident(g12,g13)
    c: Coincident(g13,g10)
    c: Horizontal(g10)
    c: Horizontal(g12)
    c: Vertical(g11)
    c: Vertical(g13)
    c: PointOnObject(g11,g-8)
    c: Coincident(g14,g15)
    c: Coincident(g15,g16)
    c: Coincident(g16,g17)
    c: Coincident(g17,g14)
    c: Horizontal(g14)
    c: Horizontal(g16)
    c: Vertical(g15)
    c: Vertical(g17)
    c: Coincident(g14,g8)
    c: PointOnObject(g15,g-8)
    c: Coincident(g8,g14)
    c: Tangent(g8,g15)
    c: Tangent(g9,g11)
    c: Coincident(g10,g9)
    c: PointOnObject(g9,g1)
    c: Coincident(g9,g10)
FEATURE [Sketcher::SketchObject] Sketch019  label="Measurement"
  ExternalGeometry = -> [Pocket012]
  FullyConstrained = true
  MapMode = 5
  Placement = pos=(0,20,0) rot=(0,0.707107,0.707107;3.14159rad)
  Support = -> [Pocket012]
  constraints (1):
    c: DistanceY(g-5,g-3) = 19.05  'Height'
FEATURE [PartDesign::Pocket] Pocket013
  BaseFeature = -> Pocket012
  Direction = (1e-16,2e-16,1)
  Length = 17.05
  Length2 = 5
  Profile = -> Sketch018
  ReferenceAxis = -> Sketch018 [N_Axis]
  Type = 0
  expr: Length = <<Measurement>>.Constraints.Height - 2 mm
FEATURE [Sketcher::SketchObject] Sketch020
  ExternalGeometry = -> [Pocket005]
  FullyConstrained = true
  MapMode = 5
  Placement = pos=(0,0,16) rot=(0,0,1;0rad)
  Support = -> [Pocket005]
  expr: Constraints[37] = <<Datasheet>>#<<mgn9c>>.Dim_D / 2
  expr: Constraints[38] = <<Datasheet>>#<<mgn9c>>.Dim_D / 2
  expr: Constraints[39] = <<Datasheet>>#<<mgn9c>>.Dim_D / 2
  sketch-geometry (15):
    g0: ArcOfCircle CenterX=19.45 CenterY=17.5 CenterZ=0 NormalX=0 NormalY=0 NormalZ=1 AngleXU=0 Radius=3 StartAngle=3.14159 EndAngle=6.28318
    g1: ArcOfCircle CenterX=19.45 CenterY=2.5 CenterZ=0 NormalX=0 NormalY=0 NormalZ=1 AngleXU=0 Radius=3 StartAngle=1.6056e-08 EndAngle=3.14159
    g2: ArcOfCircle CenterX=9.45 CenterY=2.5 CenterZ=0 NormalX=0 NormalY=0 NormalZ=1 AngleXU=0 Radius=3 StartAngle=6.28319 EndAngle=9.42478
    g3: LineSegment StartX=6.45 StartY=0 StartZ=0 EndX=12.45 EndY=0 EndZ=0
    g4: LineSegment StartX=12.45 StartY=0 StartZ=0 EndX=12.45 EndY=2.5 EndZ=0
    g5: LineSegment StartX=12.45 StartY=2.5 StartZ=0 EndX=6.45 EndY=2.5 EndZ=0
    g6: LineSegment StartX=6.45 StartY=2.5 StartZ=0 EndX=6.45 EndY=0 EndZ=0
    g7: LineSegment StartX=16.45 StartY=2.5 StartZ=0 EndX=22.45 EndY=2.5 EndZ=0
    g8: LineSegment StartX=22.45 StartY=2.5 StartZ=0 EndX=22.45 EndY=0 EndZ=0
    g9: LineSegment StartX=22.45 StartY=0 StartZ=0 EndX=16.45 EndY=0 EndZ=0
    g10: LineSegment StartX=16.45 StartY=0 StartZ=0 EndX=16.45 EndY=2.5 EndZ=0
    g11: LineSegment StartX=16.45 StartY=17.5 StartZ=0 EndX=22.45 EndY=17.5 EndZ=0
    g12: LineSegment StartX=22.45 StartY=17.5 StartZ=0 EndX=22.45 EndY=20 EndZ=0
    g13: LineSegment StartX=22.45 StartY=20 StartZ=0 EndX=16.45 EndY=20 EndZ=0
    g14: LineSegment StartX=16.45 StartY=20 StartZ=0 EndX=16.45 EndY=17.5 EndZ=0
  constraints (42):
    c: Coincident(g0,g-5)
    c: Coincident(g1,g-3)
    c: Coincident(g2,g-4)
    c: Coincident(g3,g4)
    c: Coincident(g4,g5)
    c: Coincident(g5,g6)
    c: Coincident(g6,g3)
    c: Horizontal(g3)
    c: Horizontal(g5)
    c: Vertical(g4)
    c: Vertical(g6)
    c: Coincident(g4,g2)
    c: Coincident(g2,g5)
    c: Tangent(g2,g6)
    c: Coincident(g7,g8)
    c: Coincident(g8,g9)
    c: Coincident(g9,g10)
    c: Coincident(g10,g7)
    c: Horizontal(g7)
    c: Horizontal(g9)
    c: Vertical(g8)
    c: Vertical(g10)
    c: Coincident(g7,g1)
    c: Coincident(g1,g7)
    c: Tangent(g1,g8)
    c: Coincident(g11,g12)
    c: Coincident(g12,g13)
    c: Coincident(g13,g14)
    c: Coincident(g14,g11)
    c: Horizontal(g11)
    c: Horizontal(g13)
    c: Vertical(g12)
    c: Vertical(g14)
    c: Coincident(g11,g0)
    c: PointOnObject(g12,g-6)
    c: Coincident(g11,g0)
    c: Tangent(g0,g12)
    c: Radius(g0) = 3
    c: Radius(g1) = 3
    c: Radius(g2) = 3
    c: PointOnObject(g3,g-1)
    c: PointOnObject(g9,g-1)
FEATURE [PartDesign::Pocket] Pocket014
  BaseFeature = -> Pocket005
  Direction = (0,0,-1)
  Length = 6
  Length2 = 5
  Profile = -> Sketch020
  ReferenceAxis = -> Sketch020 [N_Axis]
  Type = 0
FEATURE [Sketcher::SketchObject] Sketch021
  ExternalGeometry = -> [Pocket014]
  FullyConstrained = true
  MapMode = 5
  Placement = pos=(0,0,16) rot=(0,0,1;0rad)
  Support = -> [Pocket014]
  sketch-geometry (11):
    g0: LineSegment StartX=5 StartY=0 StartZ=0 EndX=23.9 EndY=0 EndZ=0
    g1: LineSegment StartX=23.9 StartY=0 StartZ=0 EndX=23.9 EndY=10 EndZ=0
    g2: LineSegment StartX=5 StartY=10 StartZ=0 EndX=5 EndY=0 EndZ=0
    g3: LineSegment StartX=23.9 StartY=10 StartZ=0 EndX=23.9 EndY=20 EndZ=0
    g4: LineSegment StartX=23.9 StartY=20 StartZ=0 EndX=16 EndY=20 EndZ=0
    g5: LineSegment StartX=16 StartY=20 StartZ=0 EndX=16 EndY=10 EndZ=0
    g6: LineSegment StartX=5 StartY=10 StartZ=0 EndX=16 EndY=10 EndZ=0
    g7: LineSegment StartX=5 StartY=-3 StartZ=0 EndX=8 EndY=-3 EndZ=0
    g8: LineSegment StartX=8 StartY=-3 StartZ=0 EndX=8 EndY=0 EndZ=0
    g9: LineSegment StartX=5 StartY=0 StartZ=0 EndX=5 EndY=-3 EndZ=0
    g10: LineSegment StartX=8 StartY=0 StartZ=0 EndX=23.9 EndY=0 EndZ=0
  constraints (26):
    c: Coincident(g0,g1)
    c: Coincident(g2,g0)
    c: Horizontal(g0)
    c: Vertical(g1)
    c: Vertical(g2)
    c: Coincident(g0,g-5)
    c: Coincident(g1,g-4)
    c: Coincident(g3,g4)
    c: Coincident(g4,g5)
    c: Horizontal(g4)
    c: Vertical(g5)
    c: Coincident(g3,g-3)
    c: Coincident(g1,g3)
    c: Coincident(g6,g2)
    c: Coincident(g6,g5)
    c: Horizontal(g6)
    c: Coincident(g5,g-4)
    c: Coincident(g7,g8)
    c: Coincident(g9,g7)
    c: Horizontal(g7)
    c: Vertical(g8)
    c: Coincident(g7,g-6)
    c: Coincident(g8,g-7)
    c: Coincident(g9,g2)
    c: Coincident(g10,g8)
    c: Coincident(g10,g1)
FEATURE [PartDesign::Pocket] Pocket015
  BaseFeature = -> Pocket014
  Direction = (0,0,-1)
  Length = 4
  Length2 = 5
  Profile = -> Sketch021
  ReferenceAxis = -> Sketch021 [N_Axis]
  Type = 0
FEATURE [Sketcher::SketchObject] Sketch022
  ExternalGeometry = -> [Pocket013]
  FullyConstrained = true
  MapMode = 5
  Placement = pos=(0,0,0) rot=(1,0,0;3.14159rad)
  Support = -> [Pocket013]
  sketch-geometry (4):
    g0: LineSegment StartX=5 StartY=-10 StartZ=0 EndX=23.9 EndY=-10 EndZ=0
    g1: LineSegment StartX=23.9 StartY=-10 StartZ=0 EndX=23.9 EndY=0 EndZ=0
    g2: LineSegment StartX=23.9 StartY=0 StartZ=0 EndX=5 EndY=0 EndZ=0
    g3: LineSegment StartX=5 StartY=0 StartZ=0 EndX=5 EndY=-10 EndZ=0
  constraints (10):
    c: Coincident(g0,g1)
    c: Coincident(g1,g2)
    c: Coincident(g2,g3)
    c: Coincident(g3,g0)
    c: Horizontal(g0)
    c: Horizontal(g2)
    c: Vertical(g1)
    c: Vertical(g3)
    c: Coincident(g0,g-3)
    c: Coincident(g1,g-4)
FEATURE [Sketcher::SketchObject] Sketch023
  AttachmentOffset = pos=(0,0,-10) rot=(0,0,1;0rad)
  ExternalGeometry = -> [Pocket015]
  FullyConstrained = true
  MapMode = 5
  Placement = pos=(0,9,-3.6e-15) rot=(0,0.707107,0.707107;3.14159rad)
  Support = -> [Pocket015]
  expr: Constraints[2] = <<Datasheet>>#<<mgn9c>>.Dim_D
  expr: Constraints[3] = <<Datasheet>>#<<mgn9c>>.Dim_D
  sketch-geometry (2):
    g0: Circle CenterX=-10.5 CenterY=15.5 CenterZ=0 NormalX=0 NormalY=0 NormalZ=1 AngleXU=0 Radius=3
    g1: Circle CenterX=-10.5 CenterY=35.5 CenterZ=0 NormalX=0 NormalY=0 NormalZ=1 AngleXU=0 Radius=3
  constraints (4):
    c: Coincident(g0,g-6)
    c: Coincident(g1,g-4)
    c: Diameter(g1) = 6
    c: Diameter(g0) = 6
FEATURE [PartDesign::Pocket] Pocket017
  BaseFeature = -> Pocket015
  Direction = (0,-1,2e-16)
  Length = 8
  Length2 = 5
  Profile = -> Sketch023
  ReferenceAxis = -> Sketch023 [N_Axis]
  Reversed = true
  Type = 0
  expr: Length = 10 - 2
FEATURE [PartDesign::Body] Body  label="NormalConnectorMagnet"
  Group = -> [Binder,Sketch,Pad,Sketch001,Pad001,Sketch002,Pad002,Sketch003,Pocket,Sketch004,Pad003,Sketch005,Pocket001,Sketch006,Pocket002,Sketch007,Pocket003,Sketch008,Pad004,Sketch009,Pocket004,Sketch010,Pocket005,Sketch015,Sketch020,Pocket014,Sketch021,Pocket015,Sketch023,Pocket017]
  Origin = -> Origin
  Tip = -> Pocket017
FEATURE [PartDesign::Pocket] Pocket016
  BaseFeature = -> Pocket013
  Direction = (0,0,1)
  Length = 4
  Length2 = 5
  Profile = -> Sketch022
  ReferenceAxis = -> Sketch022 [N_Axis]
  Type = 0
FEATURE [Sketcher::SketchObject] Sketch024
  ExternalGeometry = -> [Pocket016]
  FullyConstrained = true
  MapMode = 5
  Placement = pos=(5,0,0) rot=(0.57735,-0.57735,-0.57735;2.0944rad)
  Support = -> [Pocket016]
  sketch-geometry (3):
    g0: LineSegment StartX=-10 StartY=4 StartZ=0 EndX=-16 EndY=-27 EndZ=0
    g1: LineSegment StartX=-10 StartY=4 StartZ=0 EndX=-10 EndY=-27 EndZ=0
    g2: LineSegment StartX=-10 StartY=-27 StartZ=0 EndX=-16 EndY=-27 EndZ=0
  constraints (8):
    c: Coincident(g0,g-6)
    c: PointOnObject(g0,g-5)
    c: DistanceX(g-4,g0) = 1
    c: Coincident(g0,g1)
    c: Vertical(g1)
    c: Coincident(g1,g2)
    c: Coincident(g2,g0)
    c: Horizontal(g2)
FEATURE [PartDesign::Pocket] Pocket018
  BaseFeature = -> Pocket016
  Direction = (1,0,0)
  Length = 5
  Length2 = 5
  Profile = -> Sketch024
  ReferenceAxis = -> Sketch024 [N_Axis]
  Type = 1
FEATURE [Sketcher::SketchObject] Sketch025
  AttachmentOffset = pos=(0,0,-10) rot=(0,0,1;0rad)
  ExternalGeometry = -> [Pocket018]
  FullyConstrained = true
  MapMode = 5
  Placement = pos=(-1e-16,9,-2.3e-15) rot=(0,0.707107,0.707107;3.14159rad)
  Support = -> [Pocket018]
  expr: Constraints[2] = <<Datasheet>>#<<mgn9c>>.Dim_D
  expr: Constraints[3] = <<Datasheet>>#<<mgn9c>>.Dim_D
  sketch-geometry (2):
    g0: Circle CenterX=-10.5 CenterY=0.5 CenterZ=0 NormalX=0 NormalY=0 NormalZ=1 AngleXU=0 Radius=3
    g1: Circle CenterX=-10.5 CenterY=-19.5 CenterZ=0 NormalX=0 NormalY=0 NormalZ=1 AngleXU=0 Radius=3
  constraints (4):
    c: Coincident(g0,g-3)
    c: Coincident(g1,g-4)
    c: Diameter(g1) = 6
    c: Diameter(g0) = 6
FEATURE [PartDesign::Pocket] Pocket019
  BaseFeature = -> Pocket018
  Direction = (0,-1,2e-16)
  Length = 8
  Length2 = 5
  Profile = -> Sketch025
  ReferenceAxis = -> Sketch025 [N_Axis]
  Reversed = true
  Type = 0
  expr: Length = 10 - 2
FEATURE [Sketcher::SketchObject] Sketch026
  ExternalGeometry = -> [Pocket019]
  FullyConstrained = true
  MapMode = 5
  Placement = pos=(5,0,0) rot=(0.57735,-0.57735,-0.57735;2.0944rad)
  Support = -> [Pocket019]
  expr: Constraints[10] = <<Sketch008>>.Constraints.StopperLength
  expr: Constraints[11] = <<Measurements>>.Constraints.SlideStopHeight
  expr: Constraints[13] = <<Sketch009>>.Constraints.StopperTopLength
  expr: Constraints[9] = <<BaseMagnetoPot>>#<<Sketch>>.Constraints.EndStopDistance
  sketch-geometry (7):
    g0: LineSegment StartX=-20 StartY=2.7e-15 StartZ=0 EndX=-22.5 EndY=2.7e-15 EndZ=0
    g1: LineSegment StartX=-22.5 StartY=2.7e-15 StartZ=0 EndX=-22.5 EndY=-6.05 EndZ=0
    g2: LineSegment StartX=-22.5 StartY=-6.05 StartZ=0 EndX=-20 EndY=-6.05 EndZ=0
    g3: LineSegment StartX=-20 StartY=-6.05 StartZ=0 EndX=-20 EndY=2.7e-15 EndZ=0
    g4: GeomPoint X=-22.5 Y=-4.05 Z=0
    g5: LineSegment StartX=-22.5 StartY=-6.05 StartZ=0 EndX=-22.5 EndY=-4.05 EndZ=0
    g6: LineSegment StartX=-20 StartY=2.7e-15 StartZ=0 EndX=-22.5 EndY=-4.05 EndZ=0
  constraints (18):
    c: Coincident(g0,g1)
    c: Coincident(g1,g2)
    c: Coincident(g2,g3)
    c: Coincident(g3,g0)
    c: Horizontal(g0)
    c: Horizontal(g2)
    c: Vertical(g1)
    c: Vertical(g3)
    c: PointOnObject(g0,g-4)
    c: DistanceY(g2,g-3) = 14.05
    c: DistanceY(g3,g3) = 6.05
    c: DistanceX(g2,g2) = 2.5
    c: PointOnObject(g4,g1)
    c: DistanceY(g1,g4) = 2
    c: Coincident(g2,g5)
    c: Coincident(g5,g4)
    c: Coincident(g3,g6)
    c: Coincident(g6,g5)
FEATURE [PartDesign::Pad] Pad007
  BaseFeature = -> Pocket019
  Direction = (-1,0,0)
  Length = 1
  Length2 = 10
  Profile = -> Sketch026
  ReferenceAxis = -> Sketch026 [N_Axis]
  Reversed = true
  Type = 0
  expr: Length = <<Sketch014>>.Constraints.SlideGuideWidth
FEATURE [PartDesign::Body] Body001  label="NormalConnector"
  Group = -> [Binder001,Sketch011,Pad005,Sketch012,Pad006,Sketch014,Sketch016,Sketch017,Pocket009,Pocket010,Pocket011,Pocket012,Sketch018,Sketch019,Pocket013,Sketch022,Pocket016,Sketch024,Pocket018,Sketch025,Pocket019,Sketch026,Pad007]
  Origin = -> Origin001
  Tip = -> Pad007
---- part parts/R202.FCStd = doc fcstd_918ec5f0634b ----
FCSTD DOCUMENT  (FreeCAD 0.21R33668 +26 (Git))
Label: R202
License: All rights reserved
LicenseURL: http://en.wikipedia.org/wiki/All_rights_reserved
objects: Sketcher::SketchObject×2, PartDesign::Pad×1, PartDesign::Revolution×1, Spreadsheet::Sheet×1
note: 6 computed .brp shape members not serialized (recipe doc carries the construction recipe); baked Part::Feature solids carry a one-line shape summary decoded from their .brp

FEATURE [Sketcher::SketchObject] Sketch003
  AttachmentOffset = pos=(0,0,0) rot=(0,0,1;1.5708rad)
  FullyConstrained = true
  MapMode = 5
  Placement = pos=(0,0,0) rot=(0,0,1;1.5708rad)
  Support = -> [XY_Plane003]
  expr: .Constraints.ScrewDistance = <<Joystick>>.SD
  expr: Constraints[10] = <<Joystick>>.BW
  expr: Constraints[25] = <<Joystick>>.BW * 0.5
  expr: Constraints[26] = <<Joystick>>.PE
  expr: Constraints[27] = <<Joystick>>.BD * 0.5
  expr: Constraints[28] = <<Joystick>>.PE
  expr: Constraints[50] = <<Joystick>>.SD
  expr: Constraints[53] = <<Joystick>>.SBD / 2
  expr: Constraints[54] = <<Joystick>>.SBD / 2
  expr: Constraints[55] = <<Joystick>>.SBD / 2
  expr: Constraints[56] = <<Joystick>>.SBD / 2
  expr: Constraints[9] = <<Joystick>>.BD
  sketch-geometry (23):
    g0: LineSegment StartX=-20.2 StartY=20.2 StartZ=0 EndX=20.2 EndY=20.2 EndZ=0
    g1: LineSegment StartX=20.2 StartY=20.2 StartZ=0 EndX=20.2 EndY=-20.2 EndZ=0
    g2: LineSegment StartX=20.2 StartY=-20.2 StartZ=0 EndX=-20.2 EndY=-20.2 EndZ=0
    g3: LineSegment StartX=-20.2 StartY=-20.2 StartZ=0 EndX=-20.2 EndY=20.2 EndZ=0
    g4: LineSegment StartX=-10.1 StartY=29.4 StartZ=0 EndX=10.1 EndY=29.4 EndZ=0
    g5: LineSegment StartX=10.1 StartY=29.4 StartZ=0 EndX=10.1 EndY=20.2 EndZ=0
    g6: LineSegment StartX=-10.1 StartY=20.2 StartZ=0 EndX=-10.1 EndY=29.4 EndZ=0
    g7: LineSegment StartX=-29.4 StartY=10.1 StartZ=0 EndX=-20.2 EndY=10.1 EndZ=0
    g8: LineSegment StartX=-20.2 StartY=-10.1 StartZ=0 EndX=-29.4 EndY=-10.1 EndZ=0
    g9: LineSegment StartX=-29.4 StartY=-10.1 StartZ=0 EndX=-29.4 EndY=10.1 EndZ=0
    g10: GeomPoint X=-20.2 Y=-2e-16 Z=0
    g11: LineSegment StartX=-20.2 StartY=20.2 StartZ=0 EndX=-20.2 EndY=10.1 EndZ=0
    g12: LineSegment StartX=-20.2 StartY=20.2 StartZ=0 EndX=-10.1 EndY=20.2 EndZ=0
    g13: LineSegment StartX=-20.2 StartY=-20.2 StartZ=0 EndX=-20.2 EndY=-10.1 EndZ=0
    g14: LineSegment StartX=10.1 StartY=20.2 StartZ=0 EndX=20.2 EndY=20.2 EndZ=0
    g15: Circle CenterX=-16.25 CenterY=16.25 CenterZ=0 NormalX=0 NormalY=0 NormalZ=1 AngleXU=0 Radius=1
    g16: Circle CenterX=16.25 CenterY=16.25 CenterZ=0 NormalX=0 NormalY=0 NormalZ=1 AngleXU=0 Radius=1
    g17: Circle CenterX=16.25 CenterY=-16.25 CenterZ=0 NormalX=0 NormalY=0 NormalZ=1 AngleXU=0 Radius=1
    g18: Circle CenterX=-16.25 CenterY=-16.25 CenterZ=0 NormalX=0 NormalY=0 NormalZ=1 AngleXU=0 Radius=1
    g19: LineSegment StartX=-16.25 StartY=16.25 StartZ=0 EndX=16.25 EndY=16.25 EndZ=0
    g20: LineSegment StartX=16.25 StartY=16.25 StartZ=0 EndX=16.25 EndY=-16.25 EndZ=0
    g21: LineSegment StartX=16.25 StartY=-16.25 StartZ=0 EndX=-16.25 EndY=-16.25 EndZ=0
    g22: LineSegment StartX=-16.25 StartY=-16.25 StartZ=0 EndX=-16.25 EndY=16.25 EndZ=0
  constraints (57):
    c: Coincident(g0,g1)
    c: Coincident(g1,g2)
    c: Coincident(g2,g3)
    c: Coincident(g3,g0)
    c: Horizontal(g0)
    c: Horizontal(g2)
    c: Vertical(g1)
    c: Vertical(g3)
    c: Symmetric(g2,g0,g-1)
    c: DistanceY(g1,g1) = 40.4
    c: DistanceX(g0,g0) = 40.4
    c: Coincident(g4,g5)
    c: Coincident(g6,g4)
    c: Horizontal(g4)
    c: Vertical(g5)
    c: Vertical(g6)
    c: PointOnObject(g5,g0)
    c: Coincident(g8,g9)
    c: Coincident(g9,g7)
    c: Horizontal(g7)
    c: Horizontal(g8)
    c: Vertical(g9)
    c: Symmetric(g0,g2,g10)
    c: Symmetric(g7,g8,g10)
    c: Symmetric(g6,g5,g-2)
    c: DistanceX(g4,g4) = 20.2
    c: DistanceY(g5,g5) = 9.2
    c: DistanceY(g9,g9) = 20.2
    c: DistanceX(g7,g7) = 9.2
    c: Coincident(g11,g0)
    c: Coincident(g11,g7)
    c: Coincident(g12,g11)
    c: Coincident(g13,g2)
    c: Coincident(g13,g8)
    c: Vertical(g13)
    c: Coincident(g12,g6)
    c: Coincident(g14,g5)
    c: Coincident(g14,g1)
    c: Coincident(g19,g20)
    c: Coincident(g20,g21)
    c: Coincident(g21,g22)
    c: Coincident(g22,g19)
    c: Horizontal(g19)
    c: Horizontal(g21)
    c: Vertical(g20)
    c: Vertical(g22)
    c: Coincident(g19,g15)
    c: Coincident(g20,g17)
    c: Coincident(g16,g19)
    c: Coincident(g18,g21)
    c: DistanceY(g22,g22) = 32.5
    c: DistanceX(g19,g19) = 32.5  'ScrewDistance'
    c: Symmetric(g16,g18,g-1)
    c: Radius(g18) = 1
    c: Radius(g15) = 1
    c: Radius(g16) = 1
    c: Radius(g17) = 1
FEATURE [PartDesign::Pad] Pad001
  Direction = (0,0,1)
  Length = 25.5
  Length2 = 100
  Profile = -> Sketch003
  Type = 0
  expr: Length = <<Joystick>>.BH
FEATURE [Sketcher::SketchObject] Sketch004
  FullyConstrained = true
  MapMode = 5
  Placement = pos=(0,0,0) rot=(1,0,0;1.5708rad)
  Support = -> [XZ_Plane003]
  expr: .AttachmentOffset.Rotation.Angle = <<Joystick>>.DEMO_ANGLE
  expr: .AttachmentOffset.Rotation.Axis.x = <<Joystick>>.DEMO_ANGLE_X
  expr: .AttachmentOffset.Rotation.Axis.z = <<Joystick>>.DEMO_ANGLE_Z
  expr: Constraints[10] = <<Joystick>>.B2JT
  expr: Constraints[11] = <<Joystick>>.JHH
  expr: Constraints[12] = <<Joystick>>.JD / 2
  expr: Constraints[13] = <<Joystick>>.BH / 2
  expr: Constraints[15] = <<Joystick>>.JD / 6
  sketch-geometry (7):
    g0: LineSegment StartX=0 StartY=84 StartZ=0 EndX=12.31 EndY=84 EndZ=0
    g1: LineSegment StartX=12.31 StartY=84 StartZ=0 EndX=17.5 EndY=75.9 EndZ=0
    g2: LineSegment StartX=17.5 StartY=75.9 StartZ=0 EndX=17.5 EndY=59.3 EndZ=0
    g3: LineSegment StartX=17.5 StartY=59.3 StartZ=0 EndX=5.83333 EndY=44.5 EndZ=0
    g4: LineSegment StartX=5.83333 StartY=44.5 StartZ=0 EndX=5.83333 EndY=12.75 EndZ=0
    g5: LineSegment StartX=5.83333 StartY=12.75 StartZ=0 EndX=0 EndY=12.75 EndZ=0
    g6: LineSegment StartX=0 StartY=84 StartZ=0 EndX=0 EndY=12.75 EndZ=0
  constraints (21):
    c: PointOnObject(g0,g-2)
    c: Coincident(g1,g0)
    c: Coincident(g2,g1)
    c: Vertical(g2)
    c: Coincident(g3,g2)
    c: Coincident(g4,g3)
    c: Coincident(g5,g4)
    c: PointOnObject(g5,g-2)
    c: Horizontal(g5)
    c: Horizontal(g0)
    c: DistanceY(g0) = 84
    c: DistanceY(g3,g0) = 39.5
    c: DistanceX(g1) = 17.5
    c: DistanceY(g5) = 12.75
    c: Vertical(g4)
    c: DistanceX(g5,g5) = 5.83333
    c: DistanceY(g1) = 75.9
    c: DistanceY(g2) = 59.3
    c: DistanceX(g0) = 12.31
    c: Coincident(g6,g0)
    c: Coincident(g6,g5)
FEATURE [PartDesign::Revolution] Revolution
  Angle = 360
  Axis = (0,-2e-16,1)
  Base = (0,0,0)
  BaseFeature = -> Pad001
  Profile = -> Sketch004
  ReferenceAxis = -> Sketch004 [V_Axis]
  Reversed = true
FEATURE [Spreadsheet::Sheet] Spreadsheet005  label="Joystick"
  cells = A2='Demo Angles; A3='X; B3(DEMO_ANGLE_X)=0; A4='Y; B4(DEMO_ANGLE_Y)=1; A5='Z; B5(DEMO_ANGLE_Z)=0; A6='Angle; B6(DEMO_ANGLE)=0; A7='Screw Distance; B7(SD)=32.5; A9='Screw; B9='M2x12; A10='Screw Body Diameter; B10(SBD)=2; A11='Base Depth; B11(BD)=40.4; A12='Base Width; B12(BW)=40.4; A13='Base Height; B13(BH)=25.5; A14='Potentiometer Extrusion; B14(PE)==49.6 - 40.4; A15='Potentiometer Extrusion Depth; B15(PED)==BD + PE; A16='Potentiometer Extrusion Width; B16(PEW)==BD + 2 * PE; A18='Joystick Handle Height; B18(JHH)=39.5; A19='Joystick Diameter; B19(JD)=35; A22='Base to Joystick Top; B22(B2JT)=84
